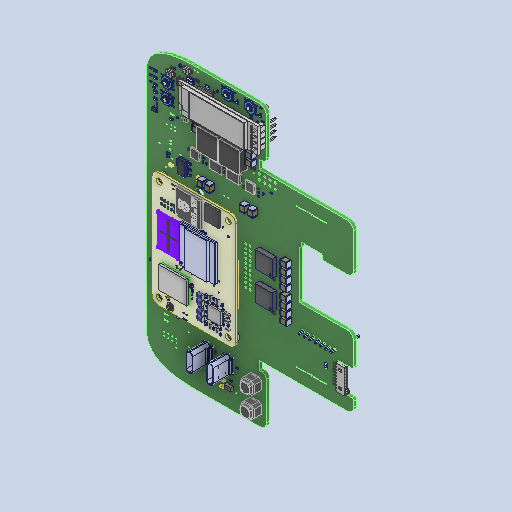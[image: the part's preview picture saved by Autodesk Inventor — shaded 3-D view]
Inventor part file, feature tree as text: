
AUTODESK INVENTOR PART (.ipt)
format: ipt  version: 2022 (Build 260153000, 153)  size: 57,349,120 bytes
history: native  units: mm
features: other x3628, sketch x2440, extrude x2
ambient origin geometry x8: Origin, YZ Plane, XZ Plane, XY Plane, X Axis, Y Axis, Z Axis, Center Point
bodies: Body1 (feature_tree), Body2 (feature_tree), Body3 (feature_tree), Body4 (feature_tree), Body5 (feature_tree), Body6 (feature_tree), Body7 (feature_tree), Body8 (feature_tree), Body9 (feature_tree), Body10 (feature_tree), Body11 (feature_tree), Body12 (feature_tree), Body13 (feature_tree), Body14 (feature_tree), Body15 (feature_tree), Body16 (feature_tree), Body17 (feature_tree), Body18 (feature_tree), Body19 (feature_tree), Body20 (feature_tree), Body21 (feature_tree), Body22 (feature_tree), Body23 (feature_tree), Body24 (feature_tree), Body25 (feature_tree), Body26 (feature_tree), Body27 (feature_tree), Body28 (feature_tree), Body29 (feature_tree), Body30 (feature_tree), Body31 (feature_tree), Body32 (feature_tree), Body33 (feature_tree), Body34 (feature_tree), Body35 (feature_tree), Body36 (feature_tree), Body37 (feature_tree), Body38 (feature_tree), Body39 (feature_tree), Body40 (feature_tree), Body41 (feature_tree), Body42 (feature_tree), Body43 (feature_tree), Body44 (feature_tree), Body45 (feature_tree), Body46 (feature_tree), Body47 (feature_tree), Body48 (feature_tree), Body49 (feature_tree), Body50 (feature_tree), Body51 (feature_tree), Body52 (feature_tree), Body53 (feature_tree), Body54 (feature_tree), Body55 (feature_tree), Body56 (feature_tree), Body57 (feature_tree), Body58 (feature_tree), Body59 (feature_tree), Body60 (feature_tree), Body61 (feature_tree), Body62 (feature_tree), Body63 (feature_tree), Body64 (feature_tree), Body65 (feature_tree), Body66 (feature_tree), Body67 (feature_tree), Body68 (feature_tree), Body69 (feature_tree), Body70 (feature_tree), Body71 (feature_tree), Body72 (feature_tree), Body73 (feature_tree), Body74 (feature_tree), Body75 (feature_tree), Body76 (feature_tree), Body77 (feature_tree), Body78 (feature_tree), Body79 (feature_tree), Body80 (feature_tree), Body81 (feature_tree), Body82 (feature_tree), Body83 (feature_tree), Body84 (feature_tree), Body85 (feature_tree), Body86 (feature_tree), Body87 (feature_tree), Body88 (feature_tree), Body89 (feature_tree), Body90 (feature_tree), Body91 (feature_tree), Body92 (feature_tree), Body93 (feature_tree), Body94 (feature_tree), Body95 (feature_tree), Body96 (feature_tree), Body97 (feature_tree), Body98 (feature_tree), Body99 (feature_tree), Body100 (feature_tree), Body101 (feature_tree), Body102 (feature_tree), Body103 (feature_tree), Body104 (feature_tree), Body105 (feature_tree), Body106 (feature_tree), Body107 (feature_tree), Body108 (feature_tree), Body109 (feature_tree), Body110 (feature_tree), Body111 (feature_tree), Body112 (feature_tree), Body113 (feature_tree), Body114 (feature_tree), Body115 (feature_tree), Body116 (feature_tree), Body117 (feature_tree), Body118 (feature_tree), Body119 (feature_tree), Body120 (feature_tree), Body121 (feature_tree), Body122 (feature_tree), Body123 (feature_tree), Body124 (feature_tree), Body125 (feature_tree), Body126 (feature_tree), Body127 (feature_tree), Body128 (feature_tree), Body129 (feature_tree), Body130 (feature_tree), Body131 (feature_tree), Body132 (feature_tree), Body133 (feature_tree), Body134 (feature_tree), Body135 (feature_tree), Body136 (feature_tree), Body137 (feature_tree), Body138 (feature_tree), Body139 (feature_tree), Body140 (feature_tree), Body141 (feature_tree), Body142 (feature_tree), Body143 (feature_tree), Body144 (feature_tree), Body145 (feature_tree), Body146 (feature_tree), Body147 (feature_tree), Body148 (feature_tree), Body149 (feature_tree), Body150 (feature_tree), Body151 (feature_tree), Body152 (feature_tree), Body153 (feature_tree), Body154 (feature_tree), Body155 (feature_tree), Body156 (feature_tree), Body157 (feature_tree), Body158 (feature_tree), Body159 (feature_tree), Body160 (feature_tree), Body161 (feature_tree), Body162 (feature_tree), Body163 (feature_tree), Body164 (feature_tree), Body165 (feature_tree), Body166 (feature_tree), Body167 (feature_tree), Body168 (feature_tree), Body169 (feature_tree), Body170 (feature_tree), Body171 (feature_tree), Body172 (feature_tree), Body173 (feature_tree), Body174 (feature_tree), Body175 (feature_tree), Body176 (feature_tree), Body177 (feature_tree), Body178 (feature_tree), Body179 (feature_tree), Body180 (feature_tree), Body181 (feature_tree), Body182 (feature_tree), Body183 (feature_tree), Body184 (feature_tree), Body185 (feature_tree), Body186 (feature_tree), Body187 (feature_tree), Body188 (feature_tree), Body189 (feature_tree), Body190 (feature_tree), Body191 (feature_tree), Body192 (feature_tree), Body193 (feature_tree), Body194 (feature_tree), Body195 (feature_tree), Body196 (feature_tree), Body197 (feature_tree), Body198 (feature_tree), Body199 (feature_tree), Body200 (feature_tree), Body201 (feature_tree), Body202 (feature_tree), Body203 (feature_tree), Body204 (feature_tree), Body205 (feature_tree), Body206 (feature_tree), Body207 (feature_tree), Body208 (feature_tree), Body209 (feature_tree), Body210 (feature_tree), Body211 (feature_tree), Body212 (feature_tree), Body213 (feature_tree), Body214 (feature_tree), Body215 (feature_tree), Body216 (feature_tree), Body217 (feature_tree), Body218 (feature_tree), Body219 (feature_tree), Body220 (feature_tree), Body221 (feature_tree), Body222 (feature_tree), Body223 (feature_tree), Body224 (feature_tree), Body225 (feature_tree), Body226 (feature_tree), Body227 (feature_tree), Body228 (feature_tree), Body229 (feature_tree), Body230 (feature_tree), Body231 (feature_tree), Body232 (feature_tree), Body233 (feature_tree), Body234 (feature_tree), Body235 (feature_tree), Body236 (feature_tree), Body237 (feature_tree), Body238 (feature_tree), Body239 (feature_tree), Body240 (feature_tree), Body241 (feature_tree), Body242 (feature_tree), Body243 (feature_tree), Body244 (feature_tree), Body245 (feature_tree), Body246 (feature_tree), Body247 (feature_tree), Body248 (feature_tree), Body249 (feature_tree), Body250 (feature_tree), Body251 (feature_tree), Body252 (feature_tree), Body253 (feature_tree), Body254 (feature_tree), Body255 (feature_tree), Body256 (feature_tree), Body257 (feature_tree), Body258 (feature_tree), Body259 (feature_tree), Body260 (feature_tree), Body261 (feature_tree), Body262 (feature_tree), Body263 (feature_tree), Body264 (feature_tree), Body265 (feature_tree), Body266 (feature_tree), Body267 (feature_tree), Body268 (feature_tree), Body269 (feature_tree), Body270 (feature_tree), Body271 (feature_tree), Body272 (feature_tree), Body273 (feature_tree), Body274 (feature_tree), Body275 (feature_tree), Body276 (feature_tree), Body277 (feature_tree), Body278 (feature_tree), Body279 (feature_tree), Body280 (feature_tree), Body281 (feature_tree), Body282 (feature_tree), Body283 (feature_tree), Body284 (feature_tree), Body285 (feature_tree), Body286 (feature_tree), Body287 (feature_tree), Body288 (feature_tree), Body289 (feature_tree), Body290 (feature_tree), Body291 (feature_tree), Body292 (feature_tree), Body293 (feature_tree), Body294 (feature_tree), Body295 (feature_tree), Body296 (feature_tree), Body297 (feature_tree), Body298 (feature_tree), Body299 (feature_tree), Body300 (feature_tree), Body301 (feature_tree), Body302 (feature_tree), Body303 (feature_tree), Body304 (feature_tree), Body305 (feature_tree), Body306 (feature_tree), Body307 (feature_tree), Body308 (feature_tree), Body309 (feature_tree), Body310 (feature_tree), Body311 (feature_tree), Body312 (feature_tree), Body313 (feature_tree), Body314 (feature_tree), Body315 (feature_tree), Body316 (feature_tree), Body317 (feature_tree), Body318 (feature_tree), Body319 (feature_tree), Body320 (feature_tree), Body321 (feature_tree), Body322 (feature_tree), Body323 (feature_tree), Body324 (feature_tree), Body325 (feature_tree), Body326 (feature_tree), Body327 (feature_tree), Body328 (feature_tree), Body329 (feature_tree), Body330 (feature_tree), Body331 (feature_tree), Body332 (feature_tree), Body333 (feature_tree), Body334 (feature_tree), Body335 (feature_tree), Body336 (feature_tree), Body337 (feature_tree), Body338 (feature_tree), Body339 (feature_tree), Body340 (feature_tree), Body341 (feature_tree), Body342 (feature_tree), Body343 (feature_tree), Body344 (feature_tree), Body345 (feature_tree), Body346 (feature_tree), Body347 (feature_tree), Body348 (feature_tree), Body349 (feature_tree), Body350 (feature_tree), Body351 (feature_tree), Body352 (feature_tree), Body353 (feature_tree), Body354 (feature_tree), Body355 (feature_tree), Body356 (feature_tree), Body357 (feature_tree), Body358 (feature_tree), Body359 (feature_tree), Body360 (feature_tree), Body361 (feature_tree), Body362 (feature_tree), Body363 (feature_tree), Body364 (feature_tree), Body365 (feature_tree), Body366 (feature_tree), Body367 (feature_tree), Body368 (feature_tree), Body369 (feature_tree), Body370 (feature_tree), Body371 (feature_tree), Body372 (feature_tree), Body373 (feature_tree), Body374 (feature_tree), Body375 (feature_tree), Body376 (feature_tree), Body377 (feature_tree), Body378 (feature_tree), Body379 (feature_tree), Body380 (feature_tree), Body381 (feature_tree), Body382 (feature_tree), Body383 (feature_tree), Body384 (feature_tree), Body385 (feature_tree), Body386 (feature_tree), Body387 (feature_tree), Body388 (feature_tree), Body389 (feature_tree), Body390 (feature_tree), Body391 (feature_tree), Body392 (feature_tree), Body393 (feature_tree), Body394 (feature_tree), Body395 (feature_tree), Body396 (feature_tree), Body397 (feature_tree), Body398 (feature_tree), Body399 (feature_tree), Body400 (feature_tree), Body401 (feature_tree), Body402 (feature_tree), Body403 (feature_tree), Body404 (feature_tree), Body405 (feature_tree), Body406 (feature_tree), Body407 (feature_tree), Body408 (feature_tree), Body409 (feature_tree), Body410 (feature_tree), Body411 (feature_tree), Body412 (feature_tree), Body413 (feature_tree), Body414 (feature_tree), Body415 (feature_tree), Body416 (feature_tree), Body417 (feature_tree), Body418 (feature_tree), Body419 (feature_tree), Body420 (feature_tree), Body421 (feature_tree), Body422 (feature_tree), Body423 (feature_tree), Body424 (feature_tree), Body425 (feature_tree), Body426 (feature_tree), Body427 (feature_tree), Body428 (feature_tree), Body429 (feature_tree), Body430 (feature_tree), Body431 (feature_tree), Body432 (feature_tree), Body433 (feature_tree), Body434 (feature_tree), Body435 (feature_tree), Body436 (feature_tree), Body437 (feature_tree), Body438 (feature_tree), Body439 (feature_tree), Body440 (feature_tree), Body441 (feature_tree), Body442 (feature_tree), Body443 (feature_tree), Body444 (feature_tree), Body445 (feature_tree), Body446 (feature_tree), Body447 (feature_tree), Body448 (feature_tree), Body449 (feature_tree), Body450 (feature_tree), Body451 (feature_tree), Body452 (feature_tree), Body453 (feature_tree), Body454 (feature_tree), Body455 (feature_tree), Body456 (feature_tree), Body457 (feature_tree), Body458 (feature_tree), Body459 (feature_tree), Body460 (feature_tree), Body461 (feature_tree), Body462 (feature_tree), Body463 (feature_tree), Body464 (feature_tree), Body465 (feature_tree), Body466 (feature_tree), Body467 (feature_tree), Body468 (feature_tree), Body469 (feature_tree), Body470 (feature_tree), Body471 (feature_tree), Body472 (feature_tree), Body473 (feature_tree), Body474 (feature_tree), Body475 (feature_tree), Body476 (feature_tree), Body477 (feature_tree), Body478 (feature_tree), Body479 (feature_tree), Body480 (feature_tree), Body481 (feature_tree), Body482 (feature_tree), Body483 (feature_tree), Body484 (feature_tree), Body485 (feature_tree), Body486 (feature_tree), Body487 (feature_tree), Body488 (feature_tree), Body489 (feature_tree), Body490 (feature_tree), Body491 (feature_tree), Body492 (feature_tree), Body493 (feature_tree), Body494 (feature_tree), Body495 (feature_tree), Body496 (feature_tree), Body497 (feature_tree), Body498 (feature_tree), Body499 (feature_tree), Body500 (feature_tree), Body501 (feature_tree), Body502 (feature_tree), Body503 (feature_tree), Body504 (feature_tree), Body505 (feature_tree), Body506 (feature_tree), Body507 (feature_tree), Body508 (feature_tree), Body509 (feature_tree), Body510 (feature_tree), Body511 (feature_tree), Body512 (feature_tree), Body513 (feature_tree), Body514 (feature_tree), Body515 (feature_tree), Body516 (feature_tree), Body517 (feature_tree), Body518 (feature_tree), Body519 (feature_tree), Body520 (feature_tree), Body521 (feature_tree), Body522 (feature_tree), Body523 (feature_tree), Body524 (feature_tree), Body525 (feature_tree), Body526 (feature_tree), Body527 (feature_tree), Body528 (feature_tree), Body529 (feature_tree), Body530 (feature_tree), Body531 (feature_tree), Body532 (feature_tree), Body533 (feature_tree), Body534 (feature_tree), Body535 (feature_tree), Body536 (feature_tree), Body537 (feature_tree), Body538 (feature_tree), Body539 (feature_tree), Body540 (feature_tree), Body541 (feature_tree), Body542 (feature_tree), Body543 (feature_tree), Body544 (feature_tree), Body545 (feature_tree), Body546 (feature_tree), Body547 (feature_tree), Body548 (feature_tree), Body549 (feature_tree), Body550 (feature_tree), Body551 (feature_tree), Body552 (feature_tree), Body553 (feature_tree), Body554 (feature_tree), Body555 (feature_tree), Body556 (feature_tree), Body557 (feature_tree), Body558 (feature_tree), Body559 (feature_tree), Body560 (feature_tree), Body561 (feature_tree), Body562 (feature_tree), Body563 (feature_tree), Body564 (feature_tree), Body565 (feature_tree), Body566 (feature_tree), Body567 (feature_tree), Body568 (feature_tree), Body569 (feature_tree), Body570 (feature_tree), Body571 (feature_tree), Body572 (feature_tree), Body573 (feature_tree), Body574 (feature_tree), Body575 (feature_tree), Body576 (feature_tree), Body577 (feature_tree), Body578 (feature_tree), Body579 (feature_tree), Body580 (feature_tree), Body581 (feature_tree), Body582 (feature_tree), Body583 (feature_tree), Body584 (feature_tree), Body585 (feature_tree), Body586 (feature_tree), Body587 (feature_tree), Body588 (feature_tree), Body589 (feature_tree), Body590 (feature_tree), Body591 (feature_tree), Body592 (feature_tree), Body593 (feature_tree), Body594 (feature_tree), Body595 (feature_tree), Body596 (feature_tree), Body597 (feature_tree), Body598 (feature_tree), Body599 (feature_tree), Body600 (feature_tree), Body601 (feature_tree), Body602 (feature_tree), Body603 (feature_tree), Body604 (feature_tree), Body605 (feature_tree), Body606 (feature_tree), Body607 (feature_tree), Body608 (feature_tree), Body609 (feature_tree), Body610 (feature_tree), Body611 (feature_tree), Body612 (feature_tree), Body613 (feature_tree), Body614 (feature_tree), Body615 (feature_tree), Body616 (feature_tree), Body617 (feature_tree), Body618 (feature_tree), Body619 (feature_tree), Body620 (feature_tree), Body621 (feature_tree), Body622 (feature_tree), Body623 (feature_tree), Body624 (feature_tree), Body625 (feature_tree), Body626 (feature_tree), Body627 (feature_tree), Body628 (feature_tree), Body629 (feature_tree), Body630 (feature_tree), Body631 (feature_tree), Body632 (feature_tree), Body633 (feature_tree), Body634 (feature_tree), Body635 (feature_tree), Body636 (feature_tree), Body637 (feature_tree), Body638 (feature_tree), Body639 (feature_tree), Body640 (feature_tree), Body641 (feature_tree), Body642 (feature_tree), Body643 (feature_tree), Body644 (feature_tree), Body645 (feature_tree), Body646 (feature_tree), Body647 (feature_tree), Body648 (feature_tree), Body649 (feature_tree), Body650 (feature_tree), Body651 (feature_tree), Body652 (feature_tree), Body653 (feature_tree), Body654 (feature_tree), Body655 (feature_tree), Body656 (feature_tree), Body657 (feature_tree), Body658 (feature_tree), Body659 (feature_tree), Body660 (feature_tree), Body661 (feature_tree), Body662 (feature_tree), Body663 (feature_tree), Body664 (feature_tree), Body665 (feature_tree), Body666 (feature_tree), Body667 (feature_tree), Body668 (feature_tree), Body669 (feature_tree), Body670 (feature_tree), Body671 (feature_tree), Body672 (feature_tree), Body673 (feature_tree), Body674 (feature_tree), Body675 (feature_tree), Body676 (feature_tree), Body677 (feature_tree), Body678 (feature_tree), Body679 (feature_tree), Body680 (feature_tree), Body681 (feature_tree), Body682 (feature_tree), Body683 (feature_tree), Body684 (feature_tree), Body685 (feature_tree), Body686 (feature_tree), Body687 (feature_tree), Body688 (feature_tree), Body689 (feature_tree), Body690 (feature_tree), Body691 (feature_tree), Body692 (feature_tree), Body693 (feature_tree), Body694 (feature_tree), Body695 (feature_tree), Body696 (feature_tree), Body697 (feature_tree), Body698 (feature_tree), Body699 (feature_tree), Body700 (feature_tree), Body701 (feature_tree), Body702 (feature_tree), Body703 (feature_tree), Body704 (feature_tree), Body705 (feature_tree), Body706 (feature_tree), Body707 (feature_tree), Body708 (feature_tree), Body709 (feature_tree), Body710 (feature_tree), Body711 (feature_tree), Body712 (feature_tree), Body713 (feature_tree), Body714 (feature_tree), Body715 (feature_tree), Body716 (feature_tree), Body717 (feature_tree), Body718 (feature_tree), Body719 (feature_tree), Body720 (feature_tree), Body721 (feature_tree), Body722 (feature_tree), Body723 (feature_tree), Body724 (feature_tree), Body725 (feature_tree), Body726 (feature_tree), Body727 (feature_tree), Body728 (feature_tree), Body729 (feature_tree), Body730 (feature_tree), Body731 (feature_tree), Body732 (feature_tree), Body733 (feature_tree), Body734 (feature_tree), Body735 (feature_tree), Body736 (feature_tree), Body737 (feature_tree), Body738 (feature_tree), Body739 (feature_tree), Body740 (feature_tree), Body741 (feature_tree), Body742 (feature_tree), Body743 (feature_tree), Body744 (feature_tree), Body745 (feature_tree), Body746 (feature_tree), Body747 (feature_tree), Body748 (feature_tree), Body749 (feature_tree), Body750 (feature_tree), Body751 (feature_tree), Body752 (feature_tree), Body753 (feature_tree), Body754 (feature_tree), Body755 (feature_tree), Body756 (feature_tree), Body757 (feature_tree), Body758 (feature_tree), Body759 (feature_tree), Body760 (feature_tree), Body761 (feature_tree), Body762 (feature_tree), Body763 (feature_tree), Body764 (feature_tree), Body765 (feature_tree), Body766 (feature_tree), Body767 (feature_tree), Body768 (feature_tree), Body769 (feature_tree), Body770 (feature_tree), Body771 (feature_tree), Body772 (feature_tree), Body773 (feature_tree), Body774 (feature_tree), Body775 (feature_tree), Body776 (feature_tree), Body777 (feature_tree), Body778 (feature_tree), Body779 (feature_tree), Body780 (feature_tree), Body781 (feature_tree), Body782 (feature_tree), Body783 (feature_tree), Body784 (feature_tree), Body785 (feature_tree), Body786 (feature_tree), Body787 (feature_tree), Body788 (feature_tree), Body789 (feature_tree), Body790 (feature_tree), Body791 (feature_tree), Body792 (feature_tree), Body793 (feature_tree), Body794 (feature_tree), Body795 (feature_tree), Body796 (feature_tree), Body797 (feature_tree), Body798 (feature_tree), Body799 (feature_tree), Body800 (feature_tree), Body801 (feature_tree), Body802 (feature_tree), Body803 (feature_tree), Body804 (feature_tree), Body805 (feature_tree), Body806 (feature_tree), Body807 (feature_tree), Body808 (feature_tree), Body809 (feature_tree), Body810 (feature_tree), Body811 (feature_tree), Body812 (feature_tree), Body813 (feature_tree), Body814 (feature_tree), Body815 (feature_tree), Body816 (feature_tree), Body817 (feature_tree), Body818 (feature_tree), Body819 (feature_tree), Body820 (feature_tree), Body821 (feature_tree), Body822 (feature_tree), Body823 (feature_tree), Body824 (feature_tree), Body825 (feature_tree), Body826 (feature_tree), Body827 (feature_tree), Body828 (feature_tree), Body829 (feature_tree), Body830 (feature_tree), Body831 (feature_tree), Body832 (feature_tree), Body833 (feature_tree), Body834 (feature_tree), Body835 (feature_tree), Body836 (feature_tree), Body837 (feature_tree), Body838 (feature_tree), Body839 (feature_tree), Body840 (feature_tree), Body841 (feature_tree), Body842 (feature_tree), Body843 (feature_tree), Body844 (feature_tree), Body845 (feature_tree), Body846 (feature_tree), Body847 (feature_tree), Body848 (feature_tree), Body849 (feature_tree), Body850 (feature_tree), Body851 (feature_tree), Body852 (feature_tree), Body853 (feature_tree), Body854 (feature_tree), Body855 (feature_tree), Body856 (feature_tree), Body857 (feature_tree), Body858 (feature_tree), Body859 (feature_tree), Body860 (feature_tree), Body861 (feature_tree), Body862 (feature_tree), Body863 (feature_tree), Body864 (feature_tree), Body865 (feature_tree), Body866 (feature_tree), Body867 (feature_tree), Body868 (feature_tree), Body869 (feature_tree), Body870 (feature_tree), Body871 (feature_tree), Body872 (feature_tree), Body873 (feature_tree), Body874 (feature_tree), Body875 (feature_tree), Body876 (feature_tree), Body877 (feature_tree), Body878 (feature_tree), Body879 (feature_tree), Body880 (feature_tree), Body881 (feature_tree), Body882 (feature_tree), Body883 (feature_tree), Body884 (feature_tree), Body885 (feature_tree), Body886 (feature_tree), Body887 (feature_tree), Body888 (feature_tree), Body889 (feature_tree), Body890 (feature_tree), Body891 (feature_tree), Body892 (feature_tree), Body893 (feature_tree), Body894 (feature_tree), Body895 (feature_tree), Body896 (feature_tree), Body897 (feature_tree), Body898 (feature_tree), Body899 (feature_tree), Body900 (feature_tree), Body901 (feature_tree), Body902 (feature_tree), Body903 (feature_tree), Body904 (feature_tree), Body905 (feature_tree), Body906 (feature_tree), Body907 (feature_tree), Body908 (feature_tree), Body909 (feature_tree), Body910 (feature_tree), Body911 (feature_tree), Body912 (feature_tree), Body913 (feature_tree), Body914 (feature_tree), Body915 (feature_tree), Body916 (feature_tree), Body917 (feature_tree), Body918 (feature_tree), Body919 (feature_tree), Body920 (feature_tree), Body921 (feature_tree), Body922 (feature_tree), Body923 (feature_tree), Body924 (feature_tree), Body925 (feature_tree), Body926 (feature_tree), Body927 (feature_tree), Body928 (feature_tree), Body929 (feature_tree), Body930 (feature_tree), Body931 (feature_tree), Body932 (feature_tree), Body933 (feature_tree), Body934 (feature_tree), Body935 (feature_tree), Body936 (feature_tree), Body937 (feature_tree), Body938 (feature_tree), Body939 (feature_tree), Body940 (feature_tree), Body941 (feature_tree), Body942 (feature_tree), Body943 (feature_tree), Body944 (feature_tree), Body945 (feature_tree), Body946 (feature_tree), Body947 (feature_tree), Body948 (feature_tree), Body949 (feature_tree), Body950 (feature_tree), Body951 (feature_tree), Body952 (feature_tree), Body953 (feature_tree), Body954 (feature_tree), Body955 (feature_tree), Body956 (feature_tree), Body957 (feature_tree), Body958 (feature_tree), Body959 (feature_tree), Body960 (feature_tree), Body961 (feature_tree), Body962 (feature_tree), Body963 (feature_tree), Body964 (feature_tree), Body965 (feature_tree), Body966 (feature_tree), Body967 (feature_tree), Body968 (feature_tree), Body969 (feature_tree), Body970 (feature_tree), Body971 (feature_tree), Body972 (feature_tree), Body973 (feature_tree), Body974 (feature_tree), Body975 (feature_tree), Body976 (feature_tree), Body977 (feature_tree), Body978 (feature_tree), Body979 (feature_tree), Body980 (feature_tree), Body981 (feature_tree), Body982 (feature_tree), Body983 (feature_tree), Body984 (feature_tree), Body985 (feature_tree), Body986 (feature_tree), Body987 (feature_tree), Body988 (feature_tree), Body989 (feature_tree), Body990 (feature_tree), Body991 (feature_tree), Body992 (feature_tree), Body993 (feature_tree), Body994 (feature_tree), Body995 (feature_tree), Body996 (feature_tree), Body997 (feature_tree), Body998 (feature_tree), Body999 (feature_tree), Body1000 (feature_tree), Body1001 (feature_tree), Body1002 (feature_tree), Body1003 (feature_tree), Body1004 (feature_tree), Body1005 (feature_tree), Body1006 (feature_tree), Body1007 (feature_tree), Body1008 (feature_tree), Body1009 (feature_tree), Body1010 (feature_tree), Body1011 (feature_tree), Body1012 (feature_tree), Body1013 (feature_tree), Body1014 (feature_tree), Body1015 (feature_tree), Body1016 (feature_tree), Body1017 (feature_tree), Body1018 (feature_tree), Body1019 (feature_tree), Body1020 (feature_tree), Body1021 (feature_tree), Body1022 (feature_tree), Body1023 (feature_tree), Body1024 (feature_tree), Body1025 (feature_tree), Body1026 (feature_tree), Body1027 (feature_tree), Body1028 (feature_tree), Body1029 (feature_tree), Body1030 (feature_tree), Body1031 (feature_tree), Body1032 (feature_tree), Body1033 (feature_tree), Body1034 (feature_tree), Body1035 (feature_tree), Body1036 (feature_tree), Body1037 (feature_tree), Body1038 (feature_tree), Body1039 (feature_tree), Body1040 (feature_tree), Body1041 (feature_tree), Body1042 (feature_tree), Body1043 (feature_tree), Body1044 (feature_tree), Body1045 (feature_tree), Body1046 (feature_tree), Body1047 (feature_tree), Body1048 (feature_tree), Body1049 (feature_tree), Body1050 (feature_tree), Body1051 (feature_tree), Body1052 (feature_tree), Body1053 (feature_tree), Body1054 (feature_tree), Body1055 (feature_tree), Body1056 (feature_tree), Body1057 (feature_tree), Body1058 (feature_tree), Body1059 (feature_tree), Body1060 (feature_tree), Body1061 (feature_tree), Body1062 (feature_tree), Body1063 (feature_tree), Body1064 (feature_tree), Body1065 (feature_tree), Body1066 (feature_tree), Body1067 (feature_tree), Body1068 (feature_tree), Body1069 (feature_tree), Body1070 (feature_tree), Body1071 (feature_tree), Body1072 (feature_tree), Body1073 (feature_tree), Body1074 (feature_tree), Body1075 (feature_tree), Body1076 (feature_tree), Body1077 (feature_tree), Body1078 (feature_tree), Body1079 (feature_tree), Body1080 (feature_tree), Body1081 (feature_tree), Body1082 (feature_tree), Body1083 (feature_tree), Body1084 (feature_tree), Body1085 (feature_tree), Body1086 (feature_tree), Body1087 (feature_tree), Body1088 (feature_tree), Body1089 (feature_tree), Body1090 (feature_tree), Body1091 (feature_tree), Body1092 (feature_tree), Body1093 (feature_tree), Body1094 (feature_tree), Body1095 (feature_tree), Body1096 (feature_tree), Body1097 (feature_tree), Body1098 (feature_tree), Body1099 (feature_tree), Body1100 (feature_tree), Body1101 (feature_tree), Body1102 (feature_tree), Body1103 (feature_tree), Body1104 (feature_tree), Body1105 (feature_tree), Body1106 (feature_tree), Body1107 (feature_tree), Body1108 (feature_tree), Body1109 (feature_tree), Body1110 (feature_tree), Body1111 (feature_tree), Body1112 (feature_tree), Body1113 (feature_tree), Body1114 (feature_tree), Body1115 (feature_tree), Body1116 (feature_tree), Body1117 (feature_tree), Body1118 (feature_tree), Body1119 (feature_tree), Body1120 (feature_tree), Body1121 (feature_tree), Body1122 (feature_tree), Body1123 (feature_tree), Body1124 (feature_tree), Body1125 (feature_tree), Body1126 (feature_tree), Body1127 (feature_tree), Body1128 (feature_tree), Body1129 (feature_tree), Body1130 (feature_tree), Body1131 (feature_tree), Body1132 (feature_tree), Body1133 (feature_tree), Body1134 (feature_tree), Body1135 (feature_tree), Body1136 (feature_tree), Body1137 (feature_tree), Body1138 (feature_tree), Body1139 (feature_tree), Body1140 (feature_tree), Body1141 (feature_tree), Body1142 (feature_tree), Body1143 (feature_tree), Body1144 (feature_tree), Body1145 (feature_tree), Body1146 (feature_tree), Body1147 (feature_tree), Body1148 (feature_tree), Body1149 (feature_tree), Body1150 (feature_tree), Body1151 (feature_tree), Body1152 (feature_tree), Body1153 (feature_tree), Body1154 (feature_tree), Body1155 (feature_tree), Body1156 (feature_tree), Body1157 (feature_tree), Body1158 (feature_tree), Body1159 (feature_tree), Body1160 (feature_tree), Body1161 (feature_tree), Body1162 (feature_tree), Body1163 (feature_tree), Body1164 (feature_tree), Body1165 (feature_tree), Body1166 (feature_tree), Body1167 (feature_tree), Body1168 (feature_tree), Body1169 (feature_tree), Body1170 (feature_tree), Body1171 (feature_tree), Body1172 (feature_tree), Body1173 (feature_tree), Body1174 (feature_tree), Body1175 (feature_tree), Body1176 (feature_tree), Body1177 (feature_tree), Body1178 (feature_tree), Body1179 (feature_tree), Body1180 (feature_tree), Body1181 (feature_tree), Body1182 (feature_tree), Body1183 (feature_tree), Body1184 (feature_tree), Body1185 (feature_tree), Body1186 (feature_tree), Body1187 (feature_tree), Body1188 (feature_tree), Body1189 (feature_tree), Body1190 (feature_tree), Body1191 (feature_tree), Body1192 (feature_tree), Body1193 (feature_tree), Body1194 (feature_tree), Body1195 (feature_tree), Body1196 (feature_tree), Body1197 (feature_tree), Body1198 (feature_tree), Body1199 (feature_tree), Body1200 (feature_tree), Body1201 (feature_tree), Body1202 (feature_tree), Body1203 (feature_tree), Body1204 (feature_tree), Body1205 (feature_tree), Body1206 (feature_tree), Body1207 (feature_tree), Body1208 (feature_tree), Body1209 (feature_tree), Body1210 (feature_tree), Body1211 (feature_tree), Body1212 (feature_tree), Body1213 (feature_tree), Body1214 (feature_tree), Body1215 (feature_tree), Body1216 (feature_tree), Body1217 (feature_tree), Body1218 (feature_tree), Body1219 (feature_tree), Body1220 (feature_tree), Body1221 (feature_tree), Body1222 (feature_tree), Body1223 (feature_tree), Body1224 (feature_tree), Body1225 (feature_tree), Body1226 (feature_tree), Body1227 (feature_tree), Body1228 (feature_tree), Body1229 (feature_tree), Body1230 (feature_tree), Body1231 (feature_tree), Body1232 (feature_tree), Body1233 (feature_tree), Body1234 (feature_tree), Body1235 (feature_tree), Body1236 (feature_tree), Body1237 (feature_tree), Body1238 (feature_tree), Body1239 (feature_tree), Body1240 (feature_tree), Body1241 (feature_tree), Body1242 (feature_tree), Body1243 (feature_tree), Body1244 (feature_tree), Body1245 (feature_tree), Body1246 (feature_tree), Body1247 (feature_tree), Body1248 (feature_tree), Body1249 (feature_tree), Body1250 (feature_tree), Body1251 (feature_tree), Body1252 (feature_tree), Body1253 (feature_tree), Body1254 (feature_tree), Body1255 (feature_tree), Body1256 (feature_tree), Body1257 (feature_tree), Body1258 (feature_tree), Body1259 (feature_tree), Body1260 (feature_tree), Body1261 (feature_tree), Body1262 (feature_tree), Body1263 (feature_tree), Body1264 (feature_tree), Body1265 (feature_tree), Body1266 (feature_tree), Body1267 (feature_tree), Body1268 (feature_tree), Body1269 (feature_tree), Body1270 (feature_tree), Body1271 (feature_tree), Body1272 (feature_tree), Body1273 (feature_tree), Body1274 (feature_tree), Body1275 (feature_tree), Body1276 (feature_tree), Body1277 (feature_tree), Body1278 (feature_tree), Body1279 (feature_tree), Body1280 (feature_tree), Body1281 (feature_tree), Body1282 (feature_tree), Body1283 (feature_tree), Body1284 (feature_tree), Body1285 (feature_tree), Body1286 (feature_tree), Body1287 (feature_tree), Body1288 (feature_tree), Body1289 (feature_tree), Body1290 (feature_tree), Body1291 (feature_tree), Body1292 (feature_tree), Body1293 (feature_tree), Body1294 (feature_tree), Body1295 (feature_tree), Body1296 (feature_tree), Body1297 (feature_tree), Body1298 (feature_tree), Body1299 (feature_tree), Body1300 (feature_tree), Body1301 (feature_tree), Body1302 (feature_tree), Body1303 (feature_tree), Body1304 (feature_tree), Body1305 (feature_tree), Body1306 (feature_tree), Body1307 (feature_tree), Body1308 (feature_tree), Body1309 (feature_tree), Body1310 (feature_tree), Body1311 (feature_tree), Body1312 (feature_tree), Body1313 (feature_tree), Body1314 (feature_tree), Body1315 (feature_tree), Body1316 (feature_tree), Body1317 (feature_tree), Body1318 (feature_tree), Body1319 (feature_tree), Body1320 (feature_tree), Body1321 (feature_tree), Body1322 (feature_tree), Body1323 (feature_tree), Body1324 (feature_tree), Body1325 (feature_tree), Body1326 (feature_tree), Body1327 (feature_tree), Body1328 (feature_tree), Body1329 (feature_tree), Body1330 (feature_tree), Body1331 (feature_tree), Body1332 (feature_tree), Body1333 (feature_tree), Body1334 (feature_tree), Body1335 (feature_tree), Body1336 (feature_tree), Body1337 (feature_tree), Body1338 (feature_tree), Body1339 (feature_tree), Body1340 (feature_tree), Body1341 (feature_tree), Body1342 (feature_tree), Body1343 (feature_tree), Body1344 (feature_tree), Body1345 (feature_tree), Body1346 (feature_tree), Body1347 (feature_tree), Body1348 (feature_tree), Body1349 (feature_tree), Body1350 (feature_tree), Body1351 (feature_tree), Body1352 (feature_tree), Body1353 (feature_tree), Body1354 (feature_tree), Body1355 (feature_tree), Body1356 (feature_tree), Body1357 (feature_tree), Body1358 (feature_tree), Body1359 (feature_tree), Body1360 (feature_tree), Body1361 (feature_tree), Body1362 (feature_tree), Body1363 (feature_tree), Body1364 (feature_tree), Body1365 (feature_tree), Body1366 (feature_tree), Body1367 (feature_tree), Body1368 (feature_tree), Body1369 (feature_tree), Body1370 (feature_tree), Body1371 (feature_tree), Body1372 (feature_tree), Body1373 (feature_tree), Body1374 (feature_tree), Body1375 (feature_tree), Body1376 (feature_tree), Body1377 (feature_tree), Body1378 (feature_tree), Body1379 (feature_tree), Body1380 (feature_tree), Body1381 (feature_tree), Body1382 (feature_tree), Body1383 (feature_tree), Body1384 (feature_tree), Body1385 (feature_tree), Body1386 (feature_tree), Body1387 (feature_tree), Body1388 (feature_tree), Body1389 (feature_tree), Body1390 (feature_tree), Body1391 (feature_tree), Body1392 (feature_tree), Body1393 (feature_tree), Body1394 (feature_tree), Body1395 (feature_tree), Body1396 (feature_tree), Body1397 (feature_tree), Body1398 (feature_tree), Body1399 (feature_tree), Body1400 (feature_tree), Body1401 (feature_tree), Body1402 (feature_tree), Body1403 (feature_tree), Body1404 (feature_tree), Body1405 (feature_tree), Body1406 (feature_tree), Body1407 (feature_tree), Body1408 (feature_tree), Body1409 (feature_tree), Body1410 (feature_tree), Body1411 (feature_tree), Body1412 (feature_tree), Body1413 (feature_tree), Body1414 (feature_tree), Body1415 (feature_tree), Body1416 (feature_tree), Body1417 (feature_tree), Body1418 (feature_tree), Body1419 (feature_tree), Body1420 (feature_tree), Body1421 (feature_tree), Body1422 (feature_tree), Body1423 (feature_tree), Body1424 (feature_tree), Body1425 (feature_tree), Body1426 (feature_tree), Body1427 (feature_tree), Body1428 (feature_tree), Body1429 (feature_tree), Body1430 (feature_tree), Body1431 (feature_tree), Body1432 (feature_tree), Body1433 (feature_tree), Body1434 (feature_tree), Body1435 (feature_tree), Body1436 (feature_tree), Body1437 (feature_tree), Body1438 (feature_tree), Body1439 (feature_tree), Body1440 (feature_tree), Body1441 (feature_tree), Body1442 (feature_tree), Body1443 (feature_tree), Body1444 (feature_tree), Body1445 (feature_tree), Body1446 (feature_tree), Body1447 (feature_tree), Body1448 (feature_tree), Body1449 (feature_tree), Body1450 (feature_tree), Body1451 (feature_tree), Body1452 (feature_tree), Body1453 (feature_tree), Body1454 (feature_tree), Body1455 (feature_tree), Body1456 (feature_tree), Body1457 (feature_tree), Body1458 (feature_tree), Body1459 (feature_tree), Body1460 (feature_tree), Body1461 (feature_tree), Body1462 (feature_tree), Body1463 (feature_tree), Body1464 (feature_tree), Body1465 (feature_tree), Body1466 (feature_tree), Body1467 (feature_tree), Body1468 (feature_tree), Body1469 (feature_tree), Body1470 (feature_tree), Body1471 (feature_tree), Body1472 (feature_tree), Body1473 (feature_tree), Body1474 (feature_tree), Body1475 (feature_tree), Body1476 (feature_tree), Body1477 (feature_tree), Body1478 (feature_tree), Body1479 (feature_tree), Body1480 (feature_tree), Body1481 (feature_tree), Body1482 (feature_tree), Body1483 (feature_tree), Body1484 (feature_tree), Body1485 (feature_tree), Body1486 (feature_tree), Body1487 (feature_tree), Body1488 (feature_tree), Body1489 (feature_tree), Body1490 (feature_tree), Body1491 (feature_tree), Body1492 (feature_tree), Body1493 (feature_tree), Body1494 (feature_tree), Body1495 (feature_tree), Body1496 (feature_tree), Body1497 (feature_tree), Body1498 (feature_tree), Body1499 (feature_tree), Body1500 (feature_tree), Body1501 (feature_tree), Body1502 (feature_tree), Body1503 (feature_tree), Body1504 (feature_tree), Body1505 (feature_tree), Body1506 (feature_tree), Body1507 (feature_tree), Body1508 (feature_tree), Body1509 (feature_tree), Body1510 (feature_tree), Body1511 (feature_tree), Body1512 (feature_tree), Body1513 (feature_tree), Body1514 (feature_tree), Body1515 (feature_tree), Body1516 (feature_tree), Body1517 (feature_tree), Body1518 (feature_tree), Body1519 (feature_tree), Body1520 (feature_tree), Body1521 (feature_tree), Body1522 (feature_tree), Body1523 (feature_tree), Body1524 (feature_tree), Body1525 (feature_tree), Body1526 (feature_tree), Body1527 (feature_tree), Body1528 (feature_tree), Body1529 (feature_tree), Body1530 (feature_tree), Body1531 (feature_tree), Body1532 (feature_tree), Body1533 (feature_tree), Body1534 (feature_tree), Body1535 (feature_tree), Body1536 (feature_tree), Body1537 (feature_tree), Body1538 (feature_tree), Body1539 (feature_tree), Body1540 (feature_tree), Body1541 (feature_tree), Body1542 (feature_tree), Body1543 (feature_tree), Body1544 (feature_tree), Body1545 (feature_tree), Body1546 (feature_tree), Body1547 (feature_tree), Body1548 (feature_tree), Body1549 (feature_tree), Body1550 (feature_tree), Body1551 (feature_tree), Body1552 (feature_tree), Body1553 (feature_tree), Body1554 (feature_tree), Body1555 (feature_tree), Body1556 (feature_tree), Body1557 (feature_tree), Body1558 (feature_tree), Body1559 (feature_tree), Body1560 (feature_tree), Body1561 (feature_tree), Body1562 (feature_tree), Body1563 (feature_tree), Body1564 (feature_tree), Body1565 (feature_tree), Body1566 (feature_tree), Body1567 (feature_tree), Body1568 (feature_tree), Body1569 (feature_tree), Body1570 (feature_tree), Body1571 (feature_tree), Body1572 (feature_tree), Body1573 (feature_tree), Body1574 (feature_tree), Body1575 (feature_tree), Body1576 (feature_tree), Body1577 (feature_tree), Body1578 (feature_tree), Body1579 (feature_tree), Body1580 (feature_tree), Body1581 (feature_tree), Body1582 (feature_tree), Body1583 (feature_tree), Body1584 (feature_tree), Body1585 (feature_tree), Body1586 (feature_tree), Body1587 (feature_tree), Body1588 (feature_tree), Body1589 (feature_tree), Body1590 (feature_tree), Body1591 (feature_tree), Body1592 (feature_tree), Body1593 (feature_tree), Body1594 (feature_tree), Body1595 (feature_tree), Body1596 (feature_tree), Body1597 (feature_tree), Body1598 (feature_tree), Body1599 (feature_tree), Body1600 (feature_tree), Body1601 (feature_tree), Body1602 (feature_tree), Body1603 (feature_tree), Body1604 (feature_tree), Body1605 (feature_tree), Body1606 (feature_tree), Body1607 (feature_tree), Body1608 (feature_tree), Body1609 (feature_tree), Body1610 (feature_tree), Body1611 (feature_tree), Body1612 (feature_tree), Body1613 (feature_tree), Body1614 (feature_tree), Body1615 (feature_tree), Body1616 (feature_tree), Body1617 (feature_tree), Body1618 (feature_tree), Body1619 (feature_tree), Body1620 (feature_tree), Body1621 (feature_tree), Body1622 (feature_tree), Body1623 (feature_tree), Body1624 (feature_tree), Body1625 (feature_tree), Body1626 (feature_tree), Body1627 (feature_tree), Body1628 (feature_tree), Body1629 (feature_tree), Body1630 (feature_tree), Body1631 (feature_tree), Body1632 (feature_tree), Body1633 (feature_tree), Body1634 (feature_tree), Body1635 (feature_tree), Body1636 (feature_tree), Body1637 (feature_tree), Body1638 (feature_tree), Body1639 (feature_tree), Body1640 (feature_tree), Body1641 (feature_tree), Body1642 (feature_tree), Body1643 (feature_tree), Body1644 (feature_tree), Body1645 (feature_tree), Body1646 (feature_tree), Body1647 (feature_tree), Body1648 (feature_tree), Body1649 (feature_tree), Body1650 (feature_tree), Body1651 (feature_tree), Body1652 (feature_tree), Body1653 (feature_tree), Body1654 (feature_tree), Body1655 (feature_tree), Body1656 (feature_tree), Body1657 (feature_tree), Body1658 (feature_tree), Body1659 (feature_tree), Body1660 (feature_tree), Body1661 (feature_tree), Body1662 (feature_tree), Body1663 (feature_tree), Body1664 (feature_tree), Body1665 (feature_tree), Body1666 (feature_tree), Body1667 (feature_tree), Body1668 (feature_tree), Body1669 (feature_tree), Body1670 (feature_tree), Body1671 (feature_tree), Body1672 (feature_tree), Body1673 (feature_tree), Body1674 (feature_tree), Body1675 (feature_tree), Body1676 (feature_tree), Body1677 (feature_tree), Body1678 (feature_tree), Body1679 (feature_tree), Body1680 (feature_tree), Body1681 (feature_tree), Body1682 (feature_tree), Body1683 (feature_tree), Body1684 (feature_tree), Body1685 (feature_tree), Body1686 (feature_tree), Body1687 (feature_tree), Body1688 (feature_tree), Body1689 (feature_tree), Body1690 (feature_tree), Body1691 (feature_tree), Body1692 (feature_tree), Body1693 (feature_tree), Body1694 (feature_tree), Body1695 (feature_tree), Body1696 (feature_tree), Body1697 (feature_tree), Body1698 (feature_tree), Body1699 (feature_tree), Body1700 (feature_tree), Body1701 (feature_tree), Body1702 (feature_tree), Body1703 (feature_tree), Body1704 (feature_tree), Body1705 (feature_tree), Body1706 (feature_tree), Body1707 (feature_tree), Body1708 (feature_tree), Body1709 (feature_tree), Body1710 (feature_tree), Body1711 (feature_tree), Body1712 (feature_tree), Body1713 (feature_tree), Body1714 (feature_tree), Body1715 (feature_tree), Body1716 (feature_tree), Body1717 (feature_tree), Body1718 (feature_tree), Body1719 (feature_tree), Body1720 (feature_tree), Body1721 (feature_tree), Body1722 (feature_tree), Body1723 (feature_tree), Body1724 (feature_tree), Body1725 (feature_tree), Body1726 (feature_tree), Body1727 (feature_tree), Body1728 (feature_tree), Body1729 (feature_tree), Body1730 (feature_tree), Body1731 (feature_tree), Body1732 (feature_tree), Body1733 (feature_tree), Body1734 (feature_tree), Body1735 (feature_tree), Body1736 (feature_tree), Body1737 (feature_tree), Body1738 (feature_tree), Body1739 (feature_tree), Body1740 (feature_tree), Body1741 (feature_tree), Body1742 (feature_tree), Body1743 (feature_tree), Body1744 (feature_tree), Body1745 (feature_tree), Body1746 (feature_tree), Body1747 (feature_tree), Body1748 (feature_tree), Body1749 (feature_tree), Body1750 (feature_tree), Body1751 (feature_tree), Body1752 (feature_tree), Body1753 (feature_tree), Body1754 (feature_tree), Body1755 (feature_tree), Body1756 (feature_tree), Body1757 (feature_tree), Body1758 (feature_tree), Body1759 (feature_tree), Body1760 (feature_tree), Body1761 (feature_tree), Body1762 (feature_tree), Body1763 (feature_tree), Body1764 (feature_tree), Body1765 (feature_tree), Body1766 (feature_tree), Body1767 (feature_tree), Body1768 (feature_tree), Body1769 (feature_tree), Body1770 (feature_tree), Body1771 (feature_tree), Body1772 (feature_tree), Body1773 (feature_tree), Body1774 (feature_tree), Body1775 (feature_tree), Body1776 (feature_tree), Body1777 (feature_tree), Body1778 (feature_tree), Body1779 (feature_tree), Body1780 (feature_tree), Body1781 (feature_tree), Body1782 (feature_tree), Body1783 (feature_tree), Body1784 (feature_tree), Body1785 (feature_tree), Body1786 (feature_tree), Body1787 (feature_tree), Body1788 (feature_tree), Body1789 (feature_tree), Body1790 (feature_tree), Body1791 (feature_tree), Body1792 (feature_tree), Body1793 (feature_tree), Body1794 (feature_tree), Body1795 (feature_tree), Body1796 (feature_tree), Body1797 (feature_tree), Body1798 (feature_tree), Body1799 (feature_tree), Body1800 (feature_tree), Body1801 (feature_tree), Body1802 (feature_tree), Body1803 (feature_tree), Body1804 (feature_tree), Body1805 (feature_tree), Body1806 (feature_tree), Body1807 (feature_tree), Body1808 (feature_tree), Body1809 (feature_tree), Body1810 (feature_tree), Body1811 (feature_tree), Body1812 (feature_tree), Body1813 (feature_tree), Body1814 (feature_tree), Body1815 (feature_tree), Body1816 (feature_tree)
feature tree (6070):
  other  "Твердое тело1"
  other  "Исправленная геометрия1"
  sketch  "3D эскиз1"
  sketch  "3D эскиз2"
  sketch  "3D эскиз3"
  sketch  "3D эскиз4"
  sketch  "3D эскиз5"
  sketch  "3D эскиз6"
  sketch  "3D эскиз7"
  sketch  "3D эскиз8"
  sketch  "3D эскиз9"
  sketch  "3D эскиз10"
  sketch  "3D эскиз11"
  sketch  "3D эскиз12"
  sketch  "3D эскиз13"
  sketch  "3D эскиз14"
  sketch  "3D эскиз15"
  sketch  "3D эскиз16"
  sketch  "3D эскиз17"
  sketch  "3D эскиз18"
  sketch  "3D эскиз19"
  sketch  "3D эскиз20"
  sketch  "3D эскиз21"
  sketch  "3D эскиз22"
  sketch  "3D эскиз23"
  sketch  "3D эскиз24"
  sketch  "3D эскиз25"
  sketch  "3D эскиз26"
  sketch  "3D эскиз27"
  sketch  "3D эскиз28"
  sketch  "3D эскиз29"
  sketch  "3D эскиз30"
  sketch  "3D эскиз31"
  sketch  "3D эскиз32"
  sketch  "3D эскиз33"
  sketch  "3D эскиз34"
  sketch  "3D эскиз35"
  sketch  "3D эскиз36"
  sketch  "3D эскиз37"
  sketch  "3D эскиз38"
  sketch  "3D эскиз39"
  sketch  "3D эскиз40"
  sketch  "3D эскиз41"
  sketch  "3D эскиз42"
  sketch  "3D эскиз43"
  sketch  "3D эскиз44"
  sketch  "3D эскиз45"
  sketch  "3D эскиз46"
  sketch  "3D эскиз47"
  sketch  "3D эскиз48"
  sketch  "3D эскиз49"
  sketch  "3D эскиз50"
  sketch  "3D эскиз51"
  sketch  "3D эскиз52"
  sketch  "3D эскиз53"
  sketch  "3D эскиз54"
  sketch  "3D эскиз55"
  sketch  "3D эскиз56"
  sketch  "3D эскиз57"
  sketch  "3D эскиз58"
  sketch  "3D эскиз59"
  sketch  "3D эскиз60"
  sketch  "3D эскиз61"
  sketch  "3D эскиз62"
  sketch  "3D эскиз63"
  sketch  "3D эскиз64"
  sketch  "3D эскиз65"
  sketch  "3D эскиз66"
  sketch  "3D эскиз67"
  sketch  "3D эскиз68"
  sketch  "3D эскиз69"
  sketch  "3D эскиз70"
  sketch  "3D эскиз71"
  sketch  "3D эскиз72"
  sketch  "3D эскиз73"
  sketch  "3D эскиз74"
  sketch  "3D эскиз75"
  sketch  "3D эскиз76"
  sketch  "3D эскиз77"
  sketch  "3D эскиз78"
  sketch  "3D эскиз79"
  sketch  "3D эскиз80"
  sketch  "3D эскиз81"
  sketch  "3D эскиз82"
  sketch  "3D эскиз83"
  sketch  "3D эскиз84"
  sketch  "3D эскиз85"
  sketch  "3D эскиз86"
  sketch  "3D эскиз87"
  sketch  "3D эскиз88"
  sketch  "3D эскиз89"
  sketch  "3D эскиз90"
  sketch  "3D эскиз91"
  sketch  "3D эскиз92"
  sketch  "3D эскиз93"
  sketch  "3D эскиз94"
  sketch  "3D эскиз95"
  sketch  "3D эскиз96"
  sketch  "3D эскиз97"
  sketch  "3D эскиз98"
  sketch  "3D эскиз99"
  sketch  "3D эскиз100"
  sketch  "3D эскиз101"
  sketch  "3D эскиз102"
  sketch  "3D эскиз103"
  sketch  "3D эскиз104"
  sketch  "3D эскиз105"
  sketch  "3D эскиз106"
  sketch  "3D эскиз107"
  sketch  "3D эскиз108"
  sketch  "3D эскиз109"
  sketch  "3D эскиз110"
  sketch  "3D эскиз111"
  sketch  "3D эскиз112"
  sketch  "3D эскиз113"
  sketch  "3D эскиз114"
  sketch  "3D эскиз115"
  sketch  "3D эскиз116"
  sketch  "3D эскиз117"
  sketch  "3D эскиз118"
  sketch  "3D эскиз119"
  sketch  "3D эскиз120"
  sketch  "3D эскиз121"
  sketch  "3D эскиз122"
  sketch  "3D эскиз123"
  sketch  "3D эскиз124"
  sketch  "3D эскиз125"
  sketch  "3D эскиз126"
  sketch  "3D эскиз127"
  sketch  "3D эскиз128"
  sketch  "3D эскиз129"
  sketch  "3D эскиз130"
  sketch  "3D эскиз131"
  sketch  "3D эскиз132"
  sketch  "3D эскиз133"
  sketch  "3D эскиз134"
  sketch  "3D эскиз135"
  sketch  "3D эскиз136"
  sketch  "3D эскиз137"
  sketch  "3D эскиз138"
  sketch  "3D эскиз139"
  sketch  "3D эскиз140"
  sketch  "3D эскиз141"
  sketch  "3D эскиз142"
  sketch  "3D эскиз143"
  sketch  "3D эскиз144"
  sketch  "3D эскиз145"
  sketch  "3D эскиз146"
  sketch  "3D эскиз147"
  sketch  "3D эскиз148"
  sketch  "3D эскиз149"
  sketch  "3D эскиз150"
  sketch  "3D эскиз151"
  sketch  "3D эскиз152"
  sketch  "3D эскиз153"
  sketch  "3D эскиз154"
  sketch  "3D эскиз155"
  sketch  "3D эскиз156"
  sketch  "3D эскиз157"
  sketch  "3D эскиз158"
  sketch  "3D эскиз159"
  sketch  "3D эскиз160"
  sketch  "3D эскиз161"
  sketch  "3D эскиз162"
  sketch  "3D эскиз163"
  sketch  "3D эскиз164"
  sketch  "3D эскиз165"
  sketch  "3D эскиз166"
  sketch  "3D эскиз167"
  sketch  "3D эскиз168"
  sketch  "3D эскиз169"
  sketch  "3D эскиз170"
  sketch  "3D эскиз171"
  sketch  "3D эскиз172"
  sketch  "3D эскиз173"
  sketch  "3D эскиз174"
  sketch  "3D эскиз175"
  sketch  "3D эскиз176"
  sketch  "3D эскиз177"
  sketch  "3D эскиз178"
  sketch  "3D эскиз179"
  sketch  "3D эскиз180"
  sketch  "3D эскиз181"
  sketch  "3D эскиз182"
  sketch  "3D эскиз183"
  sketch  "3D эскиз184"
  sketch  "3D эскиз185"
  sketch  "3D эскиз186"
  sketch  "3D эскиз187"
  sketch  "3D эскиз188"
  sketch  "3D эскиз189"
  sketch  "3D эскиз190"
  sketch  "3D эскиз191"
  sketch  "3D эскиз192"
  sketch  "3D эскиз193"
  sketch  "3D эскиз194"
  sketch  "3D эскиз195"
  sketch  "3D эскиз196"
  sketch  "3D эскиз197"
  sketch  "3D эскиз198"
  sketch  "3D эскиз199"
  sketch  "3D эскиз200"
  sketch  "3D эскиз201"
  sketch  "3D эскиз202"
  sketch  "3D эскиз203"
  sketch  "3D эскиз204"
  sketch  "3D эскиз205"
  sketch  "3D эскиз206"
  sketch  "3D эскиз207"
  sketch  "3D эскиз208"
  sketch  "3D эскиз209"
  sketch  "3D эскиз210"
  sketch  "3D эскиз211"
  sketch  "3D эскиз212"
  sketch  "3D эскиз213"
  sketch  "3D эскиз214"
  sketch  "3D эскиз215"
  sketch  "3D эскиз216"
  sketch  "3D эскиз217"
  sketch  "3D эскиз218"
  sketch  "3D эскиз219"
  sketch  "3D эскиз220"
  sketch  "3D эскиз221"
  sketch  "3D эскиз222"
  sketch  "3D эскиз223"
  sketch  "3D эскиз224"
  sketch  "3D эскиз225"
  sketch  "3D эскиз226"
  sketch  "3D эскиз227"
  sketch  "3D эскиз228"
  sketch  "3D эскиз229"
  sketch  "3D эскиз230"
  sketch  "3D эскиз231"
  sketch  "3D эскиз232"
  sketch  "3D эскиз233"
  sketch  "3D эскиз234"
  sketch  "3D эскиз235"
  sketch  "3D эскиз236"
  sketch  "3D эскиз237"
  sketch  "3D эскиз238"
  sketch  "3D эскиз239"
  sketch  "3D эскиз240"
  sketch  "3D эскиз241"
  sketch  "3D эскиз242"
  sketch  "3D эскиз243"
  sketch  "3D эскиз244"
  sketch  "3D эскиз245"
  sketch  "3D эскиз246"
  sketch  "3D эскиз247"
  sketch  "3D эскиз248"
  sketch  "3D эскиз249"
  sketch  "3D эскиз250"
  sketch  "3D эскиз251"
  sketch  "3D эскиз252"
  sketch  "3D эскиз253"
  sketch  "3D эскиз254"
  sketch  "3D эскиз255"
  sketch  "3D эскиз256"
  sketch  "3D эскиз257"
  sketch  "3D эскиз258"
  sketch  "3D эскиз259"
  sketch  "3D эскиз260"
  sketch  "3D эскиз261"
  sketch  "3D эскиз262"
  sketch  "3D эскиз263"
  sketch  "3D эскиз264"
  sketch  "3D эскиз265"
  sketch  "3D эскиз266"
  sketch  "3D эскиз267"
  sketch  "3D эскиз268"
  sketch  "3D эскиз269"
  sketch  "3D эскиз270"
  sketch  "3D эскиз271"
  sketch  "3D эскиз272"
  sketch  "3D эскиз273"
  sketch  "3D эскиз274"
  sketch  "3D эскиз275"
  sketch  "3D эскиз276"
  sketch  "3D эскиз277"
  sketch  "3D эскиз278"
  sketch  "3D эскиз279"
  sketch  "3D эскиз280"
  sketch  "3D эскиз281"
  sketch  "3D эскиз282"
  sketch  "3D эскиз283"
  sketch  "3D эскиз284"
  sketch  "3D эскиз285"
  sketch  "3D эскиз286"
  sketch  "3D эскиз287"
  sketch  "3D эскиз288"
  sketch  "3D эскиз289"
  sketch  "3D эскиз290"
  sketch  "3D эскиз291"
  sketch  "3D эскиз292"
  sketch  "3D эскиз293"
  sketch  "3D эскиз294"
  sketch  "3D эскиз295"
  sketch  "3D эскиз296"
  sketch  "3D эскиз297"
  sketch  "3D эскиз298"
  sketch  "3D эскиз299"
  sketch  "3D эскиз300"
  sketch  "3D эскиз301"
  sketch  "3D эскиз302"
  sketch  "3D эскиз303"
  sketch  "3D эскиз304"
  sketch  "3D эскиз305"
  sketch  "3D эскиз306"
  sketch  "3D эскиз307"
  sketch  "3D эскиз308"
  sketch  "3D эскиз309"
  sketch  "3D эскиз310"
  sketch  "3D эскиз311"
  sketch  "3D эскиз312"
  sketch  "3D эскиз313"
  sketch  "3D эскиз314"
  sketch  "3D эскиз315"
  sketch  "3D эскиз316"
  sketch  "3D эскиз317"
  sketch  "3D эскиз318"
  sketch  "3D эскиз319"
  sketch  "3D эскиз320"
  sketch  "3D эскиз321"
  sketch  "3D эскиз322"
  sketch  "3D эскиз323"
  sketch  "3D эскиз324"
  sketch  "3D эскиз325"
  sketch  "3D эскиз326"
  sketch  "3D эскиз327"
  sketch  "3D эскиз328"
  sketch  "3D эскиз329"
  sketch  "3D эскиз330"
  sketch  "3D эскиз331"
  sketch  "3D эскиз332"
  sketch  "3D эскиз333"
  sketch  "3D эскиз334"
  sketch  "3D эскиз335"
  sketch  "3D эскиз336"
  sketch  "3D эскиз337"
  sketch  "3D эскиз338"
  sketch  "3D эскиз339"
  sketch  "3D эскиз340"
  sketch  "3D эскиз341"
  sketch  "3D эскиз342"
  sketch  "3D эскиз343"
  sketch  "3D эскиз344"
  sketch  "3D эскиз345"
  sketch  "3D эскиз346"
  sketch  "3D эскиз347"
  sketch  "3D эскиз348"
  sketch  "3D эскиз349"
  sketch  "3D эскиз350"
  sketch  "3D эскиз351"
  sketch  "3D эскиз352"
  sketch  "3D эскиз353"
  sketch  "3D эскиз354"
  sketch  "3D эскиз355"
  sketch  "3D эскиз356"
  sketch  "3D эскиз357"
  sketch  "3D эскиз358"
  sketch  "3D эскиз359"
  sketch  "3D эскиз360"
  sketch  "3D эскиз361"
  sketch  "3D эскиз362"
  sketch  "3D эскиз363"
  sketch  "3D эскиз364"
  sketch  "3D эскиз365"
  sketch  "3D эскиз366"
  sketch  "3D эскиз367"
  sketch  "3D эскиз368"
  sketch  "3D эскиз369"
  sketch  "3D эскиз370"
  sketch  "3D эскиз371"
  sketch  "3D эскиз372"
  sketch  "3D эскиз373"
  sketch  "3D эскиз374"
  sketch  "3D эскиз375"
  sketch  "3D эскиз376"
  sketch  "3D эскиз377"
  sketch  "3D эскиз378"
  sketch  "3D эскиз379"
  sketch  "3D эскиз380"
  sketch  "3D эскиз381"
  sketch  "3D эскиз382"
  sketch  "3D эскиз383"
  sketch  "3D эскиз384"
  sketch  "3D эскиз385"
  sketch  "3D эскиз386"
  sketch  "3D эскиз387"
  sketch  "3D эскиз388"
  sketch  "3D эскиз389"
  sketch  "3D эскиз390"
  sketch  "3D эскиз391"
  sketch  "3D эскиз392"
  sketch  "3D эскиз393"
  sketch  "3D эскиз394"
  sketch  "3D эскиз395"
  sketch  "3D эскиз396"
  sketch  "3D эскиз397"
  sketch  "3D эскиз398"
  sketch  "3D эскиз399"
  sketch  "3D эскиз400"
  sketch  "3D эскиз401"
  sketch  "3D эскиз402"
  sketch  "3D эскиз403"
  sketch  "3D эскиз404"
  sketch  "3D эскиз405"
  sketch  "3D эскиз406"
  sketch  "3D эскиз407"
  sketch  "3D эскиз408"
  sketch  "3D эскиз409"
  sketch  "3D эскиз410"
  sketch  "3D эскиз411"
  sketch  "3D эскиз412"
  sketch  "3D эскиз413"
  sketch  "3D эскиз414"
  sketch  "3D эскиз415"
  sketch  "3D эскиз416"
  sketch  "3D эскиз417"
  sketch  "3D эскиз418"
  sketch  "3D эскиз419"
  sketch  "3D эскиз420"
  sketch  "3D эскиз421"
  sketch  "3D эскиз422"
  sketch  "3D эскиз423"
  sketch  "3D эскиз424"
  sketch  "3D эскиз425"
  sketch  "3D эскиз426"
  sketch  "3D эскиз427"
  sketch  "3D эскиз428"
  sketch  "3D эскиз429"
  sketch  "3D эскиз430"
  sketch  "3D эскиз431"
  sketch  "3D эскиз432"
  sketch  "3D эскиз433"
  sketch  "3D эскиз434"
  sketch  "3D эскиз435"
  sketch  "3D эскиз436"
  sketch  "3D эскиз437"
  sketch  "3D эскиз438"
  sketch  "3D эскиз439"
  sketch  "3D эскиз440"
  sketch  "3D эскиз441"
  sketch  "3D эскиз442"
  sketch  "3D эскиз443"
  sketch  "3D эскиз444"
  sketch  "3D эскиз445"
  sketch  "3D эскиз446"
  sketch  "3D эскиз447"
  sketch  "3D эскиз448"
  sketch  "3D эскиз449"
  sketch  "3D эскиз450"
  sketch  "3D эскиз451"
  sketch  "3D эскиз452"
  sketch  "3D эскиз453"
  sketch  "3D эскиз454"
  sketch  "3D эскиз455"
  sketch  "3D эскиз456"
  sketch  "3D эскиз457"
  sketch  "3D эскиз458"
  sketch  "3D эскиз459"
  sketch  "3D эскиз460"
  sketch  "3D эскиз461"
  sketch  "3D эскиз462"
  sketch  "3D эскиз463"
  sketch  "3D эскиз464"
  sketch  "3D эскиз465"
  sketch  "3D эскиз466"
  sketch  "3D эскиз467"
  sketch  "3D эскиз468"
  sketch  "3D эскиз469"
  sketch  "3D эскиз470"
  sketch  "3D эскиз471"
  sketch  "3D эскиз472"
  sketch  "3D эскиз473"
  sketch  "3D эскиз474"
  sketch  "3D эскиз475"
  sketch  "3D эскиз476"
  sketch  "3D эскиз477"
  sketch  "3D эскиз478"
  sketch  "3D эскиз479"
  sketch  "3D эскиз480"
  sketch  "3D эскиз481"
  sketch  "3D эскиз482"
  sketch  "3D эскиз483"
  sketch  "3D эскиз484"
  sketch  "3D эскиз485"
  sketch  "3D эскиз486"
  sketch  "3D эскиз487"
  sketch  "3D эскиз488"
  sketch  "3D эскиз489"
  sketch  "3D эскиз490"
  sketch  "3D эскиз491"
  sketch  "3D эскиз492"
  sketch  "3D эскиз493"
  sketch  "3D эскиз494"
  sketch  "3D эскиз495"
  sketch  "3D эскиз496"
  sketch  "3D эскиз497"
  sketch  "3D эскиз498"
  sketch  "3D эскиз499"
  sketch  "3D эскиз500"
  sketch  "3D эскиз501"
  sketch  "3D эскиз502"
  sketch  "3D эскиз503"
  sketch  "3D эскиз504"
  sketch  "3D эскиз505"
  sketch  "3D эскиз506"
  sketch  "3D эскиз507"
  sketch  "3D эскиз508"
  sketch  "3D эскиз509"
  sketch  "3D эскиз510"
  sketch  "3D эскиз511"
  sketch  "3D эскиз512"
  sketch  "3D эскиз513"
  sketch  "3D эскиз514"
  sketch  "3D эскиз515"
  sketch  "3D эскиз516"
  sketch  "3D эскиз517"
  sketch  "3D эскиз518"
  sketch  "3D эскиз519"
  sketch  "3D эскиз520"
  sketch  "3D эскиз521"
  sketch  "3D эскиз522"
  sketch  "3D эскиз523"
  sketch  "3D эскиз524"
  sketch  "3D эскиз525"
  sketch  "3D эскиз526"
  sketch  "3D эскиз527"
  sketch  "3D эскиз528"
  sketch  "3D эскиз529"
  sketch  "3D эскиз530"
  sketch  "3D эскиз531"
  sketch  "3D эскиз532"
  sketch  "3D эскиз533"
  sketch  "3D эскиз534"
  sketch  "3D эскиз535"
  sketch  "3D эскиз536"
  sketch  "3D эскиз537"
  sketch  "3D эскиз538"
  sketch  "3D эскиз539"
  sketch  "3D эскиз540"
  sketch  "3D эскиз541"
  sketch  "3D эскиз542"
  sketch  "3D эскиз543"
  sketch  "3D эскиз544"
  sketch  "3D эскиз545"
  sketch  "3D эскиз546"
  sketch  "3D эскиз547"
  sketch  "3D эскиз548"
  sketch  "3D эскиз549"
  sketch  "3D эскиз550"
  sketch  "3D эскиз551"
  sketch  "3D эскиз552"
  sketch  "3D эскиз553"
  sketch  "3D эскиз554"
  sketch  "3D эскиз555"
  sketch  "3D эскиз556"
  sketch  "3D эскиз557"
  sketch  "3D эскиз558"
  sketch  "3D эскиз559"
  sketch  "3D эскиз560"
  sketch  "3D эскиз561"
  sketch  "3D эскиз562"
  sketch  "3D эскиз563"
  sketch  "3D эскиз564"
  sketch  "3D эскиз565"
  sketch  "3D эскиз566"
  sketch  "3D эскиз567"
  sketch  "3D эскиз568"
  sketch  "3D эскиз569"
  sketch  "3D эскиз570"
  sketch  "3D эскиз571"
  sketch  "3D эскиз572"
  sketch  "3D эскиз573"
  sketch  "3D эскиз574"
  sketch  "3D эскиз575"
  sketch  "3D эскиз576"
  sketch  "3D эскиз577"
  sketch  "3D эскиз578"
  sketch  "3D эскиз579"
  sketch  "3D эскиз580"
  sketch  "3D эскиз581"
  sketch  "3D эскиз582"
  sketch  "3D эскиз583"
  sketch  "3D эскиз584"
  sketch  "3D эскиз585"
  sketch  "3D эскиз586"
  sketch  "3D эскиз587"
  sketch  "3D эскиз588"
  sketch  "3D эскиз589"
  sketch  "3D эскиз590"
  sketch  "3D эскиз591"
  sketch  "3D эскиз592"
  sketch  "3D эскиз593"
  sketch  "3D эскиз594"
  sketch  "3D эскиз595"
  sketch  "3D эскиз596"
  sketch  "3D эскиз597"
  sketch  "3D эскиз598"
  sketch  "3D эскиз599"
  sketch  "3D эскиз600"
  sketch  "3D эскиз601"
  sketch  "3D эскиз602"
  sketch  "3D эскиз603"
  sketch  "3D эскиз604"
  sketch  "3D эскиз605"
  sketch  "3D эскиз606"
  sketch  "3D эскиз607"
  sketch  "3D эскиз608"
  sketch  "3D эскиз609"
  sketch  "3D эскиз610"
  sketch  "3D эскиз611"
  sketch  "3D эскиз612"
  sketch  "3D эскиз613"
  sketch  "3D эскиз614"
  sketch  "3D эскиз615"
  sketch  "3D эскиз616"
  sketch  "3D эскиз617"
  sketch  "3D эскиз618"
  sketch  "3D эскиз619"
  sketch  "3D эскиз620"
  sketch  "3D эскиз621"
  sketch  "3D эскиз622"
  sketch  "3D эскиз623"
  sketch  "3D эскиз624"
  sketch  "3D эскиз625"
  sketch  "3D эскиз626"
  sketch  "3D эскиз627"
  sketch  "3D эскиз628"
  sketch  "3D эскиз629"
  sketch  "3D эскиз630"
  sketch  "3D эскиз631"
  sketch  "3D эскиз632"
  sketch  "3D эскиз633"
  sketch  "3D эскиз634"
  sketch  "3D эскиз635"
  sketch  "3D эскиз636"
  sketch  "3D эскиз637"
  sketch  "3D эскиз638"
  sketch  "3D эскиз639"
  sketch  "3D эскиз640"
  sketch  "3D эскиз641"
  sketch  "3D эскиз642"
  sketch  "3D эскиз643"
  sketch  "3D эскиз644"
  sketch  "3D эскиз645"
  sketch  "3D эскиз646"
  sketch  "3D эскиз647"
  sketch  "3D эскиз648"
  sketch  "3D эскиз649"
  sketch  "3D эскиз650"
  sketch  "3D эскиз651"
  sketch  "3D эскиз652"
  sketch  "3D эскиз653"
  sketch  "3D эскиз654"
  sketch  "3D эскиз655"
  sketch  "3D эскиз656"
  sketch  "3D эскиз657"
  sketch  "3D эскиз658"
  sketch  "3D эскиз659"
  sketch  "3D эскиз660"
  sketch  "3D эскиз661"
  sketch  "3D эскиз662"
  sketch  "3D эскиз663"
  sketch  "3D эскиз664"
  sketch  "3D эскиз665"
  sketch  "3D эскиз666"
  sketch  "3D эскиз667"
  sketch  "3D эскиз668"
  sketch  "3D эскиз669"
  sketch  "3D эскиз670"
  sketch  "3D эскиз671"
  sketch  "3D эскиз672"
  sketch  "3D эскиз673"
  sketch  "3D эскиз674"
  sketch  "3D эскиз675"
  sketch  "3D эскиз676"
  sketch  "3D эскиз677"
  sketch  "3D эскиз678"
  sketch  "3D эскиз679"
  sketch  "3D эскиз680"
  sketch  "3D эскиз681"
  sketch  "3D эскиз682"
  sketch  "3D эскиз683"
  sketch  "3D эскиз684"
  sketch  "3D эскиз685"
  sketch  "3D эскиз686"
  sketch  "3D эскиз687"
  sketch  "3D эскиз688"
  sketch  "3D эскиз689"
  sketch  "3D эскиз690"
  sketch  "3D эскиз691"
  sketch  "3D эскиз692"
  sketch  "3D эскиз693"
  sketch  "3D эскиз694"
  sketch  "3D эскиз695"
  sketch  "3D эскиз696"
  sketch  "3D эскиз697"
  sketch  "3D эскиз698"
  sketch  "3D эскиз699"
  sketch  "3D эскиз700"
  sketch  "3D эскиз701"
  sketch  "3D эскиз702"
  sketch  "3D эскиз703"
  sketch  "3D эскиз704"
  sketch  "3D эскиз705"
  sketch  "3D эскиз706"
  sketch  "3D эскиз707"
  sketch  "3D эскиз708"
  sketch  "3D эскиз709"
  sketch  "3D эскиз710"
  sketch  "3D эскиз711"
  sketch  "3D эскиз712"
  sketch  "3D эскиз713"
  sketch  "3D эскиз714"
  sketch  "3D эскиз715"
  sketch  "3D эскиз716"
  sketch  "3D эскиз717"
  sketch  "3D эскиз718"
  sketch  "3D эскиз719"
  sketch  "3D эскиз720"
  sketch  "3D эскиз721"
  sketch  "3D эскиз722"
  sketch  "3D эскиз723"
  sketch  "3D эскиз724"
  sketch  "3D эскиз725"
  sketch  "3D эскиз726"
  sketch  "3D эскиз727"
  sketch  "3D эскиз728"
  sketch  "3D эскиз729"
  sketch  "3D эскиз730"
  sketch  "3D эскиз731"
  sketch  "3D эскиз732"
  sketch  "3D эскиз733"
  sketch  "3D эскиз734"
  sketch  "3D эскиз735"
  sketch  "3D эскиз736"
  sketch  "3D эскиз737"
  sketch  "3D эскиз738"
  sketch  "3D эскиз739"
  sketch  "3D эскиз740"
  sketch  "3D эскиз741"
  sketch  "3D эскиз742"
  sketch  "3D эскиз743"
  sketch  "3D эскиз744"
  sketch  "3D эскиз745"
  sketch  "3D эскиз746"
  sketch  "3D эскиз747"
  sketch  "3D эскиз748"
  sketch  "3D эскиз749"
  sketch  "3D эскиз750"
  sketch  "3D эскиз751"
  sketch  "3D эскиз752"
  sketch  "3D эскиз753"
  sketch  "3D эскиз754"
  sketch  "3D эскиз755"
  sketch  "3D эскиз756"
  sketch  "3D эскиз757"
  sketch  "3D эскиз758"
  sketch  "3D эскиз759"
  sketch  "3D эскиз760"
  sketch  "3D эскиз761"
  sketch  "3D эскиз762"
  sketch  "3D эскиз763"
  sketch  "3D эскиз764"
  sketch  "3D эскиз765"
  sketch  "3D эскиз766"
  sketch  "3D эскиз767"
  sketch  "3D эскиз768"
  sketch  "3D эскиз769"
  sketch  "3D эскиз770"
  sketch  "3D эскиз771"
  sketch  "3D эскиз772"
  sketch  "3D эскиз773"
  sketch  "3D эскиз774"
  sketch  "3D эскиз775"
  sketch  "3D эскиз776"
  sketch  "3D эскиз777"
  sketch  "3D эскиз778"
  sketch  "3D эскиз779"
  sketch  "3D эскиз780"
  sketch  "3D эскиз781"
  sketch  "3D эскиз782"
  sketch  "3D эскиз783"
  sketch  "3D эскиз784"
  sketch  "3D эскиз785"
  sketch  "3D эскиз786"
  sketch  "3D эскиз787"
  sketch  "3D эскиз788"
  sketch  "3D эскиз789"
  sketch  "3D эскиз790"
  sketch  "3D эскиз791"
  sketch  "3D эскиз792"
  sketch  "3D эскиз793"
  sketch  "3D эскиз794"
  sketch  "3D эскиз795"
  sketch  "3D эскиз796"
  sketch  "3D эскиз797"
  sketch  "3D эскиз798"
  sketch  "3D эскиз799"
  sketch  "3D эскиз800"
  sketch  "3D эскиз801"
  sketch  "3D эскиз802"
  sketch  "3D эскиз803"
  sketch  "3D эскиз804"
  sketch  "3D эскиз805"
  sketch  "3D эскиз806"
  sketch  "3D эскиз807"
  sketch  "3D эскиз808"
  sketch  "3D эскиз809"
  sketch  "3D эскиз810"
  sketch  "3D эскиз811"
  sketch  "3D эскиз812"
  sketch  "3D эскиз813"
  sketch  "3D эскиз814"
  sketch  "3D эскиз815"
  sketch  "3D эскиз816"
  sketch  "3D эскиз817"
  sketch  "3D эскиз818"
  sketch  "3D эскиз819"
  sketch  "3D эскиз820"
  sketch  "3D эскиз821"
  sketch  "3D эскиз822"
  sketch  "3D эскиз823"
  sketch  "3D эскиз824"
  sketch  "3D эскиз825"
  sketch  "3D эскиз826"
  sketch  "3D эскиз827"
  sketch  "3D эскиз828"
  sketch  "3D эскиз829"
  sketch  "3D эскиз830"
  sketch  "3D эскиз831"
  sketch  "3D эскиз832"
  sketch  "3D эскиз833"
  sketch  "3D эскиз834"
  sketch  "3D эскиз835"
  sketch  "3D эскиз836"
  sketch  "3D эскиз837"
  sketch  "3D эскиз838"
  sketch  "3D эскиз839"
  sketch  "3D эскиз840"
  sketch  "3D эскиз841"
  sketch  "3D эскиз842"
  sketch  "3D эскиз843"
  sketch  "3D эскиз844"
  sketch  "3D эскиз845"
  sketch  "3D эскиз846"
  sketch  "3D эскиз847"
  sketch  "3D эскиз848"
  sketch  "3D эскиз849"
  sketch  "3D эскиз850"
  sketch  "3D эскиз851"
  sketch  "3D эскиз852"
  sketch  "3D эскиз853"
  sketch  "3D эскиз854"
  sketch  "3D эскиз855"
  sketch  "3D эскиз856"
  sketch  "3D эскиз857"
  sketch  "3D эскиз858"
  sketch  "3D эскиз859"
  sketch  "3D эскиз860"
  sketch  "3D эскиз861"
  sketch  "3D эскиз862"
  sketch  "3D эскиз863"
  sketch  "3D эскиз864"
  sketch  "3D эскиз865"
  sketch  "3D эскиз866"
  sketch  "3D эскиз867"
  sketch  "3D эскиз868"
  sketch  "3D эскиз869"
  sketch  "3D эскиз870"
  sketch  "3D эскиз871"
  sketch  "3D эскиз872"
  sketch  "3D эскиз873"
  sketch  "3D эскиз874"
  sketch  "3D эскиз875"
  sketch  "3D эскиз876"
  sketch  "3D эскиз877"
  sketch  "3D эскиз878"
  sketch  "3D эскиз879"
  sketch  "3D эскиз880"
  sketch  "3D эскиз881"
  sketch  "3D эскиз882"
  sketch  "3D эскиз883"
  sketch  "3D эскиз884"
  sketch  "3D эскиз885"
  sketch  "3D эскиз886"
  sketch  "3D эскиз887"
  sketch  "3D эскиз888"
  sketch  "3D эскиз889"
  sketch  "3D эскиз890"
  sketch  "3D эскиз891"
  sketch  "3D эскиз892"
  sketch  "3D эскиз893"
  sketch  "3D эскиз894"
  sketch  "3D эскиз895"
  sketch  "3D эскиз896"
  sketch  "3D эскиз897"
  sketch  "3D эскиз898"
  sketch  "3D эскиз899"
  sketch  "3D эскиз900"
  sketch  "3D эскиз901"
  sketch  "3D эскиз902"
  sketch  "3D эскиз903"
  sketch  "3D эскиз904"
  sketch  "3D эскиз905"
  sketch  "3D эскиз906"
  sketch  "3D эскиз907"
  sketch  "3D эскиз908"
  sketch  "3D эскиз909"
  sketch  "3D эскиз910"
  sketch  "3D эскиз911"
  sketch  "3D эскиз912"
  sketch  "3D эскиз913"
  sketch  "3D эскиз914"
  sketch  "3D эскиз915"
  sketch  "3D эскиз916"
  sketch  "3D эскиз917"
  sketch  "3D эскиз918"
  sketch  "3D эскиз919"
  sketch  "3D эскиз920"
  sketch  "3D эскиз921"
  sketch  "3D эскиз922"
  sketch  "3D эскиз923"
  sketch  "3D эскиз924"
  sketch  "3D эскиз925"
  sketch  "3D эскиз926"
  sketch  "3D эскиз927"
  sketch  "3D эскиз928"
  sketch  "3D эскиз929"
  sketch  "3D эскиз930"
  sketch  "3D эскиз931"
  sketch  "3D эскиз932"
  sketch  "3D эскиз933"
  sketch  "3D эскиз934"
  sketch  "3D эскиз935"
  sketch  "3D эскиз936"
  sketch  "3D эскиз937"
  sketch  "3D эскиз938"
  sketch  "3D эскиз939"
  sketch  "3D эскиз940"
  sketch  "3D эскиз941"
  sketch  "3D эскиз942"
  sketch  "3D эскиз943"
  sketch  "3D эскиз944"
  sketch  "3D эскиз945"
  sketch  "3D эскиз946"
  sketch  "3D эскиз947"
  sketch  "3D эскиз948"
  sketch  "3D эскиз949"
  sketch  "3D эскиз950"
  sketch  "3D эскиз951"
  sketch  "3D эскиз952"
  sketch  "3D эскиз953"
  sketch  "3D эскиз954"
  sketch  "3D эскиз955"
  sketch  "3D эскиз956"
  sketch  "3D эскиз957"
  sketch  "3D эскиз958"
  sketch  "3D эскиз959"
  sketch  "3D эскиз960"
  sketch  "3D эскиз961"
  sketch  "3D эскиз962"
  sketch  "3D эскиз963"
  sketch  "3D эскиз964"
  sketch  "3D эскиз965"
  sketch  "3D эскиз966"
  sketch  "3D эскиз967"
  sketch  "3D эскиз968"
  sketch  "3D эскиз969"
  sketch  "3D эскиз970"
  sketch  "3D эскиз971"
  sketch  "3D эскиз972"
  sketch  "3D эскиз973"
  sketch  "3D эскиз974"
  sketch  "3D эскиз975"
  sketch  "3D эскиз976"
  sketch  "3D эскиз977"
  sketch  "3D эскиз978"
  sketch  "3D эскиз979"
  sketch  "3D эскиз980"
  sketch  "3D эскиз981"
  sketch  "3D эскиз982"
  sketch  "3D эскиз983"
  sketch  "3D эскиз984"
  sketch  "3D эскиз985"
  sketch  "3D эскиз986"
  sketch  "3D эскиз987"
  sketch  "3D эскиз988"
  sketch  "3D эскиз989"
  sketch  "3D эскиз990"
  sketch  "3D эскиз991"
  sketch  "3D эскиз992"
  sketch  "3D эскиз993"
  sketch  "3D эскиз994"
  sketch  "3D эскиз995"
  sketch  "3D эскиз996"
  sketch  "3D эскиз997"
  sketch  "3D эскиз998"
  sketch  "3D эскиз999"
  sketch  "3D эскиз1000"
  sketch  "3D эскиз1001"
  sketch  "3D эскиз1002"
  sketch  "3D эскиз1003"
  sketch  "3D эскиз1004"
  sketch  "3D эскиз1005"
  sketch  "3D эскиз1006"
  sketch  "3D эскиз1007"
  sketch  "3D эскиз1008"
  sketch  "3D эскиз1009"
  sketch  "3D эскиз1010"
  sketch  "3D эскиз1011"
  sketch  "3D эскиз1012"
  sketch  "3D эскиз1013"
  sketch  "3D эскиз1014"
  sketch  "3D эскиз1015"
  sketch  "3D эскиз1016"
  sketch  "3D эскиз1017"
  sketch  "3D эскиз1018"
  sketch  "3D эскиз1019"
  sketch  "3D эскиз1020"
  sketch  "3D эскиз1021"
  sketch  "3D эскиз1022"
  sketch  "3D эскиз1023"
  sketch  "3D эскиз1024"
  sketch  "3D эскиз1025"
  sketch  "3D эскиз1026"
  sketch  "3D эскиз1027"
  sketch  "3D эскиз1028"
  sketch  "3D эскиз1029"
  sketch  "3D эскиз1030"
  sketch  "3D эскиз1031"
  sketch  "3D эскиз1032"
  sketch  "3D эскиз1033"
  sketch  "3D эскиз1034"
  sketch  "3D эскиз1035"
  sketch  "3D эскиз1036"
  sketch  "3D эскиз1037"
  sketch  "3D эскиз1038"
  sketch  "3D эскиз1039"
  sketch  "3D эскиз1040"
  sketch  "3D эскиз1041"
  sketch  "3D эскиз1042"
  sketch  "3D эскиз1043"
  sketch  "3D эскиз1044"
  sketch  "3D эскиз1045"
  sketch  "3D эскиз1046"
  sketch  "3D эскиз1047"
  sketch  "3D эскиз1048"
  sketch  "3D эскиз1049"
  sketch  "3D эскиз1050"
  sketch  "3D эскиз1051"
  sketch  "3D эскиз1052"
  sketch  "3D эскиз1053"
  sketch  "3D эскиз1054"
  sketch  "3D эскиз1055"
  sketch  "3D эскиз1056"
  sketch  "3D эскиз1057"
  sketch  "3D эскиз1058"
  sketch  "3D эскиз1059"
  sketch  "3D эскиз1060"
  sketch  "3D эскиз1061"
  sketch  "3D эскиз1062"
  sketch  "3D эскиз1063"
  sketch  "3D эскиз1064"
  sketch  "3D эскиз1065"
  sketch  "3D эскиз1066"
  sketch  "3D эскиз1067"
  sketch  "3D эскиз1068"
  sketch  "3D эскиз1069"
  sketch  "3D эскиз1070"
  sketch  "3D эскиз1071"
  sketch  "3D эскиз1072"
  sketch  "3D эскиз1073"
  sketch  "3D эскиз1074"
  sketch  "3D эскиз1075"
  sketch  "3D эскиз1076"
  sketch  "3D эскиз1077"
  sketch  "3D эскиз1078"
  sketch  "3D эскиз1079"
  sketch  "3D эскиз1080"
  sketch  "3D эскиз1081"
  sketch  "3D эскиз1082"
  sketch  "3D эскиз1083"
  sketch  "3D эскиз1084"
  sketch  "3D эскиз1085"
  sketch  "3D эскиз1086"
  sketch  "3D эскиз1087"
  sketch  "3D эскиз1088"
  sketch  "3D эскиз1089"
  sketch  "3D эскиз1090"
  sketch  "3D эскиз1091"
  sketch  "3D эскиз1092"
  sketch  "3D эскиз1093"
  sketch  "3D эскиз1094"
  sketch  "3D эскиз1095"
  sketch  "3D эскиз1096"
  sketch  "3D эскиз1097"
  sketch  "3D эскиз1098"
  sketch  "3D эскиз1099"
  sketch  "3D эскиз1100"
  sketch  "3D эскиз1101"
  sketch  "3D эскиз1102"
  sketch  "3D эскиз1103"
  sketch  "3D эскиз1104"
  sketch  "3D эскиз1105"
  sketch  "3D эскиз1106"
  sketch  "3D эскиз1107"
  sketch  "3D эскиз1108"
  sketch  "3D эскиз1109"
  sketch  "3D эскиз1110"
  sketch  "3D эскиз1111"
  sketch  "3D эскиз1112"
  sketch  "3D эскиз1113"
  sketch  "3D эскиз1114"
  sketch  "3D эскиз1115"
  sketch  "3D эскиз1116"
  sketch  "3D эскиз1117"
  sketch  "3D эскиз1118"
  sketch  "3D эскиз1119"
  sketch  "3D эскиз1120"
  sketch  "3D эскиз1121"
  sketch  "3D эскиз1122"
  sketch  "3D эскиз1123"
  sketch  "3D эскиз1124"
  sketch  "3D эскиз1125"
  sketch  "3D эскиз1126"
  sketch  "3D эскиз1127"
  sketch  "3D эскиз1128"
  sketch  "3D эскиз1129"
  sketch  "3D эскиз1130"
  sketch  "3D эскиз1131"
  sketch  "3D эскиз1132"
  sketch  "3D эскиз1133"
  sketch  "3D эскиз1134"
  sketch  "3D эскиз1135"
  sketch  "3D эскиз1136"
  sketch  "3D эскиз1137"
  sketch  "3D эскиз1138"
  sketch  "3D эскиз1139"
  sketch  "3D эскиз1140"
  sketch  "3D эскиз1141"
  sketch  "3D эскиз1142"
  sketch  "3D эскиз1143"
  sketch  "3D эскиз1144"
  sketch  "3D эскиз1145"
  sketch  "3D эскиз1146"
  sketch  "3D эскиз1147"
  sketch  "3D эскиз1148"
  sketch  "3D эскиз1149"
  sketch  "3D эскиз1150"
  sketch  "3D эскиз1151"
  sketch  "3D эскиз1152"
  sketch  "3D эскиз1153"
  sketch  "3D эскиз1154"
  sketch  "3D эскиз1155"
  sketch  "3D эскиз1156"
  sketch  "3D эскиз1157"
  sketch  "3D эскиз1158"
  sketch  "3D эскиз1159"
  sketch  "3D эскиз1160"
  sketch  "3D эскиз1161"
  sketch  "3D эскиз1162"
  sketch  "3D эскиз1163"
  sketch  "3D эскиз1164"
  sketch  "3D эскиз1165"
  sketch  "3D эскиз1166"
  sketch  "3D эскиз1167"
  sketch  "3D эскиз1168"
  sketch  "3D эскиз1169"
  sketch  "3D эскиз1170"
  sketch  "3D эскиз1171"
  sketch  "3D эскиз1172"
  sketch  "3D эскиз1173"
  sketch  "3D эскиз1174"
  sketch  "3D эскиз1175"
  sketch  "3D эскиз1176"
  sketch  "3D эскиз1177"
  sketch  "3D эскиз1178"
  sketch  "3D эскиз1179"
  sketch  "3D эскиз1180"
  sketch  "3D эскиз1181"
  sketch  "3D эскиз1182"
  sketch  "3D эскиз1183"
  sketch  "3D эскиз1184"
  sketch  "3D эскиз1185"
  sketch  "3D эскиз1186"
  sketch  "3D эскиз1187"
  sketch  "3D эскиз1188"
  sketch  "3D эскиз1189"
  sketch  "3D эскиз1190"
  sketch  "3D эскиз1191"
  sketch  "3D эскиз1192"
  sketch  "3D эскиз1193"
  sketch  "3D эскиз1194"
  sketch  "3D эскиз1195"
  sketch  "3D эскиз1196"
  sketch  "3D эскиз1197"
  sketch  "3D эскиз1198"
  sketch  "3D эскиз1199"
  sketch  "3D эскиз1200"
  sketch  "3D эскиз1201"
  sketch  "3D эскиз1202"
  sketch  "3D эскиз1203"
  sketch  "3D эскиз1204"
  sketch  "3D эскиз1205"
  sketch  "3D эскиз1206"
  sketch  "3D эскиз1207"
  sketch  "3D эскиз1208"
  sketch  "3D эскиз1209"
  sketch  "3D эскиз1210"
  sketch  "3D эскиз1211"
  sketch  "3D эскиз1212"
  sketch  "3D эскиз1213"
  sketch  "3D эскиз1214"
  sketch  "3D эскиз1215"
  sketch  "3D эскиз1216"
  sketch  "3D эскиз1217"
  sketch  "3D эскиз1218"
  sketch  "3D эскиз1219"
  sketch  "3D эскиз1220"
  sketch  "3D эскиз1221"
  sketch  "3D эскиз1222"
  sketch  "3D эскиз1223"
  sketch  "3D эскиз1224"
  sketch  "3D эскиз1225"
  sketch  "3D эскиз1226"
  sketch  "3D эскиз1227"
  sketch  "3D эскиз1228"
  sketch  "3D эскиз1229"
  sketch  "3D эскиз1230"
  sketch  "3D эскиз1231"
  sketch  "3D эскиз1232"
  sketch  "3D эскиз1233"
  sketch  "3D эскиз1234"
  sketch  "3D эскиз1235"
  sketch  "3D эскиз1236"
  sketch  "3D эскиз1237"
  sketch  "3D эскиз1238"
  sketch  "3D эскиз1239"
  sketch  "3D эскиз1240"
  sketch  "3D эскиз1241"
  sketch  "3D эскиз1242"
  sketch  "3D эскиз1243"
  sketch  "3D эскиз1244"
  sketch  "3D эскиз1245"
  sketch  "3D эскиз1246"
  sketch  "3D эскиз1247"
  sketch  "3D эскиз1248"
  sketch  "3D эскиз1249"
  sketch  "3D эскиз1250"
  sketch  "3D эскиз1251"
  sketch  "3D эскиз1252"
  sketch  "3D эскиз1253"
  sketch  "3D эскиз1254"
  sketch  "3D эскиз1255"
  sketch  "3D эскиз1256"
  sketch  "3D эскиз1257"
  sketch  "3D эскиз1258"
  sketch  "3D эскиз1259"
  sketch  "3D эскиз1260"
  sketch  "3D эскиз1261"
  sketch  "3D эскиз1262"
  sketch  "3D эскиз1263"
  sketch  "3D эскиз1264"
  sketch  "3D эскиз1265"
  sketch  "3D эскиз1266"
  sketch  "3D эскиз1267"
  sketch  "3D эскиз1268"
  sketch  "3D эскиз1269"
  sketch  "3D эскиз1270"
  sketch  "3D эскиз1271"
  sketch  "3D эскиз1272"
  sketch  "3D эскиз1273"
  sketch  "3D эскиз1274"
  sketch  "3D эскиз1275"
  sketch  "3D эскиз1276"
  sketch  "3D эскиз1277"
  sketch  "3D эскиз1278"
  sketch  "3D эскиз1279"
  sketch  "3D эскиз1280"
  sketch  "3D эскиз1281"
  sketch  "3D эскиз1282"
  sketch  "3D эскиз1283"
  sketch  "3D эскиз1284"
  sketch  "3D эскиз1285"
  sketch  "3D эскиз1286"
  sketch  "3D эскиз1287"
  sketch  "3D эскиз1288"
  sketch  "3D эскиз1289"
  sketch  "3D эскиз1290"
  sketch  "3D эскиз1291"
  sketch  "3D эскиз1292"
  sketch  "3D эскиз1293"
  sketch  "3D эскиз1294"
  sketch  "3D эскиз1295"
  sketch  "3D эскиз1296"
  sketch  "3D эскиз1297"
  sketch  "3D эскиз1298"
  sketch  "3D эскиз1299"
  sketch  "3D эскиз1300"
  sketch  "3D эскиз1301"
  sketch  "3D эскиз1302"
  sketch  "3D эскиз1303"
  sketch  "3D эскиз1304"
  sketch  "3D эскиз1305"
  sketch  "3D эскиз1306"
  sketch  "3D эскиз1307"
  sketch  "3D эскиз1308"
  sketch  "3D эскиз1309"
  sketch  "3D эскиз1310"
  sketch  "3D эскиз1311"
  sketch  "3D эскиз1312"
  sketch  "3D эскиз1313"
  sketch  "3D эскиз1314"
  sketch  "3D эскиз1315"
  sketch  "3D эскиз1316"
  sketch  "3D эскиз1317"
  sketch  "3D эскиз1318"
  sketch  "3D эскиз1319"
  sketch  "3D эскиз1320"
  sketch  "3D эскиз1321"
  sketch  "3D эскиз1322"
  sketch  "3D эскиз1323"
  sketch  "3D эскиз1324"
  sketch  "3D эскиз1325"
  sketch  "3D эскиз1326"
  sketch  "3D эскиз1327"
  sketch  "3D эскиз1328"
  sketch  "3D эскиз1329"
  sketch  "3D эскиз1330"
  sketch  "3D эскиз1331"
  sketch  "3D эскиз1332"
  sketch  "3D эскиз1333"
  sketch  "3D эскиз1334"
  sketch  "3D эскиз1335"
  sketch  "3D эскиз1336"
  sketch  "3D эскиз1337"
  sketch  "3D эскиз1338"
  sketch  "3D эскиз1339"
  sketch  "3D эскиз1340"
  sketch  "3D эскиз1341"
  sketch  "3D эскиз1342"
  sketch  "3D эскиз1343"
  sketch  "3D эскиз1344"
  sketch  "3D эскиз1345"
  sketch  "3D эскиз1346"
  sketch  "3D эскиз1347"
  sketch  "3D эскиз1348"
  sketch  "3D эскиз1349"
  sketch  "3D эскиз1350"
  sketch  "3D эскиз1351"
  sketch  "3D эскиз1352"
  sketch  "3D эскиз1353"
  sketch  "3D эскиз1354"
  sketch  "3D эскиз1355"
  sketch  "3D эскиз1356"
  sketch  "3D эскиз1357"
  sketch  "3D эскиз1358"
  sketch  "3D эскиз1359"
  sketch  "3D эскиз1360"
  sketch  "3D эскиз1361"
  sketch  "3D эскиз1362"
  sketch  "3D эскиз1363"
  sketch  "3D эскиз1364"
  sketch  "3D эскиз1365"
  sketch  "3D эскиз1366"
  sketch  "3D эскиз1367"
  sketch  "3D эскиз1368"
  sketch  "3D эскиз1369"
  sketch  "3D эскиз1370"
  sketch  "3D эскиз1371"
  sketch  "3D эскиз1372"
  sketch  "3D эскиз1373"
  sketch  "3D эскиз1374"
  sketch  "3D эскиз1375"
  sketch  "3D эскиз1376"
  sketch  "3D эскиз1377"
  sketch  "3D эскиз1378"
  sketch  "3D эскиз1379"
  sketch  "3D эскиз1380"
  sketch  "3D эскиз1381"
  sketch  "3D эскиз1382"
  sketch  "3D эскиз1383"
  sketch  "3D эскиз1384"
  sketch  "3D эскиз1385"
  sketch  "3D эскиз1386"
  sketch  "3D эскиз1387"
  sketch  "3D эскиз1388"
  sketch  "3D эскиз1389"
  sketch  "3D эскиз1390"
  sketch  "3D эскиз1391"
  sketch  "3D эскиз1392"
  sketch  "3D эскиз1393"
  sketch  "3D эскиз1394"
  sketch  "3D эскиз1395"
  sketch  "3D эскиз1396"
  sketch  "3D эскиз1397"
  sketch  "3D эскиз1398"
  sketch  "3D эскиз1399"
  sketch  "3D эскиз1400"
  sketch  "3D эскиз1401"
  sketch  "3D эскиз1402"
  sketch  "3D эскиз1403"
  sketch  "3D эскиз1404"
  sketch  "3D эскиз1405"
  sketch  "3D эскиз1406"
  sketch  "3D эскиз1407"
  sketch  "3D эскиз1408"
  sketch  "3D эскиз1409"
  sketch  "3D эскиз1410"
  sketch  "3D эскиз1411"
  sketch  "3D эскиз1412"
  sketch  "3D эскиз1413"
  sketch  "3D эскиз1414"
  sketch  "3D эскиз1415"
  sketch  "3D эскиз1416"
  sketch  "3D эскиз1417"
  sketch  "3D эскиз1418"
  sketch  "3D эскиз1419"
  sketch  "3D эскиз1420"
  sketch  "3D эскиз1421"
  sketch  "3D эскиз1422"
  sketch  "3D эскиз1423"
  sketch  "3D эскиз1424"
  sketch  "3D эскиз1425"
  sketch  "3D эскиз1426"
  sketch  "3D эскиз1427"
  sketch  "3D эскиз1428"
  sketch  "3D эскиз1429"
  sketch  "3D эскиз1430"
  sketch  "3D эскиз1431"
  sketch  "3D эскиз1432"
  sketch  "3D эскиз1433"
  sketch  "3D эскиз1434"
  sketch  "3D эскиз1435"
  sketch  "3D эскиз1436"
  sketch  "3D эскиз1437"
  sketch  "3D эскиз1438"
  sketch  "3D эскиз1439"
  sketch  "3D эскиз1440"
  sketch  "3D эскиз1441"
  sketch  "3D эскиз1442"
  sketch  "3D эскиз1443"
  sketch  "3D эскиз1444"
  sketch  "3D эскиз1445"
  sketch  "3D эскиз1446"
  sketch  "3D эскиз1447"
  sketch  "3D эскиз1448"
  sketch  "3D эскиз1449"
  sketch  "3D эскиз1450"
  sketch  "3D эскиз1451"
  sketch  "3D эскиз1452"
  sketch  "3D эскиз1453"
  sketch  "3D эскиз1454"
  sketch  "3D эскиз1455"
  sketch  "3D эскиз1456"
  sketch  "3D эскиз1457"
  sketch  "3D эскиз1458"
  sketch  "3D эскиз1459"
  sketch  "3D эскиз1460"
  sketch  "3D эскиз1461"
  sketch  "3D эскиз1462"
  sketch  "3D эскиз1463"
  sketch  "3D эскиз1464"
  sketch  "3D эскиз1465"
  sketch  "3D эскиз1466"
  sketch  "3D эскиз1467"
  sketch  "3D эскиз1468"
  sketch  "3D эскиз1469"
  sketch  "3D эскиз1470"
  sketch  "3D эскиз1471"
  sketch  "3D эскиз1472"
  sketch  "3D эскиз1473"
  sketch  "3D эскиз1474"
  sketch  "3D эскиз1475"
  sketch  "3D эскиз1476"
  sketch  "3D эскиз1477"
  sketch  "3D эскиз1478"
  sketch  "3D эскиз1479"
  sketch  "3D эскиз1480"
  sketch  "3D эскиз1481"
  sketch  "3D эскиз1482"
  sketch  "3D эскиз1483"
  sketch  "3D эскиз1484"
  sketch  "3D эскиз1485"
  sketch  "3D эскиз1486"
  sketch  "3D эскиз1487"
  sketch  "3D эскиз1488"
  sketch  "3D эскиз1489"
  sketch  "3D эскиз1490"
  sketch  "3D эскиз1491"
  sketch  "3D эскиз1492"
  sketch  "3D эскиз1493"
  sketch  "3D эскиз1494"
  sketch  "3D эскиз1495"
  sketch  "3D эскиз1496"
  sketch  "3D эскиз1497"
  sketch  "3D эскиз1498"
  sketch  "3D эскиз1499"
  sketch  "3D эскиз1500"
  sketch  "3D эскиз1501"
  sketch  "3D эскиз1502"
  sketch  "3D эскиз1503"
  sketch  "3D эскиз1504"
  sketch  "3D эскиз1505"
  sketch  "3D эскиз1506"
  sketch  "3D эскиз1507"
  sketch  "3D эскиз1508"
  sketch  "3D эскиз1509"
  sketch  "3D эскиз1510"
  sketch  "3D эскиз1511"
  sketch  "3D эскиз1512"
  sketch  "3D эскиз1513"
  sketch  "3D эскиз1514"
  sketch  "3D эскиз1515"
  sketch  "3D эскиз1516"
  sketch  "3D эскиз1517"
  sketch  "3D эскиз1518"
  sketch  "3D эскиз1519"
  sketch  "3D эскиз1520"
  sketch  "3D эскиз1521"
  sketch  "3D эскиз1522"
  sketch  "3D эскиз1523"
  sketch  "3D эскиз1524"
  sketch  "3D эскиз1525"
  sketch  "3D эскиз1526"
  sketch  "3D эскиз1527"
  sketch  "3D эскиз1528"
  sketch  "3D эскиз1529"
  sketch  "3D эскиз1530"
  sketch  "3D эскиз1531"
  sketch  "3D эскиз1532"
  sketch  "3D эскиз1533"
  sketch  "3D эскиз1534"
  sketch  "3D эскиз1535"
  sketch  "3D эскиз1536"
  sketch  "3D эскиз1537"
  sketch  "3D эскиз1538"
  sketch  "3D эскиз1539"
  sketch  "3D эскиз1540"
  sketch  "3D эскиз1541"
  sketch  "3D эскиз1542"
  sketch  "3D эскиз1543"
  sketch  "3D эскиз1544"
  sketch  "3D эскиз1545"
  sketch  "3D эскиз1546"
  sketch  "3D эскиз1547"
  sketch  "3D эскиз1548"
  sketch  "3D эскиз1549"
  sketch  "3D эскиз1550"
  sketch  "3D эскиз1551"
  sketch  "3D эскиз1552"
  sketch  "3D эскиз1553"
  sketch  "3D эскиз1554"
  sketch  "3D эскиз1555"
  sketch  "3D эскиз1556"
  sketch  "3D эскиз1557"
  sketch  "3D эскиз1558"
  sketch  "3D эскиз1559"
  sketch  "3D эскиз1560"
  sketch  "3D эскиз1561"
  sketch  "3D эскиз1562"
  sketch  "3D эскиз1563"
  sketch  "3D эскиз1564"
  sketch  "3D эскиз1565"
  sketch  "3D эскиз1566"
  sketch  "3D эскиз1567"
  sketch  "3D эскиз1568"
  sketch  "3D эскиз1569"
  sketch  "3D эскиз1570"
  sketch  "3D эскиз1571"
  sketch  "3D эскиз1572"
  sketch  "3D эскиз1573"
  sketch  "3D эскиз1574"
  sketch  "3D эскиз1575"
  sketch  "3D эскиз1576"
  sketch  "3D эскиз1577"
  sketch  "3D эскиз1578"
  sketch  "3D эскиз1579"
  sketch  "3D эскиз1580"
  sketch  "3D эскиз1581"
  sketch  "3D эскиз1582"
  sketch  "3D эскиз1583"
  sketch  "3D эскиз1584"
  sketch  "3D эскиз1585"
  sketch  "3D эскиз1586"
  sketch  "3D эскиз1587"
  sketch  "3D эскиз1588"
  sketch  "3D эскиз1589"
  sketch  "3D эскиз1590"
  sketch  "3D эскиз1591"
  sketch  "3D эскиз1592"
  sketch  "3D эскиз1593"
  sketch  "3D эскиз1594"
  sketch  "3D эскиз1595"
  sketch  "3D эскиз1596"
  sketch  "3D эскиз1597"
  sketch  "3D эскиз1598"
  sketch  "3D эскиз1599"
  sketch  "3D эскиз1600"
  sketch  "3D эскиз1601"
  sketch  "3D эскиз1602"
  sketch  "3D эскиз1603"
  sketch  "3D эскиз1604"
  sketch  "3D эскиз1605"
  sketch  "3D эскиз1606"
  sketch  "3D эскиз1607"
  sketch  "3D эскиз1608"
  sketch  "3D эскиз1609"
  sketch  "3D эскиз1610"
  sketch  "3D эскиз1611"
  sketch  "3D эскиз1612"
  sketch  "3D эскиз1613"
  sketch  "3D эскиз1614"
  sketch  "3D эскиз1615"
  sketch  "3D эскиз1616"
  sketch  "3D эскиз1617"
  sketch  "3D эскиз1618"
  sketch  "3D эскиз1619"
  sketch  "3D эскиз1620"
  sketch  "3D эскиз1621"
  sketch  "3D эскиз1622"
  sketch  "3D эскиз1623"
  sketch  "3D эскиз1624"
  sketch  "3D эскиз1625"
  sketch  "3D эскиз1626"
  sketch  "3D эскиз1627"
  sketch  "3D эскиз1628"
  sketch  "3D эскиз1629"
  sketch  "3D эскиз1630"
  sketch  "3D эскиз1631"
  sketch  "3D эскиз1632"
  sketch  "3D эскиз1633"
  sketch  "3D эскиз1634"
  sketch  "3D эскиз1635"
  sketch  "3D эскиз1636"
  sketch  "3D эскиз1637"
  sketch  "3D эскиз1638"
  sketch  "3D эскиз1639"
  sketch  "3D эскиз1640"
  sketch  "3D эскиз1641"
  sketch  "3D эскиз1642"
  sketch  "3D эскиз1643"
  sketch  "3D эскиз1644"
  sketch  "3D эскиз1645"
  sketch  "3D эскиз1646"
  sketch  "3D эскиз1647"
  sketch  "3D эскиз1648"
  sketch  "3D эскиз1649"
  sketch  "3D эскиз1650"
  sketch  "3D эскиз1651"
  sketch  "3D эскиз1652"
  sketch  "3D эскиз1653"
  sketch  "3D эскиз1654"
  sketch  "3D эскиз1655"
  sketch  "3D эскиз1656"
  sketch  "3D эскиз1657"
  sketch  "3D эскиз1658"
  sketch  "3D эскиз1659"
  sketch  "3D эскиз1660"
  sketch  "3D эскиз1661"
  sketch  "3D эскиз1662"
  sketch  "3D эскиз1663"
  sketch  "3D эскиз1664"
  sketch  "3D эскиз1665"
  sketch  "3D эскиз1666"
  sketch  "3D эскиз1667"
  sketch  "3D эскиз1668"
  sketch  "3D эскиз1669"
  sketch  "3D эскиз1670"
  sketch  "3D эскиз1671"
  sketch  "3D эскиз1672"
  sketch  "3D эскиз1673"
  sketch  "3D эскиз1674"
  sketch  "3D эскиз1675"
  sketch  "3D эскиз1676"
  sketch  "3D эскиз1677"
  sketch  "3D эскиз1678"
  sketch  "3D эскиз1679"
  sketch  "3D эскиз1680"
  sketch  "3D эскиз1681"
  sketch  "3D эскиз1682"
  sketch  "3D эскиз1683"
  sketch  "3D эскиз1684"
  sketch  "3D эскиз1685"
  sketch  "3D эскиз1686"
  sketch  "3D эскиз1687"
  sketch  "3D эскиз1688"
  sketch  "3D эскиз1689"
  sketch  "3D эскиз1690"
  sketch  "3D эскиз1691"
  sketch  "3D эскиз1692"
  sketch  "3D эскиз1693"
  sketch  "3D эскиз1694"
  sketch  "3D эскиз1695"
  sketch  "3D эскиз1696"
  sketch  "3D эскиз1697"
  sketch  "3D эскиз1698"
  sketch  "3D эскиз1699"
  sketch  "3D эскиз1700"
  sketch  "3D эскиз1701"
  sketch  "3D эскиз1702"
  sketch  "3D эскиз1703"
  sketch  "3D эскиз1704"
  sketch  "3D эскиз1705"
  sketch  "3D эскиз1706"
  sketch  "3D эскиз1707"
  sketch  "3D эскиз1708"
  sketch  "3D эскиз1709"
  sketch  "3D эскиз1710"
  sketch  "3D эскиз1711"
  sketch  "3D эскиз1712"
  sketch  "3D эскиз1713"
  sketch  "3D эскиз1714"
  sketch  "3D эскиз1715"
  sketch  "3D эскиз1716"
  sketch  "3D эскиз1717"
  sketch  "3D эскиз1718"
  sketch  "3D эскиз1719"
  sketch  "3D эскиз1720"
  sketch  "3D эскиз1721"
  sketch  "3D эскиз1722"
  sketch  "3D эскиз1723"
  sketch  "3D эскиз1724"
  sketch  "3D эскиз1725"
  sketch  "3D эскиз1726"
  sketch  "3D эскиз1727"
  sketch  "3D эскиз1728"
  sketch  "3D эскиз1729"
  sketch  "3D эскиз1730"
  sketch  "3D эскиз1731"
  sketch  "3D эскиз1732"
  sketch  "3D эскиз1733"
  sketch  "3D эскиз1734"
  sketch  "3D эскиз1735"
  sketch  "3D эскиз1736"
  sketch  "3D эскиз1737"
  sketch  "3D эскиз1738"
  sketch  "3D эскиз1739"
  sketch  "3D эскиз1740"
  sketch  "3D эскиз1741"
  sketch  "3D эскиз1742"
  sketch  "3D эскиз1743"
  sketch  "3D эскиз1744"
  sketch  "3D эскиз1745"
  sketch  "3D эскиз1746"
  sketch  "3D эскиз1747"
  sketch  "3D эскиз1748"
  sketch  "3D эскиз1749"
  sketch  "3D эскиз1750"
  sketch  "3D эскиз1751"
  sketch  "3D эскиз1752"
  sketch  "3D эскиз1753"
  sketch  "3D эскиз1754"
  sketch  "3D эскиз1755"
  sketch  "3D эскиз1756"
  sketch  "3D эскиз1757"
  sketch  "3D эскиз1758"
  sketch  "3D эскиз1759"
  sketch  "3D эскиз1760"
  sketch  "3D эскиз1761"
  sketch  "3D эскиз1762"
  sketch  "3D эскиз1763"
  sketch  "3D эскиз1764"
  sketch  "3D эскиз1765"
  sketch  "3D эскиз1766"
  sketch  "3D эскиз1767"
  sketch  "3D эскиз1768"
  sketch  "3D эскиз1769"
  sketch  "3D эскиз1770"
  sketch  "3D эскиз1771"
  sketch  "3D эскиз1772"
  sketch  "3D эскиз1773"
  sketch  "3D эскиз1774"
  sketch  "3D эскиз1775"
  sketch  "3D эскиз1776"
  sketch  "3D эскиз1777"
  sketch  "3D эскиз1778"
  sketch  "3D эскиз1779"
  sketch  "3D эскиз1780"
  sketch  "3D эскиз1781"
  sketch  "3D эскиз1782"
  sketch  "3D эскиз1783"
  sketch  "3D эскиз1784"
  sketch  "3D эскиз1785"
  sketch  "3D эскиз1786"
  sketch  "3D эскиз1787"
  sketch  "3D эскиз1788"
  sketch  "3D эскиз1789"
  sketch  "3D эскиз1790"
  sketch  "3D эскиз1791"
  sketch  "3D эскиз1792"
  sketch  "3D эскиз1793"
  sketch  "3D эскиз1794"
  sketch  "3D эскиз1795"
  sketch  "3D эскиз1796"
  sketch  "3D эскиз1797"
  sketch  "3D эскиз1798"
  sketch  "3D эскиз1799"
  sketch  "3D эскиз1800"
  sketch  "3D эскиз1801"
  sketch  "3D эскиз1802"
  sketch  "3D эскиз1803"
  sketch  "3D эскиз1804"
  sketch  "3D эскиз1805"
  sketch  "3D эскиз1806"
  sketch  "3D эскиз1807"
  sketch  "3D эскиз1808"
  sketch  "3D эскиз1809"
  sketch  "3D эскиз1810"
  sketch  "3D эскиз1811"
  sketch  "3D эскиз1812"
  sketch  "3D эскиз1813"
  sketch  "3D эскиз1814"
  sketch  "3D эскиз1815"
  sketch  "3D эскиз1816"
  sketch  "3D эскиз1817"
  sketch  "3D эскиз1818"
  sketch  "3D эскиз1819"
  sketch  "3D эскиз1820"
  sketch  "3D эскиз1821"
  sketch  "3D эскиз1822"
  sketch  "3D эскиз1823"
  sketch  "3D эскиз1824"
  sketch  "3D эскиз1825"
  sketch  "3D эскиз1826"
  sketch  "3D эскиз1827"
  sketch  "3D эскиз1828"
  sketch  "3D эскиз1829"
  sketch  "3D эскиз1830"
  sketch  "3D эскиз1831"
  sketch  "3D эскиз1832"
  sketch  "3D эскиз1833"
  sketch  "3D эскиз1834"
  sketch  "3D эскиз1835"
  sketch  "3D эскиз1836"
  sketch  "3D эскиз1837"
  sketch  "3D эскиз1838"
  sketch  "3D эскиз1839"
  sketch  "3D эскиз1840"
  sketch  "3D эскиз1841"
  sketch  "3D эскиз1842"
  sketch  "3D эскиз1843"
  sketch  "3D эскиз1844"
  sketch  "3D эскиз1845"
  sketch  "3D эскиз1846"
  sketch  "3D эскиз1847"
  sketch  "3D эскиз1848"
  sketch  "3D эскиз1849"
  sketch  "3D эскиз1850"
  sketch  "3D эскиз1851"
  sketch  "3D эскиз1852"
  sketch  "3D эскиз1853"
  sketch  "3D эскиз1854"
  sketch  "3D эскиз1855"
  sketch  "3D эскиз1856"
  sketch  "3D эскиз1857"
  sketch  "3D эскиз1858"
  sketch  "3D эскиз1859"
  sketch  "3D эскиз1860"
  sketch  "3D эскиз1861"
  sketch  "3D эскиз1862"
  sketch  "3D эскиз1863"
  sketch  "3D эскиз1864"
  sketch  "3D эскиз1865"
  sketch  "3D эскиз1866"
  sketch  "3D эскиз1867"
  sketch  "3D эскиз1868"
  sketch  "3D эскиз1869"
  sketch  "3D эскиз1870"
  sketch  "3D эскиз1871"
  sketch  "3D эскиз1872"
  sketch  "3D эскиз1873"
  sketch  "3D эскиз1874"
  sketch  "3D эскиз1875"
  sketch  "3D эскиз1876"
  sketch  "3D эскиз1877"
  sketch  "3D эскиз1878"
  sketch  "3D эскиз1879"
  sketch  "3D эскиз1880"
  sketch  "3D эскиз1881"
  sketch  "3D эскиз1882"
  sketch  "3D эскиз1883"
  sketch  "3D эскиз1884"
  sketch  "3D эскиз1885"
  sketch  "3D эскиз1886"
  sketch  "3D эскиз1887"
  sketch  "3D эскиз1888"
  sketch  "3D эскиз1889"
  sketch  "3D эскиз1890"
  sketch  "3D эскиз1891"
  sketch  "3D эскиз1892"
  sketch  "3D эскиз1893"
  sketch  "3D эскиз1894"
  sketch  "3D эскиз1895"
  sketch  "3D эскиз1896"
  sketch  "3D эскиз1897"
  sketch  "3D эскиз1898"
  sketch  "3D эскиз1899"
  sketch  "3D эскиз1900"
  sketch  "3D эскиз1901"
  sketch  "3D эскиз1902"
  sketch  "3D эскиз1903"
  sketch  "3D эскиз1904"
  sketch  "3D эскиз1905"
  sketch  "3D эскиз1906"
  sketch  "3D эскиз1907"
  sketch  "3D эскиз1908"
  sketch  "3D эскиз1909"
  sketch  "3D эскиз1910"
  sketch  "3D эскиз1911"
  sketch  "3D эскиз1912"
  sketch  "3D эскиз1913"
  sketch  "3D эскиз1914"
  sketch  "3D эскиз1915"
  sketch  "3D эскиз1916"
  sketch  "3D эскиз1917"
  sketch  "3D эскиз1918"
  sketch  "3D эскиз1919"
  sketch  "3D эскиз1920"
  sketch  "3D эскиз1921"
  sketch  "3D эскиз1922"
  sketch  "3D эскиз1923"
  sketch  "3D эскиз1924"
  sketch  "3D эскиз1925"
  sketch  "3D эскиз1926"
  sketch  "3D эскиз1927"
  sketch  "3D эскиз1928"
  sketch  "3D эскиз1929"
  sketch  "3D эскиз1930"
  sketch  "3D эскиз1931"
  sketch  "3D эскиз1932"
  sketch  "3D эскиз1933"
  sketch  "3D эскиз1934"
  sketch  "3D эскиз1935"
  sketch  "3D эскиз1936"
  sketch  "3D эскиз1937"
  sketch  "3D эскиз1938"
  sketch  "3D эскиз1939"
  sketch  "3D эскиз1940"
  sketch  "3D эскиз1941"
  sketch  "3D эскиз1942"
  sketch  "3D эскиз1943"
  sketch  "3D эскиз1944"
  sketch  "3D эскиз1945"
  sketch  "3D эскиз1946"
  sketch  "3D эскиз1947"
  sketch  "3D эскиз1948"
  sketch  "3D эскиз1949"
  sketch  "3D эскиз1950"
  sketch  "3D эскиз1951"
  sketch  "3D эскиз1952"
  sketch  "3D эскиз1953"
  sketch  "3D эскиз1954"
  sketch  "3D эскиз1955"
  sketch  "3D эскиз1956"
  sketch  "3D эскиз1957"
  sketch  "3D эскиз1958"
  sketch  "3D эскиз1959"
  sketch  "3D эскиз1960"
  sketch  "3D эскиз1961"
  sketch  "3D эскиз1962"
  sketch  "3D эскиз1963"
  sketch  "3D эскиз1964"
  sketch  "3D эскиз1965"
  sketch  "3D эскиз1966"
  sketch  "3D эскиз1967"
  sketch  "3D эскиз1968"
  sketch  "3D эскиз1969"
  sketch  "3D эскиз1970"
  sketch  "3D эскиз1971"
  sketch  "3D эскиз1972"
  sketch  "3D эскиз1973"
  sketch  "3D эскиз1974"
  sketch  "3D эскиз1975"
  sketch  "3D эскиз1976"
  sketch  "3D эскиз1977"
  sketch  "3D эскиз1978"
  sketch  "3D эскиз1979"
  sketch  "3D эскиз1980"
  sketch  "3D эскиз1981"
  sketch  "3D эскиз1982"
  sketch  "3D эскиз1983"
  sketch  "3D эскиз1984"
  sketch  "3D эскиз1985"
  sketch  "3D эскиз1986"
  sketch  "3D эскиз1987"
  sketch  "3D эскиз1988"
  sketch  "3D эскиз1989"
  sketch  "3D эскиз1990"
  sketch  "3D эскиз1991"
  sketch  "3D эскиз1992"
  sketch  "3D эскиз1993"
  sketch  "3D эскиз1994"
  sketch  "3D эскиз1995"
  sketch  "3D эскиз1996"
  sketch  "3D эскиз1997"
  sketch  "3D эскиз1998"
  sketch  "3D эскиз1999"
  sketch  "3D эскиз2000"
  sketch  "3D эскиз2001"
  sketch  "3D эскиз2002"
  sketch  "3D эскиз2003"
  sketch  "3D эскиз2004"
  sketch  "3D эскиз2005"
  sketch  "3D эскиз2006"
  sketch  "3D эскиз2007"
  sketch  "3D эскиз2008"
  sketch  "3D эскиз2009"
  sketch  "3D эскиз2010"
  sketch  "3D эскиз2011"
  sketch  "3D эскиз2012"
  sketch  "3D эскиз2013"
  sketch  "3D эскиз2014"
  sketch  "3D эскиз2015"
  sketch  "3D эскиз2016"
  sketch  "3D эскиз2017"
  sketch  "3D эскиз2018"
  sketch  "3D эскиз2019"
  sketch  "3D эскиз2020"
  sketch  "3D эскиз2021"
  sketch  "3D эскиз2022"
  sketch  "3D эскиз2023"
  sketch  "3D эскиз2024"
  sketch  "3D эскиз2025"
  sketch  "3D эскиз2026"
  sketch  "3D эскиз2027"
  sketch  "3D эскиз2028"
  sketch  "3D эскиз2029"
  sketch  "3D эскиз2030"
  sketch  "3D эскиз2031"
  sketch  "3D эскиз2032"
  sketch  "3D эскиз2033"
  sketch  "3D эскиз2034"
  sketch  "3D эскиз2035"
  sketch  "3D эскиз2036"
  sketch  "3D эскиз2037"
  sketch  "3D эскиз2038"
  sketch  "3D эскиз2039"
  sketch  "3D эскиз2040"
  sketch  "3D эскиз2041"
  sketch  "3D эскиз2042"
  sketch  "3D эскиз2043"
  sketch  "3D эскиз2044"
  sketch  "3D эскиз2045"
  sketch  "3D эскиз2046"
  sketch  "3D эскиз2047"
  sketch  "3D эскиз2048"
  sketch  "3D эскиз2049"
  sketch  "3D эскиз2050"
  sketch  "3D эскиз2051"
  sketch  "3D эскиз2052"
  sketch  "3D эскиз2053"
  sketch  "3D эскиз2054"
  sketch  "3D эскиз2055"
  sketch  "3D эскиз2056"
  sketch  "3D эскиз2057"
  sketch  "3D эскиз2058"
  sketch  "3D эскиз2059"
  sketch  "3D эскиз2060"
  sketch  "3D эскиз2061"
  sketch  "3D эскиз2062"
  sketch  "3D эскиз2063"
  sketch  "3D эскиз2064"
  sketch  "3D эскиз2065"
  sketch  "3D эскиз2066"
  sketch  "3D эскиз2067"
  sketch  "3D эскиз2068"
  sketch  "3D эскиз2069"
  sketch  "3D эскиз2070"
  sketch  "3D эскиз2071"
  sketch  "3D эскиз2072"
  sketch  "3D эскиз2073"
  sketch  "3D эскиз2074"
  sketch  "3D эскиз2075"
  sketch  "3D эскиз2076"
  sketch  "3D эскиз2077"
  sketch  "3D эскиз2078"
  sketch  "3D эскиз2079"
  sketch  "3D эскиз2080"
  sketch  "3D эскиз2081"
  sketch  "3D эскиз2082"
  sketch  "3D эскиз2083"
  sketch  "3D эскиз2084"
  sketch  "3D эскиз2085"
  sketch  "3D эскиз2086"
  sketch  "3D эскиз2087"
  sketch  "3D эскиз2088"
  sketch  "3D эскиз2089"
  sketch  "3D эскиз2090"
  sketch  "3D эскиз2091"
  sketch  "3D эскиз2092"
  sketch  "3D эскиз2093"
  sketch  "3D эскиз2094"
  sketch  "3D эскиз2095"
  sketch  "3D эскиз2096"
  sketch  "3D эскиз2097"
  sketch  "3D эскиз2098"
  sketch  "3D эскиз2099"
  sketch  "3D эскиз2100"
  sketch  "3D эскиз2101"
  sketch  "3D эскиз2102"
  sketch  "3D эскиз2103"
  sketch  "3D эскиз2104"
  sketch  "3D эскиз2105"
  sketch  "3D эскиз2106"
  sketch  "3D эскиз2107"
  sketch  "3D эскиз2108"
  sketch  "3D эскиз2109"
  sketch  "3D эскиз2110"
  sketch  "3D эскиз2111"
  sketch  "3D эскиз2112"
  sketch  "3D эскиз2113"
  sketch  "3D эскиз2114"
  sketch  "3D эскиз2115"
  sketch  "3D эскиз2116"
  sketch  "3D эскиз2117"
  sketch  "3D эскиз2118"
  sketch  "3D эскиз2119"
  sketch  "3D эскиз2120"
  sketch  "3D эскиз2121"
  sketch  "3D эскиз2122"
  sketch  "3D эскиз2123"
  sketch  "3D эскиз2124"
  sketch  "3D эскиз2125"
  sketch  "3D эскиз2126"
  sketch  "3D эскиз2127"
  sketch  "3D эскиз2128"
  sketch  "3D эскиз2129"
  sketch  "3D эскиз2130"
  sketch  "3D эскиз2131"
  sketch  "3D эскиз2132"
  sketch  "3D эскиз2133"
  sketch  "3D эскиз2134"
  sketch  "3D эскиз2135"
  sketch  "3D эскиз2136"
  sketch  "3D эскиз2137"
  sketch  "3D эскиз2138"
  sketch  "3D эскиз2139"
  sketch  "3D эскиз2140"
  sketch  "3D эскиз2141"
  sketch  "3D эскиз2142"
  sketch  "3D эскиз2143"
  sketch  "3D эскиз2144"
  sketch  "3D эскиз2145"
  sketch  "3D эскиз2146"
  sketch  "3D эскиз2147"
  sketch  "3D эскиз2148"
  sketch  "3D эскиз2149"
  sketch  "3D эскиз2150"
  sketch  "3D эскиз2151"
  sketch  "3D эскиз2152"
  sketch  "3D эскиз2153"
  sketch  "3D эскиз2154"
  sketch  "3D эскиз2155"
  sketch  "3D эскиз2156"
  sketch  "3D эскиз2157"
  sketch  "3D эскиз2158"
  sketch  "3D эскиз2159"
  sketch  "3D эскиз2160"
  sketch  "3D эскиз2161"
  sketch  "3D эскиз2162"
  sketch  "3D эскиз2163"
  sketch  "3D эскиз2164"
  sketch  "3D эскиз2165"
  sketch  "3D эскиз2166"
  sketch  "3D эскиз2167"
  sketch  "3D эскиз2168"
  sketch  "3D эскиз2169"
  sketch  "3D эскиз2170"
  sketch  "3D эскиз2171"
  sketch  "3D эскиз2172"
  sketch  "3D эскиз2173"
  sketch  "3D эскиз2174"
  sketch  "3D эскиз2175"
  sketch  "3D эскиз2176"
  sketch  "3D эскиз2177"
  sketch  "3D эскиз2178"
  sketch  "3D эскиз2179"
  sketch  "3D эскиз2180"
  sketch  "3D эскиз2181"
  sketch  "3D эскиз2182"
  sketch  "3D эскиз2183"
  sketch  "3D эскиз2184"
  sketch  "3D эскиз2185"
  sketch  "3D эскиз2186"
  sketch  "3D эскиз2187"
  sketch  "3D эскиз2188"
  sketch  "3D эскиз2189"
  sketch  "3D эскиз2190"
  sketch  "3D эскиз2191"
  sketch  "3D эскиз2192"
  sketch  "3D эскиз2193"
  sketch  "3D эскиз2194"
  sketch  "3D эскиз2195"
  sketch  "3D эскиз2196"
  sketch  "3D эскиз2197"
  sketch  "3D эскиз2198"
  sketch  "3D эскиз2199"
  sketch  "3D эскиз2200"
  sketch  "3D эскиз2201"
  sketch  "3D эскиз2202"
  sketch  "3D эскиз2203"
  sketch  "3D эскиз2204"
  sketch  "3D эскиз2205"
  sketch  "3D эскиз2206"
  sketch  "3D эскиз2207"
  sketch  "3D эскиз2208"
  sketch  "3D эскиз2209"
  sketch  "3D эскиз2210"
  sketch  "3D эскиз2211"
  sketch  "3D эскиз2212"
  sketch  "3D эскиз2213"
  sketch  "3D эскиз2214"
  sketch  "3D эскиз2215"
  sketch  "3D эскиз2216"
  sketch  "3D эскиз2217"
  sketch  "3D эскиз2218"
  sketch  "3D эскиз2219"
  sketch  "3D эскиз2220"
  sketch  "3D эскиз2221"
  sketch  "3D эскиз2222"
  sketch  "3D эскиз2223"
  sketch  "3D эскиз2224"
  sketch  "3D эскиз2225"
  sketch  "3D эскиз2226"
  sketch  "3D эскиз2227"
  sketch  "3D эскиз2228"
  sketch  "3D эскиз2229"
  sketch  "3D эскиз2230"
  sketch  "3D эскиз2231"
  sketch  "3D эскиз2232"
  sketch  "3D эскиз2233"
  sketch  "3D эскиз2234"
  sketch  "3D эскиз2235"
  sketch  "3D эскиз2236"
  sketch  "3D эскиз2237"
  sketch  "3D эскиз2238"
  sketch  "3D эскиз2239"
  sketch  "3D эскиз2240"
  sketch  "3D эскиз2241"
  sketch  "3D эскиз2242"
  sketch  "3D эскиз2243"
  sketch  "3D эскиз2244"
  sketch  "3D эскиз2245"
  sketch  "3D эскиз2246"
  sketch  "3D эскиз2247"
  sketch  "3D эскиз2248"
  sketch  "3D эскиз2249"
  sketch  "3D эскиз2250"
  sketch  "3D эскиз2251"
  sketch  "3D эскиз2252"
  sketch  "3D эскиз2253"
  sketch  "3D эскиз2254"
  sketch  "3D эскиз2255"
  sketch  "3D эскиз2256"
  sketch  "3D эскиз2257"
  sketch  "3D эскиз2258"
  sketch  "3D эскиз2259"
  sketch  "3D эскиз2260"
  sketch  "3D эскиз2261"
  sketch  "3D эскиз2262"
  sketch  "3D эскиз2263"
  sketch  "3D эскиз2264"
  sketch  "3D эскиз2265"
  sketch  "3D эскиз2266"
  sketch  "3D эскиз2267"
  sketch  "3D эскиз2268"
  sketch  "3D эскиз2269"
  sketch  "3D эскиз2270"
  sketch  "3D эскиз2271"
  sketch  "3D эскиз2272"
  sketch  "3D эскиз2273"
  sketch  "3D эскиз2274"
  sketch  "3D эскиз2275"
  sketch  "3D эскиз2276"
  sketch  "3D эскиз2277"
  sketch  "3D эскиз2278"
  sketch  "3D эскиз2279"
  sketch  "3D эскиз2280"
  sketch  "3D эскиз2281"
  sketch  "3D эскиз2282"
  sketch  "3D эскиз2283"
  sketch  "3D эскиз2284"
  sketch  "3D эскиз2285"
  sketch  "3D эскиз2286"
  sketch  "3D эскиз2287"
  sketch  "3D эскиз2288"
  sketch  "3D эскиз2289"
  sketch  "3D эскиз2290"
  sketch  "3D эскиз2291"
  sketch  "3D эскиз2292"
  sketch  "3D эскиз2293"
  sketch  "3D эскиз2294"
  sketch  "3D эскиз2295"
  sketch  "3D эскиз2296"
  sketch  "3D эскиз2297"
  sketch  "3D эскиз2298"
  sketch  "3D эскиз2299"
  sketch  "3D эскиз2300"
  sketch  "3D эскиз2301"
  sketch  "3D эскиз2302"
  sketch  "3D эскиз2303"
  sketch  "3D эскиз2304"
  sketch  "3D эскиз2305"
  sketch  "3D эскиз2306"
  sketch  "3D эскиз2307"
  sketch  "3D эскиз2308"
  sketch  "3D эскиз2309"
  sketch  "3D эскиз2310"
  sketch  "3D эскиз2311"
  sketch  "3D эскиз2312"
  sketch  "3D эскиз2313"
  sketch  "3D эскиз2314"
  sketch  "3D эскиз2315"
  sketch  "3D эскиз2316"
  sketch  "3D эскиз2317"
  sketch  "3D эскиз2318"
  sketch  "3D эскиз2319"
  sketch  "3D эскиз2320"
  sketch  "3D эскиз2321"
  sketch  "3D эскиз2322"
  sketch  "3D эскиз2323"
  sketch  "3D эскиз2324"
  sketch  "3D эскиз2325"
  sketch  "3D эскиз2326"
  sketch  "3D эскиз2327"
  sketch  "3D эскиз2328"
  sketch  "3D эскиз2329"
  sketch  "3D эскиз2330"
  sketch  "3D эскиз2331"
  sketch  "3D эскиз2332"
  sketch  "3D эскиз2333"
  sketch  "3D эскиз2334"
  sketch  "3D эскиз2335"
  sketch  "3D эскиз2336"
  sketch  "3D эскиз2337"
  sketch  "3D эскиз2338"
  sketch  "3D эскиз2339"
  sketch  "3D эскиз2340"
  sketch  "3D эскиз2341"
  sketch  "3D эскиз2342"
  sketch  "3D эскиз2343"
  sketch  "3D эскиз2344"
  sketch  "3D эскиз2345"
  sketch  "3D эскиз2346"
  sketch  "3D эскиз2347"
  sketch  "3D эскиз2348"
  sketch  "3D эскиз2349"
  sketch  "3D эскиз2350"
  sketch  "3D эскиз2351"
  sketch  "3D эскиз2352"
  sketch  "3D эскиз2353"
  sketch  "3D эскиз2354"
  sketch  "3D эскиз2355"
  sketch  "3D эскиз2356"
  sketch  "3D эскиз2357"
  sketch  "3D эскиз2358"
  sketch  "3D эскиз2359"
  sketch  "3D эскиз2360"
  sketch  "3D эскиз2361"
  sketch  "3D эскиз2362"
  sketch  "3D эскиз2363"
  sketch  "3D эскиз2364"
  sketch  "3D эскиз2365"
  sketch  "3D эскиз2366"
  sketch  "3D эскиз2367"
  sketch  "3D эскиз2368"
  sketch  "3D эскиз2369"
  sketch  "3D эскиз2370"
  sketch  "3D эскиз2371"
  sketch  "3D эскиз2372"
  sketch  "3D эскиз2373"
  sketch  "3D эскиз2374"
  sketch  "3D эскиз2375"
  sketch  "3D эскиз2376"
  sketch  "3D эскиз2377"
  sketch  "3D эскиз2378"
  sketch  "3D эскиз2379"
  sketch  "3D эскиз2380"
  sketch  "3D эскиз2381"
  sketch  "3D эскиз2382"
  sketch  "3D эскиз2383"
  sketch  "3D эскиз2384"
  sketch  "3D эскиз2385"
  sketch  "3D эскиз2386"
  sketch  "3D эскиз2387"
  sketch  "3D эскиз2388"
  sketch  "3D эскиз2389"
  sketch  "3D эскиз2390"
  sketch  "3D эскиз2391"
  sketch  "3D эскиз2392"
  sketch  "3D эскиз2393"
  sketch  "3D эскиз2394"
  sketch  "3D эскиз2395"
  sketch  "3D эскиз2396"
  sketch  "3D эскиз2397"
  sketch  "3D эскиз2398"
  sketch  "3D эскиз2399"
  sketch  "3D эскиз2400"
  sketch  "3D эскиз2401"
  sketch  "3D эскиз2402"
  sketch  "3D эскиз2403"
  sketch  "3D эскиз2404"
  sketch  "3D эскиз2405"
  sketch  "3D эскиз2406"
  sketch  "3D эскиз2407"
  sketch  "3D эскиз2408"
  sketch  "3D эскиз2409"
  sketch  "3D эскиз2410"
  sketch  "3D эскиз2411"
  sketch  "3D эскиз2412"
  sketch  "3D эскиз2413"
  sketch  "3D эскиз2414"
  sketch  "3D эскиз2415"
  sketch  "3D эскиз2416"
  sketch  "3D эскиз2417"
  sketch  "3D эскиз2418"
  sketch  "3D эскиз2419"
  sketch  "3D эскиз2420"
  sketch  "3D эскиз2421"
  sketch  "3D эскиз2422"
  sketch  "3D эскиз2423"
  sketch  "3D эскиз2424"
  sketch  "3D эскиз2425"
  sketch  "3D эскиз2426"
  sketch  "3D эскиз2427"
  sketch  "3D эскиз2428"
  sketch  "3D эскиз2429"
  sketch  "3D эскиз2430"
  sketch  "3D эскиз2431"
  sketch  "3D эскиз2432"
  sketch  "3D эскиз2433"
  sketch  "3D эскиз2434"
  sketch  "3D эскиз2435"
  sketch  "3D эскиз2436"
  sketch  "3D эскиз2437"
  sketch  "3D эскиз2438"
  sketch  "3D эскиз2439"
  other  "Твердое тело2"
  other  "Твердое тело3"
  other  "Твердое тело4"
  other  "Твердое тело5"
  other  "Твердое тело6"
  other  "Твердое тело7"
  other  "Твердое тело8"
  other  "Твердое тело9"
  other  "Твердое тело10"
  other  "Твердое тело11"
  other  "Твердое тело12"
  other  "Твердое тело13"
  other  "Твердое тело14"
  other  "Твердое тело15"
  other  "Твердое тело16"
  other  "Твердое тело17"
  other  "Твердое тело18"
  other  "Твердое тело19"
  other  "Твердое тело20"
  other  "Твердое тело21"
  other  "Твердое тело22"
  other  "Твердое тело23"
  other  "Твердое тело24"
  other  "Твердое тело25"
  other  "Твердое тело26"
  other  "Твердое тело27"
  other  "Твердое тело28"
  other  "Твердое тело29"
  other  "Твердое тело30"
  other  "Твердое тело31"
  other  "Твердое тело32"
  other  "Твердое тело33"
  other  "Твердое тело34"
  other  "Твердое тело35"
  other  "Твердое тело36"
  other  "Твердое тело37"
  other  "Твердое тело38"
  other  "Твердое тело39"
  other  "Твердое тело40"
  other  "Твердое тело41"
  other  "Твердое тело42"
  other  "Твердое тело43"
  other  "Твердое тело44"
  other  "Твердое тело45"
  other  "Твердое тело46"
  other  "Твердое тело47"
  other  "Твердое тело48"
  other  "Твердое тело49"
  other  "Твердое тело50"
  other  "Твердое тело51"
  other  "Твердое тело52"
  other  "Твердое тело53"
  other  "Твердое тело54"
  other  "Твердое тело55"
  other  "Твердое тело56"
  other  "Твердое тело57"
  other  "Твердое тело58"
  other  "Твердое тело59"
  other  "Твердое тело60"
  other  "Твердое тело61"
  other  "Твердое тело62"
  other  "Твердое тело63"
  other  "Твердое тело64"
  other  "Твердое тело65"
  other  "Твердое тело66"
  other  "Твердое тело67"
  other  "Твердое тело68"
  other  "Твердое тело69"
  other  "Твердое тело70"
  other  "Твердое тело71"
  other  "Твердое тело72"
  other  "Твердое тело73"
  other  "Твердое тело74"
  other  "Твердое тело75"
  other  "Твердое тело76"
  other  "Твердое тело77"
  other  "Твердое тело78"
  other  "Твердое тело79"
  other  "Твердое тело80"
  other  "Твердое тело81"
  other  "Твердое тело82"
  other  "Твердое тело83"
  other  "Твердое тело84"
  other  "Твердое тело85"
  other  "Твердое тело86"
  other  "Твердое тело87"
  other  "Твердое тело88"
  other  "Твердое тело89"
  other  "Твердое тело90"
  other  "Твердое тело91"
  other  "Твердое тело92"
  other  "Твердое тело93"
  other  "Твердое тело94"
  other  "Твердое тело95"
  other  "Твердое тело96"
  other  "Твердое тело97"
  other  "Твердое тело98"
  other  "Твердое тело99"
  other  "Твердое тело100"
  other  "Твердое тело101"
  other  "Твердое тело102"
  other  "Твердое тело103"
  other  "Твердое тело104"
  other  "Твердое тело105"
  other  "Твердое тело106"
  other  "Твердое тело107"
  other  "Твердое тело108"
  other  "Твердое тело109"
  other  "Твердое тело110"
  other  "Твердое тело111"
  other  "Твердое тело112"
  other  "Твердое тело113"
  other  "Твердое тело114"
  other  "Твердое тело115"
  other  "Твердое тело116"
  other  "Твердое тело117"
  other  "Твердое тело118"
  other  "Твердое тело119"
  other  "Твердое тело120"
  other  "Твердое тело121"
  other  "Твердое тело122"
  other  "Твердое тело123"
  other  "Твердое тело124"
  other  "Твердое тело125"
  other  "Твердое тело126"
  other  "Твердое тело127"
  other  "Твердое тело128"
  other  "Твердое тело129"
  other  "Твердое тело130"
  other  "Твердое тело131"
  other  "Твердое тело132"
  other  "Твердое тело133"
  other  "Твердое тело134"
  other  "Твердое тело135"
  other  "Твердое тело136"
  other  "Твердое тело137"
  other  "Твердое тело138"
  other  "Твердое тело139"
  other  "Твердое тело140"
  other  "Твердое тело141"
  other  "Твердое тело142"
  other  "Твердое тело143"
  other  "Твердое тело144"
  other  "Твердое тело145"
  other  "Твердое тело146"
  other  "Твердое тело147"
  other  "Твердое тело148"
  other  "Твердое тело149"
  other  "Твердое тело150"
  other  "Твердое тело151"
  other  "Твердое тело152"
  other  "Твердое тело153"
  other  "Твердое тело154"
  other  "Твердое тело155"
  other  "Твердое тело156"
  other  "Твердое тело157"
  other  "Твердое тело158"
  other  "Твердое тело159"
  other  "Твердое тело160"
  other  "Твердое тело161"
  other  "Твердое тело162"
  other  "Твердое тело163"
  other  "Твердое тело164"
  other  "Твердое тело165"
  other  "Твердое тело166"
  other  "Твердое тело167"
  other  "Твердое тело168"
  other  "Твердое тело169"
  other  "Твердое тело170"
  other  "Твердое тело171"
  other  "Твердое тело172"
  other  "Твердое тело173"
  other  "Твердое тело174"
  other  "Твердое тело175"
  other  "Твердое тело176"
  other  "Твердое тело177"
  other  "Твердое тело178"
  other  "Твердое тело179"
  other  "Твердое тело180"
  other  "Твердое тело181"
  other  "Твердое тело182"
  other  "Твердое тело183"
  other  "Твердое тело184"
  other  "Твердое тело185"
  other  "Твердое тело186"
  other  "Твердое тело187"
  other  "Твердое тело188"
  other  "Твердое тело189"
  other  "Твердое тело190"
  other  "Твердое тело191"
  other  "Твердое тело192"
  other  "Твердое тело193"
  other  "Твердое тело194"
  other  "Твердое тело195"
  other  "Твердое тело196"
  other  "Твердое тело197"
  other  "Твердое тело198"
  other  "Твердое тело199"
  other  "Твердое тело200"
  other  "Твердое тело201"
  other  "Твердое тело202"
  other  "Твердое тело203"
  other  "Твердое тело204"
  other  "Твердое тело205"
  other  "Твердое тело206"
  other  "Твердое тело207"
  other  "Твердое тело208"
  other  "Твердое тело209"
  other  "Твердое тело210"
  other  "Твердое тело211"
  other  "Твердое тело212"
  other  "Твердое тело213"
  other  "Твердое тело214"
  other  "Твердое тело215"
  other  "Твердое тело216"
  other  "Твердое тело217"
  other  "Твердое тело218"
  other  "Твердое тело219"
  other  "Твердое тело220"
  other  "Твердое тело221"
  other  "Твердое тело222"
  other  "Твердое тело223"
  other  "Твердое тело224"
  other  "Твердое тело225"
  other  "Твердое тело226"
  other  "Твердое тело227"
  other  "Твердое тело228"
  other  "Твердое тело229"
  other  "Твердое тело230"
  other  "Твердое тело231"
  other  "Твердое тело232"
  other  "Твердое тело233"
  other  "Твердое тело234"
  other  "Твердое тело235"
  other  "Твердое тело236"
  other  "Твердое тело237"
  other  "Твердое тело238"
  other  "Твердое тело239"
  other  "Твердое тело240"
  other  "Твердое тело241"
  other  "Твердое тело242"
  other  "Твердое тело243"
  other  "Твердое тело244"
  other  "Твердое тело245"
  other  "Твердое тело246"
  other  "Твердое тело247"
  other  "Твердое тело248"
  other  "Твердое тело249"
  other  "Твердое тело250"
  other  "Твердое тело251"
  other  "Твердое тело252"
  other  "Твердое тело253"
  other  "Твердое тело254"
  other  "Твердое тело255"
  other  "Твердое тело256"
  other  "Твердое тело257"
  other  "Твердое тело258"
  other  "Твердое тело259"
  other  "Твердое тело260"
  other  "Твердое тело261"
  other  "Твердое тело262"
  other  "Твердое тело263"
  other  "Твердое тело264"
  other  "Твердое тело265"
  other  "Твердое тело266"
  other  "Твердое тело267"
  other  "Твердое тело268"
  other  "Твердое тело269"
  other  "Твердое тело270"
  other  "Твердое тело271"
  other  "Твердое тело272"
  other  "Твердое тело273"
  other  "Твердое тело274"
  other  "Твердое тело275"
  other  "Твердое тело276"
  other  "Твердое тело277"
  other  "Твердое тело278"
  other  "Твердое тело279"
  other  "Твердое тело280"
  other  "Твердое тело281"
  other  "Твердое тело282"
  other  "Твердое тело283"
  other  "Твердое тело284"
  other  "Твердое тело285"
  other  "Твердое тело286"
  other  "Твердое тело287"
  other  "Твердое тело288"
  other  "Твердое тело289"
  other  "Твердое тело290"
  other  "Твердое тело291"
  other  "Твердое тело292"
  other  "Твердое тело293"
  other  "Твердое тело294"
  other  "Твердое тело295"
  other  "Твердое тело296"
  other  "Твердое тело297"
  other  "Твердое тело298"
  other  "Твердое тело299"
  other  "Твердое тело300"
  other  "Твердое тело301"
  other  "Твердое тело302"
  other  "Твердое тело303"
  other  "Твердое тело304"
  other  "Твердое тело305"
  other  "Твердое тело306"
  other  "Твердое тело307"
  other  "Твердое тело308"
  other  "Твердое тело309"
  other  "Твердое тело310"
  other  "Твердое тело311"
  other  "Твердое тело312"
  other  "Твердое тело313"
  other  "Твердое тело314"
  other  "Твердое тело315"
  other  "Твердое тело316"
  other  "Твердое тело317"
  other  "Твердое тело318"
  other  "Твердое тело319"
  other  "Твердое тело320"
  other  "Твердое тело321"
  other  "Твердое тело322"
  other  "Твердое тело323"
  other  "Твердое тело324"
  other  "Твердое тело325"
  other  "Твердое тело326"
  other  "Твердое тело327"
  other  "Твердое тело328"
  other  "Твердое тело329"
  other  "Твердое тело330"
  other  "Твердое тело331"
  other  "Твердое тело332"
  other  "Твердое тело333"
  other  "Твердое тело334"
  other  "Твердое тело335"
  other  "Твердое тело336"
  other  "Твердое тело337"
  other  "Твердое тело338"
  other  "Твердое тело339"
  other  "Твердое тело340"
  other  "Твердое тело341"
  other  "Твердое тело342"
  other  "Твердое тело343"
  other  "Твердое тело344"
  other  "Твердое тело345"
  other  "Твердое тело346"
  other  "Твердое тело347"
  other  "Твердое тело348"
  other  "Твердое тело349"
  other  "Твердое тело350"
  other  "Твердое тело351"
  other  "Твердое тело352"
  other  "Твердое тело353"
  other  "Твердое тело354"
  other  "Твердое тело355"
  other  "Твердое тело356"
  other  "Твердое тело357"
  other  "Твердое тело358"
  other  "Твердое тело359"
  other  "Твердое тело360"
  other  "Твердое тело361"
  other  "Твердое тело362"
  other  "Твердое тело363"
  other  "Твердое тело364"
  other  "Твердое тело365"
  other  "Твердое тело366"
  other  "Твердое тело367"
  other  "Твердое тело368"
  other  "Твердое тело369"
  other  "Твердое тело370"
  other  "Твердое тело371"
  other  "Твердое тело372"
  other  "Твердое тело373"
  other  "Твердое тело374"
  other  "Твердое тело375"
  other  "Твердое тело376"
  other  "Твердое тело377"
  other  "Твердое тело378"
  other  "Твердое тело379"
  other  "Твердое тело380"
  other  "Твердое тело381"
  other  "Твердое тело382"
  other  "Твердое тело383"
  other  "Твердое тело384"
  other  "Твердое тело385"
  other  "Твердое тело386"
  other  "Твердое тело387"
  other  "Твердое тело388"
  other  "Твердое тело389"
  other  "Твердое тело390"
  other  "Твердое тело391"
  other  "Твердое тело392"
  other  "Твердое тело393"
  other  "Твердое тело394"
  other  "Твердое тело395"
  other  "Твердое тело396"
  other  "Твердое тело397"
  other  "Твердое тело398"
  other  "Твердое тело399"
  other  "Твердое тело400"
  other  "Твердое тело401"
  other  "Твердое тело402"
  other  "Твердое тело403"
  other  "Твердое тело404"
  other  "Твердое тело405"
  other  "Твердое тело406"
  other  "Твердое тело407"
  other  "Твердое тело408"
  other  "Твердое тело409"
  other  "Твердое тело410"
  other  "Твердое тело411"
  other  "Твердое тело412"
  other  "Твердое тело413"
  other  "Твердое тело414"
  other  "Твердое тело415"
  other  "Твердое тело416"
  other  "Твердое тело417"
  other  "Твердое тело418"
  other  "Твердое тело419"
  other  "Твердое тело420"
  other  "Твердое тело421"
  other  "Твердое тело422"
  other  "Твердое тело423"
  other  "Твердое тело424"
  other  "Твердое тело425"
  other  "Твердое тело426"
  other  "Твердое тело427"
  other  "Твердое тело428"
  other  "Твердое тело429"
  other  "Твердое тело430"
  other  "Твердое тело431"
  other  "Твердое тело432"
  other  "Твердое тело433"
  other  "Твердое тело434"
  other  "Твердое тело435"
  other  "Твердое тело436"
  other  "Твердое тело437"
  other  "Твердое тело438"
  other  "Твердое тело439"
  other  "Твердое тело440"
  other  "Твердое тело441"
  other  "Твердое тело442"
  other  "Твердое тело443"
  other  "Твердое тело444"
  other  "Твердое тело445"
  other  "Твердое тело446"
  other  "Твердое тело447"
  other  "Твердое тело448"
  other  "Твердое тело449"
  other  "Твердое тело450"
  other  "Твердое тело451"
  other  "Твердое тело452"
  other  "Твердое тело453"
  other  "Твердое тело454"
  other  "Твердое тело455"
  other  "Твердое тело456"
  other  "Твердое тело457"
  other  "Твердое тело458"
  other  "Твердое тело459"
  other  "Твердое тело460"
  other  "Твердое тело461"
  other  "Твердое тело462"
  other  "Твердое тело463"
  other  "Твердое тело464"
  other  "Твердое тело465"
  other  "Твердое тело466"
  other  "Твердое тело467"
  other  "Твердое тело468"
  other  "Твердое тело469"
  other  "Твердое тело470"
  other  "Твердое тело471"
  other  "Твердое тело472"
  other  "Твердое тело473"
  other  "Твердое тело474"
  other  "Твердое тело475"
  other  "Твердое тело476"
  other  "Твердое тело477"
  other  "Твердое тело478"
  other  "Твердое тело479"
  other  "Твердое тело480"
  other  "Твердое тело481"
  other  "Твердое тело482"
  other  "Твердое тело483"
  other  "Твердое тело484"
  other  "Твердое тело485"
  other  "Твердое тело486"
  other  "Твердое тело487"
  other  "Твердое тело488"
  other  "Твердое тело489"
  other  "Твердое тело490"
  other  "Твердое тело491"
  other  "Твердое тело492"
  other  "Твердое тело493"
  other  "Твердое тело494"
  other  "Твердое тело495"
  other  "Твердое тело496"
  other  "Твердое тело497"
  other  "Твердое тело498"
  other  "Твердое тело499"
  other  "Твердое тело500"
  other  "Твердое тело501"
  other  "Твердое тело502"
  other  "Твердое тело503"
  other  "Твердое тело504"
  other  "Твердое тело505"
  other  "Твердое тело506"
  other  "Твердое тело507"
  other  "Твердое тело508"
  other  "Твердое тело509"
  other  "Твердое тело510"
  other  "Твердое тело511"
  other  "Твердое тело512"
  other  "Твердое тело513"
  other  "Твердое тело514"
  other  "Твердое тело515"
  other  "Твердое тело516"
  other  "Твердое тело517"
  other  "Твердое тело518"
  other  "Твердое тело519"
  other  "Твердое тело520"
  other  "Твердое тело521"
  other  "Твердое тело522"
  other  "Твердое тело523"
  other  "Твердое тело524"
  other  "Твердое тело525"
  other  "Твердое тело526"
  other  "Твердое тело527"
  other  "Твердое тело528"
  other  "Твердое тело529"
  other  "Твердое тело530"
  other  "Твердое тело531"
  other  "Твердое тело532"
  other  "Твердое тело533"
  other  "Твердое тело534"
  other  "Твердое тело535"
  other  "Твердое тело536"
  other  "Твердое тело537"
  other  "Твердое тело538"
  other  "Твердое тело539"
  other  "Твердое тело540"
  other  "Твердое тело541"
  other  "Твердое тело542"
  other  "Твердое тело543"
  other  "Твердое тело544"
  other  "Твердое тело545"
  other  "Твердое тело546"
  other  "Твердое тело547"
  other  "Твердое тело548"
  other  "Твердое тело549"
  other  "Твердое тело550"
  other  "Твердое тело551"
  other  "Твердое тело552"
  other  "Твердое тело553"
  other  "Твердое тело554"
  other  "Твердое тело555"
  other  "Твердое тело556"
  other  "Твердое тело557"
  other  "Твердое тело558"
  other  "Твердое тело559"
  other  "Твердое тело560"
  other  "Твердое тело561"
  other  "Твердое тело562"
  other  "Твердое тело563"
  other  "Твердое тело564"
  other  "Твердое тело565"
  other  "Твердое тело566"
  other  "Твердое тело567"
  other  "Твердое тело568"
  other  "Твердое тело569"
  other  "Твердое тело570"
  other  "Твердое тело571"
  other  "Твердое тело572"
  other  "Твердое тело573"
  other  "Твердое тело574"
  other  "Твердое тело575"
  other  "Твердое тело576"
  other  "Твердое тело577"
  other  "Твердое тело578"
  other  "Твердое тело579"
  other  "Твердое тело580"
  other  "Твердое тело581"
  other  "Твердое тело582"
  other  "Твердое тело583"
  other  "Твердое тело584"
  other  "Твердое тело585"
  other  "Твердое тело586"
  other  "Твердое тело587"
  other  "Твердое тело588"
  other  "Твердое тело589"
  other  "Твердое тело590"
  other  "Твердое тело591"
  other  "Твердое тело592"
  other  "Твердое тело593"
  other  "Твердое тело594"
  other  "Твердое тело595"
  other  "Твердое тело596"
  other  "Твердое тело597"
  other  "Твердое тело598"
  other  "Твердое тело599"
  other  "Твердое тело600"
  other  "Твердое тело601"
  other  "Твердое тело602"
  other  "Твердое тело603"
  other  "Твердое тело604"
  other  "Твердое тело605"
  other  "Твердое тело606"
  other  "Твердое тело607"
  other  "Твердое тело608"
  other  "Твердое тело609"
  other  "Твердое тело610"
  other  "Твердое тело611"
  other  "Твердое тело612"
  other  "Твердое тело613"
  other  "Твердое тело614"
  other  "Твердое тело615"
  other  "Твердое тело616"
  other  "Твердое тело617"
  other  "Твердое тело618"
  other  "Твердое тело619"
  other  "Твердое тело620"
  other  "Твердое тело621"
  other  "Твердое тело622"
  other  "Твердое тело623"
  other  "Твердое тело624"
  other  "Твердое тело625"
  other  "Твердое тело626"
  other  "Твердое тело627"
  other  "Твердое тело628"
  other  "Твердое тело629"
  other  "Твердое тело630"
  other  "Твердое тело631"
  other  "Твердое тело632"
  other  "Твердое тело633"
  other  "Твердое тело634"
  other  "Твердое тело635"
  other  "Твердое тело636"
  other  "Твердое тело637"
  other  "Твердое тело638"
  other  "Твердое тело639"
  other  "Твердое тело640"
  other  "Твердое тело641"
  other  "Твердое тело642"
  other  "Твердое тело643"
  other  "Твердое тело644"
  other  "Твердое тело645"
  other  "Твердое тело646"
  other  "Твердое тело647"
  other  "Твердое тело648"
  other  "Твердое тело649"
  other  "Твердое тело650"
  other  "Твердое тело651"
  other  "Твердое тело652"
  other  "Твердое тело653"
  other  "Твердое тело654"
  other  "Твердое тело655"
  other  "Твердое тело656"
  other  "Твердое тело657"
  other  "Твердое тело658"
  other  "Твердое тело659"
  other  "Твердое тело660"
  other  "Твердое тело661"
  other  "Твердое тело662"
  other  "Твердое тело663"
  other  "Твердое тело664"
  other  "Твердое тело665"
  other  "Твердое тело666"
  other  "Твердое тело667"
  other  "Твердое тело668"
  other  "Твердое тело669"
  other  "Твердое тело670"
  other  "Твердое тело671"
  other  "Твердое тело672"
  other  "Твердое тело673"
  other  "Твердое тело674"
  other  "Твердое тело675"
  other  "Твердое тело676"
  other  "Твердое тело677"
  other  "Твердое тело678"
  other  "Твердое тело679"
  other  "Твердое тело680"
  other  "Твердое тело681"
  other  "Твердое тело682"
  other  "Твердое тело683"
  other  "Твердое тело684"
  other  "Твердое тело685"
  other  "Твердое тело686"
  other  "Твердое тело687"
  other  "Твердое тело688"
  other  "Твердое тело689"
  other  "Твердое тело690"
  other  "Твердое тело691"
  other  "Твердое тело692"
  other  "Твердое тело693"
  other  "Твердое тело694"
  other  "Твердое тело695"
  other  "Твердое тело696"
  other  "Твердое тело697"
  other  "Твердое тело698"
  other  "Твердое тело699"
  other  "Твердое тело700"
  other  "Твердое тело701"
  other  "Твердое тело702"
  other  "Твердое тело703"
  other  "Твердое тело704"
  other  "Твердое тело705"
  other  "Твердое тело706"
  other  "Твердое тело707"
  other  "Твердое тело708"
  other  "Твердое тело709"
  other  "Твердое тело710"
  other  "Твердое тело711"
  other  "Твердое тело712"
  other  "Твердое тело713"
  other  "Твердое тело714"
  other  "Твердое тело715"
  other  "Твердое тело716"
  other  "Твердое тело717"
  other  "Твердое тело718"
  other  "Твердое тело719"
  other  "Твердое тело720"
  other  "Твердое тело721"
  other  "Твердое тело722"
  other  "Твердое тело723"
  other  "Твердое тело724"
  other  "Твердое тело725"
  other  "Твердое тело726"
  other  "Твердое тело727"
  other  "Твердое тело728"
  other  "Твердое тело729"
  other  "Твердое тело730"
  other  "Твердое тело731"
  other  "Твердое тело732"
  other  "Твердое тело733"
  other  "Твердое тело734"
  other  "Твердое тело735"
  other  "Твердое тело736"
  other  "Твердое тело737"
  other  "Твердое тело738"
  other  "Твердое тело739"
  other  "Твердое тело740"
  other  "Твердое тело741"
  other  "Твердое тело742"
  other  "Твердое тело743"
  other  "Твердое тело744"
  other  "Твердое тело745"
  other  "Твердое тело746"
  other  "Твердое тело747"
  other  "Твердое тело748"
  other  "Твердое тело749"
  other  "Твердое тело750"
  other  "Твердое тело751"
  other  "Твердое тело752"
  other  "Твердое тело753"
  other  "Твердое тело754"
  other  "Твердое тело755"
  other  "Твердое тело756"
  other  "Твердое тело757"
  other  "Твердое тело758"
  other  "Твердое тело759"
  other  "Твердое тело760"
  other  "Твердое тело761"
  other  "Твердое тело762"
  other  "Твердое тело763"
  other  "Твердое тело764"
  other  "Твердое тело765"
  other  "Твердое тело766"
  other  "Твердое тело767"
  other  "Твердое тело768"
  other  "Твердое тело769"
  other  "Твердое тело770"
  other  "Твердое тело771"
  other  "Твердое тело772"
  other  "Твердое тело773"
  other  "Твердое тело774"
  other  "Твердое тело775"
  other  "Твердое тело776"
  other  "Твердое тело777"
  other  "Твердое тело778"
  other  "Твердое тело779"
  other  "Твердое тело780"
  other  "Твердое тело781"
  other  "Твердое тело782"
  other  "Твердое тело783"
  other  "Твердое тело784"
  other  "Твердое тело785"
  other  "Твердое тело786"
  other  "Твердое тело787"
  other  "Твердое тело788"
  other  "Твердое тело789"
  other  "Твердое тело790"
  other  "Твердое тело791"
  other  "Твердое тело792"
  other  "Твердое тело793"
  other  "Твердое тело794"
  other  "Твердое тело795"
  other  "Твердое тело796"
  other  "Твердое тело797"
  other  "Твердое тело798"
  other  "Твердое тело799"
  other  "Твердое тело800"
  other  "Твердое тело801"
  other  "Твердое тело802"
  other  "Твердое тело803"
  other  "Твердое тело804"
  other  "Твердое тело805"
  other  "Твердое тело806"
  other  "Твердое тело807"
  other  "Твердое тело808"
  other  "Твердое тело809"
  other  "Твердое тело810"
  other  "Твердое тело811"
  other  "Твердое тело812"
  other  "Твердое тело813"
  other  "Твердое тело814"
  other  "Твердое тело815"
  other  "Твердое тело816"
  other  "Твердое тело817"
  other  "Твердое тело818"
  other  "Твердое тело819"
  other  "Твердое тело820"
  other  "Твердое тело821"
  other  "Твердое тело822"
  other  "Твердое тело823"
  other  "Твердое тело824"
  other  "Твердое тело825"
  other  "Твердое тело826"
  other  "Твердое тело827"
  other  "Твердое тело828"
  other  "Твердое тело829"
  other  "Твердое тело830"
  other  "Твердое тело831"
  other  "Твердое тело832"
  other  "Твердое тело833"
  other  "Твердое тело834"
  other  "Твердое тело835"
  other  "Твердое тело836"
  other  "Твердое тело837"
  other  "Твердое тело838"
  other  "Твердое тело839"
  other  "Твердое тело840"
  other  "Твердое тело841"
  other  "Твердое тело842"
  other  "Твердое тело843"
  other  "Твердое тело844"
  other  "Твердое тело845"
  other  "Твердое тело846"
  other  "Твердое тело847"
  other  "Твердое тело848"
  other  "Твердое тело849"
  other  "Твердое тело850"
  other  "Твердое тело851"
  other  "Твердое тело852"
  other  "Твердое тело853"
  other  "Твердое тело854"
  other  "Твердое тело855"
  other  "Твердое тело856"
  other  "Твердое тело857"
  other  "Твердое тело858"
  other  "Твердое тело859"
  other  "Твердое тело860"
  other  "Твердое тело861"
  other  "Твердое тело862"
  other  "Твердое тело863"
  other  "Твердое тело864"
  other  "Твердое тело865"
  other  "Твердое тело866"
  other  "Твердое тело867"
  other  "Твердое тело868"
  other  "Твердое тело869"
  other  "Твердое тело870"
  other  "Твердое тело871"
  other  "Твердое тело872"
  other  "Твердое тело873"
  other  "Твердое тело874"
  other  "Твердое тело875"
  other  "Твердое тело876"
  other  "Твердое тело877"
  other  "Твердое тело878"
  other  "Твердое тело879"
  other  "Твердое тело880"
  other  "Твердое тело881"
  other  "Твердое тело882"
  other  "Твердое тело883"
  other  "Твердое тело884"
  other  "Твердое тело885"
  other  "Твердое тело886"
  other  "Твердое тело887"
  other  "Твердое тело888"
  other  "Твердое тело889"
  other  "Твердое тело890"
  other  "Твердое тело891"
  other  "Твердое тело892"
  other  "Твердое тело893"
  other  "Твердое тело894"
  other  "Твердое тело895"
  other  "Твердое тело896"
  other  "Твердое тело897"
  other  "Твердое тело898"
  other  "Твердое тело899"
  other  "Твердое тело900"
  other  "Твердое тело901"
  other  "Твердое тело902"
  other  "Твердое тело903"
  other  "Твердое тело904"
  other  "Твердое тело905"
  other  "Твердое тело906"
  other  "Твердое тело907"
  other  "Твердое тело908"
  other  "Твердое тело909"
  other  "Твердое тело910"
  other  "Твердое тело911"
  other  "Твердое тело912"
  other  "Твердое тело913"
  other  "Твердое тело914"
  other  "Твердое тело915"
  other  "Твердое тело916"
  other  "Твердое тело917"
  other  "Твердое тело918"
  other  "Твердое тело919"
  other  "Твердое тело920"
  other  "Твердое тело921"
  other  "Твердое тело922"
  other  "Твердое тело923"
  other  "Твердое тело924"
  other  "Твердое тело925"
  other  "Твердое тело926"
  other  "Твердое тело927"
  other  "Твердое тело928"
  other  "Твердое тело929"
  other  "Твердое тело930"
  other  "Твердое тело931"
  other  "Твердое тело932"
  other  "Твердое тело933"
  other  "Твердое тело934"
  other  "Твердое тело935"
  other  "Твердое тело936"
  other  "Твердое тело937"
  other  "Твердое тело938"
  other  "Твердое тело939"
  other  "Твердое тело940"
  other  "Твердое тело941"
  other  "Твердое тело942"
  other  "Твердое тело943"
  other  "Твердое тело944"
  other  "Твердое тело945"
  other  "Твердое тело946"
  other  "Твердое тело947"
  other  "Твердое тело948"
  other  "Твердое тело949"
  other  "Твердое тело950"
  other  "Твердое тело951"
  other  "Твердое тело952"
  other  "Твердое тело953"
  other  "Твердое тело954"
  other  "Твердое тело955"
  other  "Твердое тело956"
  other  "Твердое тело957"
  other  "Твердое тело958"
  other  "Твердое тело959"
  other  "Твердое тело960"
  other  "Твердое тело961"
  other  "Твердое тело962"
  other  "Твердое тело963"
  other  "Твердое тело964"
  other  "Твердое тело965"
  other  "Твердое тело966"
  other  "Твердое тело967"
  other  "Твердое тело968"
  other  "Твердое тело969"
  other  "Твердое тело970"
  other  "Твердое тело971"
  other  "Твердое тело972"
  other  "Твердое тело973"
  other  "Твердое тело974"
  other  "Твердое тело975"
  other  "Твердое тело976"
  other  "Твердое тело977"
  other  "Твердое тело978"
  other  "Твердое тело979"
  other  "Твердое тело980"
  other  "Твердое тело981"
  other  "Твердое тело982"
  other  "Твердое тело983"
  other  "Твердое тело984"
  other  "Твердое тело985"
  other  "Твердое тело986"
  other  "Твердое тело987"
  other  "Твердое тело988"
  other  "Твердое тело989"
  other  "Твердое тело990"
  other  "Твердое тело991"
  other  "Твердое тело992"
  other  "Твердое тело993"
  other  "Твердое тело994"
  other  "Твердое тело995"
  other  "Твердое тело996"
  other  "Твердое тело997"
  other  "Твердое тело998"
  other  "Твердое тело999"
  other  "Твердое тело1000"
  other  "Твердое тело1001"
  other  "Твердое тело1002"
  other  "Твердое тело1003"
  other  "Твердое тело1004"
  other  "Твердое тело1005"
  other  "Твердое тело1006"
  other  "Твердое тело1007"
  other  "Твердое тело1008"
  other  "Твердое тело1009"
  other  "Твердое тело1010"
  other  "Твердое тело1011"
  other  "Твердое тело1012"
  other  "Твердое тело1013"
  other  "Твердое тело1014"
  other  "Твердое тело1015"
  other  "Твердое тело1016"
  other  "Твердое тело1017"
  other  "Твердое тело1018"
  other  "Твердое тело1019"
  other  "Твердое тело1020"
  other  "Твердое тело1021"
  other  "Твердое тело1022"
  other  "Твердое тело1023"
  other  "Твердое тело1024"
  other  "Твердое тело1025"
  other  "Твердое тело1026"
  other  "Твердое тело1027"
  other  "Твердое тело1028"
  other  "Твердое тело1029"
  other  "Твердое тело1030"
  other  "Твердое тело1031"
  other  "Твердое тело1032"
  other  "Твердое тело1033"
  other  "Твердое тело1034"
  other  "Твердое тело1035"
  other  "Твердое тело1036"
  other  "Твердое тело1037"
  other  "Твердое тело1038"
  other  "Твердое тело1039"
  other  "Твердое тело1040"
  other  "Твердое тело1041"
  other  "Твердое тело1042"
  other  "Твердое тело1043"
  other  "Твердое тело1044"
  other  "Твердое тело1045"
  other  "Твердое тело1046"
  other  "Твердое тело1047"
  other  "Твердое тело1048"
  other  "Твердое тело1049"
  other  "Твердое тело1050"
  other  "Твердое тело1051"
  other  "Твердое тело1052"
  other  "Твердое тело1053"
  other  "Твердое тело1054"
  other  "Твердое тело1055"
  other  "Твердое тело1056"
  other  "Твердое тело1057"
  other  "Твердое тело1058"
  other  "Твердое тело1059"
  other  "Твердое тело1060"
  other  "Твердое тело1061"
  other  "Твердое тело1062"
  other  "Твердое тело1063"
  other  "Твердое тело1064"
  other  "Твердое тело1065"
  other  "Твердое тело1066"
  other  "Твердое тело1067"
  other  "Твердое тело1068"
  other  "Твердое тело1069"
  other  "Твердое тело1070"
  other  "Твердое тело1071"
  other  "Твердое тело1072"
  other  "Твердое тело1073"
  other  "Твердое тело1074"
  other  "Твердое тело1075"
  other  "Твердое тело1076"
  other  "Твердое тело1077"
  other  "Твердое тело1078"
  other  "Твердое тело1079"
  other  "Твердое тело1080"
  other  "Твердое тело1081"
  other  "Твердое тело1082"
  other  "Твердое тело1083"
  other  "Твердое тело1084"
  other  "Твердое тело1085"
  other  "Твердое тело1086"
  other  "Твердое тело1087"
  other  "Твердое тело1088"
  other  "Твердое тело1089"
  other  "Твердое тело1090"
  other  "Твердое тело1091"
  other  "Твердое тело1092"
  other  "Твердое тело1093"
  other  "Твердое тело1094"
  other  "Твердое тело1095"
  other  "Твердое тело1096"
  other  "Твердое тело1097"
  other  "Твердое тело1098"
  other  "Твердое тело1099"
  other  "Твердое тело1100"
  other  "Твердое тело1101"
  other  "Твердое тело1102"
  other  "Твердое тело1103"
  other  "Твердое тело1104"
  other  "Твердое тело1105"
  other  "Твердое тело1106"
  other  "Твердое тело1107"
  other  "Твердое тело1108"
  other  "Твердое тело1109"
  other  "Твердое тело1110"
  other  "Твердое тело1111"
  other  "Твердое тело1112"
  other  "Твердое тело1113"
  other  "Твердое тело1114"
  other  "Твердое тело1115"
  other  "Твердое тело1116"
  other  "Твердое тело1117"
  other  "Твердое тело1118"
  other  "Твердое тело1119"
  other  "Твердое тело1120"
  other  "Твердое тело1121"
  other  "Твердое тело1122"
  other  "Твердое тело1123"
  other  "Твердое тело1124"
  other  "Твердое тело1125"
  other  "Твердое тело1126"
  other  "Твердое тело1127"
  other  "Твердое тело1128"
  other  "Твердое тело1129"
  other  "Твердое тело1130"
  other  "Твердое тело1131"
  other  "Твердое тело1132"
  other  "Твердое тело1133"
  other  "Твердое тело1134"
  other  "Твердое тело1135"
  other  "Твердое тело1136"
  other  "Твердое тело1137"
  other  "Твердое тело1138"
  other  "Твердое тело1139"
  other  "Твердое тело1140"
  other  "Твердое тело1141"
  other  "Твердое тело1142"
  other  "Твердое тело1143"
  other  "Твердое тело1144"
  other  "Твердое тело1145"
  other  "Твердое тело1146"
  other  "Твердое тело1147"
  other  "Твердое тело1148"
  other  "Твердое тело1149"
  other  "Твердое тело1150"
  other  "Твердое тело1151"
  other  "Твердое тело1152"
  other  "Твердое тело1153"
  other  "Твердое тело1154"
  other  "Твердое тело1155"
  other  "Твердое тело1156"
  other  "Твердое тело1157"
  other  "Твердое тело1158"
  other  "Твердое тело1159"
  other  "Твердое тело1160"
  other  "Твердое тело1161"
  other  "Твердое тело1162"
  other  "Твердое тело1163"
  other  "Твердое тело1164"
  other  "Твердое тело1165"
  other  "Твердое тело1166"
  other  "Твердое тело1167"
  other  "Твердое тело1168"
  other  "Твердое тело1169"
  other  "Твердое тело1170"
  other  "Твердое тело1171"
  other  "Твердое тело1172"
  other  "Твердое тело1173"
  other  "Твердое тело1174"
  other  "Твердое тело1175"
  other  "Твердое тело1176"
  other  "Твердое тело1177"
  other  "Твердое тело1178"
  other  "Твердое тело1179"
  other  "Твердое тело1180"
  other  "Твердое тело1181"
  other  "Твердое тело1182"
  other  "Твердое тело1183"
  other  "Твердое тело1184"
  other  "Твердое тело1185"
  other  "Твердое тело1186"
  other  "Твердое тело1187"
  other  "Твердое тело1188"
  other  "Твердое тело1189"
  other  "Твердое тело1190"
  other  "Твердое тело1191"
  other  "Твердое тело1192"
  other  "Твердое тело1193"
  other  "Твердое тело1194"
  other  "Твердое тело1195"
  other  "Твердое тело1196"
  other  "Твердое тело1197"
  other  "Твердое тело1198"
  other  "Твердое тело1199"
  other  "Твердое тело1200"
  other  "Твердое тело1201"
  other  "Твердое тело1202"
  other  "Твердое тело1203"
  other  "Твердое тело1204"
  other  "Твердое тело1205"
  other  "Твердое тело1206"
  other  "Твердое тело1207"
  other  "Твердое тело1208"
  other  "Твердое тело1209"
  other  "Твердое тело1210"
  other  "Твердое тело1211"
  other  "Твердое тело1212"
  other  "Твердое тело1213"
  other  "Твердое тело1214"
  other  "Твердое тело1215"
  other  "Твердое тело1216"
  other  "Твердое тело1217"
  other  "Твердое тело1218"
  other  "Твердое тело1219"
  other  "Твердое тело1220"
  other  "Твердое тело1221"
  other  "Твердое тело1222"
  other  "Твердое тело1223"
  other  "Твердое тело1224"
  other  "Твердое тело1225"
  other  "Твердое тело1226"
  other  "Твердое тело1227"
  other  "Твердое тело1228"
  other  "Твердое тело1229"
  other  "Твердое тело1230"
  other  "Твердое тело1231"
  other  "Твердое тело1232"
  other  "Твердое тело1233"
  other  "Твердое тело1234"
  other  "Твердое тело1235"
  other  "Твердое тело1236"
  other  "Твердое тело1237"
  other  "Твердое тело1238"
  other  "Твердое тело1239"
  other  "Твердое тело1240"
  other  "Твердое тело1241"
  other  "Твердое тело1242"
  other  "Твердое тело1243"
  other  "Твердое тело1244"
  other  "Твердое тело1245"
  other  "Твердое тело1246"
  other  "Твердое тело1247"
  other  "Твердое тело1248"
  other  "Твердое тело1249"
  other  "Твердое тело1250"
  other  "Твердое тело1251"
  other  "Твердое тело1252"
  other  "Твердое тело1253"
  other  "Твердое тело1254"
  other  "Твердое тело1255"
  other  "Твердое тело1256"
  other  "Твердое тело1257"
  other  "Твердое тело1258"
  other  "Твердое тело1259"
  other  "Твердое тело1260"
  other  "Твердое тело1261"
  other  "Твердое тело1262"
  other  "Твердое тело1263"
  other  "Твердое тело1264"
  other  "Твердое тело1265"
  other  "Твердое тело1266"
  other  "Твердое тело1267"
  other  "Твердое тело1268"
  other  "Твердое тело1269"
  other  "Твердое тело1270"
  other  "Твердое тело1271"
  other  "Твердое тело1272"
  other  "Твердое тело1273"
  other  "Твердое тело1274"
  other  "Твердое тело1275"
  other  "Твердое тело1276"
  other  "Твердое тело1277"
  other  "Твердое тело1278"
  other  "Твердое тело1279"
  other  "Твердое тело1280"
  other  "Твердое тело1281"
  other  "Твердое тело1282"
  other  "Твердое тело1283"
  other  "Твердое тело1284"
  other  "Твердое тело1285"
  other  "Твердое тело1286"
  other  "Твердое тело1287"
  other  "Твердое тело1288"
  other  "Твердое тело1289"
  other  "Твердое тело1290"
  other  "Твердое тело1291"
  other  "Твердое тело1292"
  other  "Твердое тело1293"
  other  "Твердое тело1294"
  other  "Твердое тело1295"
  other  "Твердое тело1296"
  other  "Твердое тело1297"
  other  "Твердое тело1298"
  other  "Твердое тело1299"
  other  "Твердое тело1300"
  other  "Твердое тело1301"
  other  "Твердое тело1302"
  other  "Твердое тело1303"
  other  "Твердое тело1304"
  other  "Твердое тело1305"
  other  "Твердое тело1306"
  other  "Твердое тело1307"
  other  "Твердое тело1308"
  other  "Твердое тело1309"
  other  "Твердое тело1310"
  other  "Твердое тело1311"
  other  "Твердое тело1312"
  other  "Твердое тело1313"
  other  "Твердое тело1314"
  other  "Твердое тело1315"
  other  "Твердое тело1316"
  other  "Твердое тело1317"
  other  "Твердое тело1318"
  other  "Твердое тело1319"
  other  "Твердое тело1320"
  other  "Твердое тело1321"
  other  "Твердое тело1322"
  other  "Твердое тело1323"
  other  "Твердое тело1324"
  other  "Твердое тело1325"
  other  "Твердое тело1326"
  other  "Твердое тело1327"
  other  "Твердое тело1328"
  other  "Твердое тело1329"
  other  "Твердое тело1330"
  other  "Твердое тело1331"
  other  "Твердое тело1332"
  other  "Твердое тело1333"
  other  "Твердое тело1334"
  other  "Твердое тело1335"
  other  "Твердое тело1336"
  other  "Твердое тело1337"
  other  "Твердое тело1338"
  other  "Твердое тело1339"
  other  "Твердое тело1340"
  other  "Твердое тело1341"
  other  "Твердое тело1342"
  other  "Твердое тело1343"
  other  "Твердое тело1344"
  other  "Твердое тело1345"
  other  "Твердое тело1346"
  other  "Твердое тело1347"
  other  "Твердое тело1348"
  other  "Твердое тело1349"
  other  "Твердое тело1350"
  other  "Твердое тело1351"
  other  "Твердое тело1352"
  other  "Твердое тело1353"
  other  "Твердое тело1354"
  other  "Твердое тело1355"
  other  "Твердое тело1356"
  other  "Твердое тело1357"
  other  "Твердое тело1358"
  other  "Твердое тело1359"
  other  "Твердое тело1360"
  other  "Твердое тело1361"
  other  "Твердое тело1362"
  other  "Твердое тело1363"
  other  "Твердое тело1364"
  other  "Твердое тело1365"
  other  "Твердое тело1366"
  other  "Твердое тело1367"
  other  "Твердое тело1368"
  other  "Твердое тело1369"
  other  "Твердое тело1370"
  other  "Твердое тело1371"
  other  "Твердое тело1372"
  other  "Твердое тело1373"
  other  "Твердое тело1374"
  other  "Твердое тело1375"
  other  "Твердое тело1376"
  other  "Твердое тело1377"
  other  "Твердое тело1378"
  other  "Твердое тело1379"
  other  "Твердое тело1380"
  other  "Твердое тело1381"
  other  "Твердое тело1382"
  other  "Твердое тело1383"
  other  "Твердое тело1384"
  other  "Твердое тело1385"
  other  "Твердое тело1386"
  other  "Твердое тело1387"
  other  "Твердое тело1388"
  other  "Твердое тело1389"
  other  "Твердое тело1390"
  other  "Твердое тело1391"
  other  "Твердое тело1392"
  other  "Твердое тело1393"
  other  "Твердое тело1394"
  other  "Твердое тело1395"
  other  "Твердое тело1396"
  other  "Твердое тело1397"
  other  "Твердое тело1398"
  other  "Твердое тело1399"
  other  "Твердое тело1400"
  other  "Твердое тело1401"
  other  "Твердое тело1402"
  other  "Твердое тело1403"
  other  "Твердое тело1404"
  other  "Твердое тело1405"
  other  "Твердое тело1406"
  other  "Твердое тело1407"
  other  "Твердое тело1408"
  other  "Твердое тело1409"
  other  "Твердое тело1410"
  other  "Твердое тело1411"
  other  "Твердое тело1412"
  other  "Твердое тело1413"
  other  "Твердое тело1414"
  other  "Твердое тело1415"
  other  "Твердое тело1416"
  other  "Твердое тело1417"
  other  "Твердое тело1418"
  other  "Твердое тело1419"
  other  "Твердое тело1420"
  other  "Твердое тело1421"
  other  "Твердое тело1422"
  other  "Твердое тело1423"
  other  "Твердое тело1424"
  other  "Твердое тело1425"
  other  "Твердое тело1426"
  other  "Твердое тело1427"
  other  "Твердое тело1428"
  other  "Твердое тело1429"
  other  "Твердое тело1430"
  other  "Твердое тело1431"
  other  "Твердое тело1432"
  other  "Твердое тело1433"
  other  "Твердое тело1434"
  other  "Твердое тело1435"
  other  "Твердое тело1436"
  other  "Твердое тело1437"
  other  "Твердое тело1438"
  other  "Твердое тело1439"
  other  "Твердое тело1440"
  other  "Твердое тело1441"
  other  "Твердое тело1442"
  other  "Твердое тело1443"
  other  "Твердое тело1444"
  other  "Твердое тело1445"
  other  "Твердое тело1446"
  other  "Твердое тело1447"
  other  "Твердое тело1448"
  other  "Твердое тело1449"
  other  "Твердое тело1450"
  other  "Твердое тело1451"
  other  "Твердое тело1452"
  other  "Твердое тело1453"
  other  "Твердое тело1454"
  other  "Твердое тело1455"
  other  "Твердое тело1456"
  other  "Твердое тело1457"
  other  "Твердое тело1458"
  other  "Твердое тело1459"
  other  "Твердое тело1460"
  other  "Твердое тело1461"
  other  "Твердое тело1462"
  other  "Твердое тело1463"
  other  "Твердое тело1464"
  other  "Твердое тело1465"
  other  "Твердое тело1466"
  other  "Твердое тело1467"
  other  "Твердое тело1468"
  other  "Твердое тело1469"
  other  "Твердое тело1470"
  other  "Твердое тело1471"
  other  "Твердое тело1472"
  other  "Твердое тело1473"
  other  "Твердое тело1474"
  other  "Твердое тело1475"
  other  "Твердое тело1476"
  other  "Твердое тело1477"
  other  "Твердое тело1478"
  other  "Твердое тело1479"
  other  "Твердое тело1480"
  other  "Твердое тело1481"
  other  "Твердое тело1482"
  other  "Твердое тело1483"
  other  "Твердое тело1484"
  other  "Твердое тело1485"
  other  "Твердое тело1486"
  other  "Твердое тело1487"
  other  "Твердое тело1488"
  other  "Твердое тело1489"
  other  "Твердое тело1490"
  other  "Твердое тело1491"
  other  "Твердое тело1492"
  other  "Твердое тело1493"
  other  "Твердое тело1494"
  other  "Твердое тело1495"
  other  "Твердое тело1496"
  other  "Твердое тело1497"
  other  "Твердое тело1498"
  other  "Твердое тело1499"
  other  "Твердое тело1500"
  other  "Твердое тело1501"
  other  "Твердое тело1502"
  other  "Твердое тело1503"
  other  "Твердое тело1504"
  other  "Твердое тело1505"
  other  "Твердое тело1506"
  other  "Твердое тело1507"
  other  "Твердое тело1508"
  other  "Твердое тело1509"
  other  "Твердое тело1510"
  other  "Твердое тело1511"
  other  "Твердое тело1512"
  other  "Твердое тело1513"
  other  "Твердое тело1514"
  other  "Твердое тело1515"
  other  "Твердое тело1516"
  other  "Твердое тело1517"
  other  "Твердое тело1518"
  other  "Твердое тело1519"
  other  "Твердое тело1520"
  other  "Твердое тело1521"
  other  "Твердое тело1522"
  other  "Твердое тело1523"
  other  "Твердое тело1524"
  other  "Твердое тело1525"
  other  "Твердое тело1526"
  other  "Твердое тело1527"
  other  "Твердое тело1528"
  other  "Твердое тело1529"
  other  "Твердое тело1530"
  other  "Твердое тело1531"
  other  "Твердое тело1532"
  other  "Твердое тело1533"
  other  "Твердое тело1534"
  other  "Твердое тело1535"
  other  "Твердое тело1536"
  other  "Твердое тело1537"
  other  "Твердое тело1538"
  other  "Твердое тело1539"
  other  "Твердое тело1540"
  other  "Твердое тело1541"
  other  "Твердое тело1542"
  other  "Твердое тело1543"
  other  "Твердое тело1544"
  other  "Твердое тело1545"
  other  "Твердое тело1546"
  other  "Твердое тело1547"
  other  "Твердое тело1548"
  other  "Твердое тело1549"
  other  "Твердое тело1550"
  other  "Твердое тело1551"
  other  "Твердое тело1552"
  other  "Твердое тело1553"
  other  "Твердое тело1554"
  other  "Твердое тело1555"
  other  "Твердое тело1556"
  other  "Твердое тело1557"
  other  "Твердое тело1558"
  other  "Твердое тело1559"
  other  "Твердое тело1560"
  other  "Твердое тело1561"
  other  "Твердое тело1562"
  other  "Твердое тело1563"
  other  "Твердое тело1564"
  other  "Твердое тело1565"
  other  "Твердое тело1566"
  other  "Твердое тело1567"
  other  "Твердое тело1568"
  other  "Твердое тело1569"
  other  "Твердое тело1570"
  other  "Твердое тело1571"
  other  "Твердое тело1572"
  other  "Твердое тело1573"
  other  "Твердое тело1574"
  other  "Твердое тело1575"
  other  "Твердое тело1576"
  other  "Твердое тело1577"
  other  "Твердое тело1578"
  other  "Твердое тело1579"
  other  "Твердое тело1580"
  other  "Твердое тело1581"
  other  "Твердое тело1582"
  other  "Твердое тело1583"
  other  "Твердое тело1584"
  other  "Твердое тело1585"
  other  "Твердое тело1586"
  other  "Твердое тело1587"
  other  "Твердое тело1588"
  other  "Твердое тело1589"
  other  "Твердое тело1590"
  other  "Твердое тело1591"
  other  "Твердое тело1592"
  other  "Твердое тело1593"
  other  "Твердое тело1594"
  other  "Твердое тело1595"
  other  "Твердое тело1596"
  other  "Твердое тело1597"
  other  "Твердое тело1598"
  other  "Твердое тело1599"
  other  "Твердое тело1600"
  other  "Твердое тело1601"
  other  "Твердое тело1602"
  other  "Твердое тело1603"
  other  "Твердое тело1604"
  other  "Твердое тело1605"
  other  "Твердое тело1606"
  other  "Твердое тело1607"
  other  "Твердое тело1608"
  other  "Твердое тело1609"
  other  "Твердое тело1610"
  other  "Твердое тело1611"
  other  "Твердое тело1612"
  other  "Твердое тело1613"
  other  "Твердое тело1614"
  other  "Твердое тело1615"
  other  "Твердое тело1616"
  other  "Твердое тело1617"
  other  "Твердое тело1618"
  other  "Твердое тело1619"
  other  "Твердое тело1620"
  other  "Твердое тело1621"
  other  "Твердое тело1622"
  other  "Твердое тело1623"
  other  "Твердое тело1624"
  other  "Твердое тело1625"
  other  "Твердое тело1626"
  other  "Твердое тело1627"
  other  "Твердое тело1628"
  other  "Твердое тело1629"
  other  "Твердое тело1630"
  other  "Твердое тело1631"
  other  "Твердое тело1632"
  other  "Твердое тело1633"
  other  "Твердое тело1634"
  other  "Твердое тело1635"
  other  "Твердое тело1636"
  other  "Твердое тело1637"
  other  "Твердое тело1638"
  other  "Твердое тело1639"
  other  "Твердое тело1640"
  other  "Твердое тело1641"
  other  "Твердое тело1642"
  other  "Твердое тело1643"
  other  "Твердое тело1644"
  other  "Твердое тело1645"
  other  "Твердое тело1646"
  other  "Твердое тело1647"
  other  "Твердое тело1648"
  other  "Твердое тело1649"
  other  "Твердое тело1650"
  other  "Твердое тело1651"
  other  "Твердое тело1652"
  other  "Твердое тело1653"
  other  "Твердое тело1654"
  other  "Твердое тело1655"
  other  "Твердое тело1656"
  other  "Твердое тело1657"
  other  "Твердое тело1658"
  other  "Твердое тело1659"
  other  "Твердое тело1660"
  other  "Твердое тело1661"
  other  "Твердое тело1662"
  other  "Твердое тело1663"
  other  "Твердое тело1664"
  other  "Твердое тело1665"
  other  "Твердое тело1666"
  other  "Твердое тело1667"
  other  "Твердое тело1668"
  other  "Твердое тело1669"
  other  "Твердое тело1670"
  other  "Твердое тело1671"
  other  "Твердое тело1672"
  other  "Твердое тело1673"
  other  "Твердое тело1674"
  other  "Твердое тело1675"
  other  "Твердое тело1676"
  other  "Твердое тело1677"
  other  "Твердое тело1678"
  other  "Твердое тело1679"
  other  "Твердое тело1680"
  other  "Твердое тело1681"
  other  "Твердое тело1682"
  other  "Твердое тело1683"
  other  "Твердое тело1684"
  other  "Твердое тело1685"
  other  "Твердое тело1686"
  other  "Твердое тело1687"
  other  "Твердое тело1688"
  other  "Твердое тело1689"
  other  "Твердое тело1690"
  other  "Твердое тело1691"
  other  "Твердое тело1692"
  other  "Твердое тело1693"
  other  "Твердое тело1694"
  other  "Твердое тело1695"
  other  "Твердое тело1696"
  other  "Твердое тело1697"
  other  "Твердое тело1698"
  other  "Твердое тело1699"
  other  "Твердое тело1700"
  other  "Твердое тело1701"
  other  "Твердое тело1702"
  other  "Твердое тело1703"
  other  "Твердое тело1704"
  other  "Твердое тело1705"
  other  "Твердое тело1706"
  other  "Твердое тело1707"
  other  "Твердое тело1708"
  other  "Твердое тело1709"
  other  "Твердое тело1710"
  other  "Твердое тело1711"
  other  "Твердое тело1712"
  other  "Твердое тело1713"
  other  "Твердое тело1714"
  other  "Твердое тело1715"
  other  "Твердое тело1716"
  other  "Твердое тело1717"
  other  "Твердое тело1718"
  other  "Твердое тело1719"
  other  "Твердое тело1720"
  other  "Твердое тело1721"
  other  "Твердое тело1722"
  other  "Твердое тело1723"
  other  "Твердое тело1724"
  other  "Твердое тело1725"
  other  "Твердое тело1726"
  other  "Твердое тело1727"
  other  "Твердое тело1728"
  other  "Твердое тело1729"
  other  "Твердое тело1730"
  other  "Твердое тело1731"
  other  "Твердое тело1732"
  other  "Твердое тело1733"
  other  "Твердое тело1734"
  other  "Твердое тело1735"
  other  "Твердое тело1736"
  other  "Твердое тело1737"
  other  "Твердое тело1738"
  other  "Твердое тело1739"
  other  "Твердое тело1740"
  other  "Твердое тело1741"
  other  "Твердое тело1742"
  other  "Твердое тело1743"
  other  "Твердое тело1744"
  other  "Твердое тело1745"
  other  "Твердое тело1746"
  other  "Твердое тело1747"
  other  "Твердое тело1748"
  other  "Твердое тело1749"
  other  "Твердое тело1750"
  other  "Твердое тело1751"
  other  "Твердое тело1752"
  other  "Твердое тело1753"
  other  "Твердое тело1754"
  other  "Твердое тело1755"
  other  "Твердое тело1756"
  other  "Твердое тело1757"
  other  "Твердое тело1758"
  other  "Твердое тело1759"
  other  "Твердое тело1760"
  other  "Твердое тело1761"
  other  "Твердое тело1762"
  other  "Твердое тело1763"
  other  "Твердое тело1764"
  other  "Твердое тело1765"
  other  "Твердое тело1766"
  other  "Твердое тело1767"
  other  "Твердое тело1768"
  other  "Твердое тело1769"
  other  "Твердое тело1770"
  other  "Твердое тело1771"
  other  "Твердое тело1772"
  other  "Твердое тело1773"
  other  "Твердое тело1774"
  other  "Твердое тело1775"
  other  "Твердое тело1776"
  other  "Твердое тело1777"
  other  "Твердое тело1778"
  other  "Твердое тело1779"
  other  "Твердое тело1780"
  other  "Твердое тело1781"
  other  "Твердое тело1782"
  other  "Твердое тело1783"
  other  "Твердое тело1784"
  other  "Твердое тело1785"
  other  "Твердое тело1786"
  other  "Твердое тело1787"
  other  "Твердое тело1788"
  other  "Твердое тело1789"
  other  "Твердое тело1790"
  other  "Твердое тело1791"
  other  "Твердое тело1792"
  other  "Твердое тело1793"
  other  "Твердое тело1794"
  other  "Твердое тело1795"
  other  "Твердое тело1796"
  other  "Твердое тело1797"
  other  "Твердое тело1798"
  other  "Твердое тело1799"
  other  "Твердое тело1800"
  other  "Твердое тело1801"
  other  "Твердое тело1802"
  other  "Твердое тело1803"
  other  "Твердое тело1804"
  other  "Твердое тело1805"
  other  "Твердое тело1806"
  other  "Твердое тело1807"
  other  "Твердое тело1808"
  other  "Твердое тело1809"
  other  "Твердое тело1810"
  other  "Твердое тело1811"
  other  "Твердое тело1812"
  other  "Твердое тело1813"
  other  "Твердое тело1814"
  other  "Твердое тело1815"
  sketch  "3D эскиз2440"
  other  "Open CASCADE STEP translator 7.5 2.1.1_65:1"
  extrude  "Extruded_67:1"  [1 undecoded]
  other  "KTD0621_70:1"
  other  "KTD0621_72:1"
  other  "User Library-User Library-res0402_res0402_body_74:1"
  other  "User Library-User Library-res0402_res0402_body_76:1"
  other  "User Library-User Library-res0402_res0402_body_78:1"
  other  "User Library-DF40C-100DP-0_4V(51)_83:1"
  other  "User Library-DF40C-100DP-0_4V(51)_84:1"
  other  "200-ball_VFBGAold.step_85:1"
  other  "200-ball_VFBGAold.step_85:2"
  other  "200-ball_VFBGAold.step_85:3"
  other  "200-ball_VFBGAold.step_85:4"
  other  "200-ball_VFBGAold.step_85:5"
  other  "200-ball_VFBGAold.step_85:6"
  other  "200-ball_VFBGAold.step_85:7"
  other  "200-ball_VFBGAold.step_85:8"
  other  "200-ball_VFBGAold.step_85:9"
  other  "200-ball_VFBGAold.step_85:10"
  other  "200-ball_VFBGAold.step_85:11"
  other  "200-ball_VFBGAold.step_85:12"
  other  "200-ball_VFBGAold.step_85:13"
  other  "200-ball_VFBGAold.step_85:14"
  other  "200-ball_VFBGAold.step_85:15"
  other  "200-ball_VFBGAold.step_85:16"
  other  "200-ball_VFBGAold.step_85:17"
  other  "200-ball_VFBGAold.step_85:18"
  other  "200-ball_VFBGAold.step_85:19"
  other  "200-ball_VFBGAold.step_85:20"
  other  "200-ball_VFBGAold.step_85:21"
  other  "200-ball_VFBGAold.step_85:22"
  other  "200-ball_VFBGAold.step_85:23"
  other  "200-ball_VFBGAold.step_85:24"
  other  "200-ball_VFBGAold.step_85:25"
  other  "200-ball_VFBGAold.step_85:26"
  other  "200-ball_VFBGAold.step_85:27"
  other  "200-ball_VFBGAold.step_85:28"
  other  "200-ball_VFBGAold.step_85:29"
  other  "200-ball_VFBGAold.step_85:30"
  other  "200-ball_VFBGAold.step_85:31"
  other  "200-ball_VFBGAold.step_85:32"
  other  "200-ball_VFBGAold.step_85:33"
  other  "200-ball_VFBGAold.step_85:34"
  other  "200-ball_VFBGAold.step_85:35"
  other  "200-ball_VFBGAold.step_85:36"
  other  "200-ball_VFBGAold.step_85:37"
  other  "200-ball_VFBGAold.step_85:38"
  other  "200-ball_VFBGAold.step_85:39"
  other  "200-ball_VFBGAold.step_85:40"
  other  "200-ball_VFBGAold.step_85:41"
  other  "200-ball_VFBGAold.step_85:42"
  other  "200-ball_VFBGAold.step_85:43"
  other  "200-ball_VFBGAold.step_85:44"
  other  "200-ball_VFBGAold.step_85:45"
  other  "200-ball_VFBGAold.step_85:46"
  other  "200-ball_VFBGAold.step_85:47"
  other  "200-ball_VFBGAold.step_85:48"
  other  "200-ball_VFBGAold.step_85:49"
  other  "200-ball_VFBGAold.step_85:50"
  other  "200-ball_VFBGAold.step_85:51"
  other  "200-ball_VFBGAold.step_85:52"
  other  "200-ball_VFBGAold.step_85:53"
  other  "200-ball_VFBGAold.step_85:54"
  other  "200-ball_VFBGAold.step_85:55"
  other  "200-ball_VFBGAold.step_85:56"
  other  "200-ball_VFBGAold.step_85:57"
  other  "200-ball_VFBGAold.step_85:58"
  other  "200-ball_VFBGAold.step_85:59"
  other  "200-ball_VFBGAold.step_85:60"
  other  "200-ball_VFBGAold.step_85:61"
  other  "200-ball_VFBGAold.step_85:62"
  other  "200-ball_VFBGAold.step_85:63"
  other  "200-ball_VFBGAold.step_85:64"
  other  "200-ball_VFBGAold.step_85:65"
  other  "200-ball_VFBGAold.step_85:66"
  other  "200-ball_VFBGAold.step_85:67"
  other  "200-ball_VFBGAold.step_85:68"
  other  "200-ball_VFBGAold.step_85:69"
  other  "200-ball_VFBGAold.step_85:70"
  other  "200-ball_VFBGAold.step_85:71"
  other  "200-ball_VFBGAold.step_85:72"
  other  "200-ball_VFBGAold.step_85:73"
  other  "200-ball_VFBGAold.step_85:74"
  other  "200-ball_VFBGAold.step_85:75"
  other  "200-ball_VFBGAold.step_85:76"
  other  "200-ball_VFBGAold.step_85:77"
  other  "200-ball_VFBGAold.step_85:78"
  other  "200-ball_VFBGAold.step_85:79"
  other  "200-ball_VFBGAold.step_85:80"
  other  "200-ball_VFBGAold.step_85:81"
  other  "200-ball_VFBGAold.step_85:82"
  other  "200-ball_VFBGAold.step_85:83"
  other  "200-ball_VFBGAold.step_85:84"
  other  "200-ball_VFBGAold.step_85:85"
  other  "200-ball_VFBGAold.step_85:86"
  other  "200-ball_VFBGAold.step_85:87"
  other  "200-ball_VFBGAold.step_85:88"
  other  "200-ball_VFBGAold.step_85:89"
  other  "200-ball_VFBGAold.step_85:90"
  other  "200-ball_VFBGAold.step_85:91"
  other  "200-ball_VFBGAold.step_85:92"
  other  "200-ball_VFBGAold.step_85:93"
  other  "200-ball_VFBGAold.step_85:94"
  other  "200-ball_VFBGAold.step_85:95"
  other  "200-ball_VFBGAold.step_85:96"
  other  "200-ball_VFBGAold.step_85:97"
  other  "200-ball_VFBGAold.step_85:98"
  other  "200-ball_VFBGAold.step_85:99"
  other  "200-ball_VFBGAold.step_85:100"
  other  "200-ball_VFBGAold.step_85:101"
  other  "200-ball_VFBGAold.step_85:102"
  other  "200-ball_VFBGAold.step_85:103"
  other  "200-ball_VFBGAold.step_85:104"
  other  "200-ball_VFBGAold.step_85:105"
  other  "200-ball_VFBGAold.step_85:106"
  other  "200-ball_VFBGAold.step_85:107"
  other  "200-ball_VFBGAold.step_85:108"
  other  "200-ball_VFBGAold.step_85:109"
  other  "200-ball_VFBGAold.step_85:110"
  other  "200-ball_VFBGAold.step_85:111"
  other  "200-ball_VFBGAold.step_85:112"
  other  "200-ball_VFBGAold.step_85:113"
  other  "200-ball_VFBGAold.step_85:114"
  other  "200-ball_VFBGAold.step_85:115"
  other  "200-ball_VFBGAold.step_85:116"
  other  "200-ball_VFBGAold.step_85:117"
  other  "200-ball_VFBGAold.step_85:118"
  other  "200-ball_VFBGAold.step_85:119"
  other  "200-ball_VFBGAold.step_85:120"
  other  "200-ball_VFBGAold.step_85:121"
  other  "200-ball_VFBGAold.step_85:122"
  other  "200-ball_VFBGAold.step_85:123"
  other  "200-ball_VFBGAold.step_85:124"
  other  "200-ball_VFBGAold.step_85:125"
  other  "200-ball_VFBGAold.step_85:126"
  other  "200-ball_VFBGAold.step_85:127"
  other  "200-ball_VFBGAold.step_85:128"
  other  "200-ball_VFBGAold.step_85:129"
  other  "200-ball_VFBGAold.step_85:130"
  other  "200-ball_VFBGAold.step_85:131"
  other  "200-ball_VFBGAold.step_85:132"
  other  "200-ball_VFBGAold.step_85:133"
  other  "200-ball_VFBGAold.step_85:134"
  other  "200-ball_VFBGAold.step_85:135"
  other  "200-ball_VFBGAold.step_85:136"
  other  "200-ball_VFBGAold.step_85:137"
  other  "200-ball_VFBGAold.step_85:138"
  other  "200-ball_VFBGAold.step_85:139"
  other  "200-ball_VFBGAold.step_85:140"
  other  "200-ball_VFBGAold.step_85:141"
  other  "200-ball_VFBGAold.step_85:142"
  other  "200-ball_VFBGAold.step_85:143"
  other  "200-ball_VFBGAold.step_85:144"
  other  "200-ball_VFBGAold.step_85:145"
  other  "200-ball_VFBGAold.step_85:146"
  other  "200-ball_VFBGAold.step_85:147"
  other  "200-ball_VFBGAold.step_85:148"
  other  "200-ball_VFBGAold.step_85:149"
  other  "200-ball_VFBGAold.step_85:150"
  other  "200-ball_VFBGAold.step_85:151"
  other  "200-ball_VFBGAold.step_85:152"
  other  "200-ball_VFBGAold.step_85:153"
  other  "200-ball_VFBGAold.step_85:154"
  other  "200-ball_VFBGAold.step_85:155"
  other  "200-ball_VFBGAold.step_85:156"
  other  "200-ball_VFBGAold.step_85:157"
  other  "200-ball_VFBGAold.step_85:158"
  other  "200-ball_VFBGAold.step_85:159"
  other  "200-ball_VFBGAold.step_85:160"
  other  "200-ball_VFBGAold.step_85:161"
  other  "200-ball_VFBGAold.step_85:162"
  other  "200-ball_VFBGAold.step_85:163"
  other  "200-ball_VFBGAold.step_85:164"
  other  "200-ball_VFBGAold.step_85:165"
  other  "200-ball_VFBGAold.step_85:166"
  other  "200-ball_VFBGAold.step_85:167"
  other  "200-ball_VFBGAold.step_85:168"
  other  "200-ball_VFBGAold.step_85:169"
  other  "200-ball_VFBGAold.step_85:170"
  other  "200-ball_VFBGAold.step_85:171"
  other  "200-ball_VFBGAold.step_85:172"
  other  "200-ball_VFBGAold.step_85:173"
  other  "200-ball_VFBGAold.step_85:174"
  other  "200-ball_VFBGAold.step_85:175"
  other  "200-ball_VFBGAold.step_85:176"
  other  "200-ball_VFBGAold.step_85:177"
  other  "200-ball_VFBGAold.step_85:178"
  other  "200-ball_VFBGAold.step_85:179"
  other  "200-ball_VFBGAold.step_85:180"
  other  "200-ball_VFBGAold.step_85:181"
  other  "200-ball_VFBGAold.step_85:182"
  other  "200-ball_VFBGAold.step_85:183"
  other  "200-ball_VFBGAold.step_85:184"
  other  "200-ball_VFBGAold.step_85:185"
  other  "200-ball_VFBGAold.step_85:186"
  other  "200-ball_VFBGAold.step_85:187"
  other  "200-ball_VFBGAold.step_85:188"
  other  "200-ball_VFBGAold.step_85:189"
  other  "200-ball_VFBGAold.step_85:190"
  other  "200-ball_VFBGAold.step_85:191"
  other  "200-ball_VFBGAold.step_85:192"
  other  "200-ball_VFBGAold.step_85:193"
  other  "200-ball_VFBGAold.step_85:194"
  other  "200-ball_VFBGAold.step_85:195"
  other  "200-ball_VFBGAold.step_85:196"
  other  "200-ball_VFBGAold.step_85:197"
  other  "200-ball_VFBGAold.step_85:198"
  other  "200-ball_VFBGAold.step_85:199"
  other  "200-ball_VFBGAold.step_85:200"
  other  "200-ball_VFBGAold.step_85:201"
  other  "CAP0201.step_87:1"
  other  "CAP0201.step_89:1"
  other  "CAP0201.step_91:1"
  other  "CAP0201.step_93:1"
  other  "CAP0201.step_95:1"
  other  "CAP0201.step_97:1"
  other  "CAP0201.step_99:1"
  other  "CAP0201.step_101:1"
  other  "CAP0201.step_103:1"
  other  "CAP0201.step_105:1"
  other  "CAP0201.step_107:1"
  other  "CAP0201.step_109:1"
  other  "CAP0201.step_111:1"
  other  "CAP0201.step_113:1"
  other  "CAP0201.step_115:1"
  other  "CAP0201.step_117:1"
  other  "CAP0201.step_119:1"
  other  "CAP0201.step_121:1"
  other  "CAP0201.step_123:1"
  other  "CAP0201.step_125:1"
  other  "CAP0201.step_127:1"
  other  "CAP0201.step_129:1"
  other  "CAP0201.step_131:1"
  other  "CAP0201.step_133:1"
  other  "CAP0201.step_135:1"
  other  "CAP0201.step_137:1"
  other  "CAP0201.step_139:1"
  other  "CAP0201.step_141:1"
  other  "CAP0201.step_143:1"
  other  "CAP0201.step_145:1"
  other  "CAP0201.step_147:1"
  other  "CAP0201.step_149:1"
  other  "CAP0201.step_151:1"
  other  "RES0201old.step_153:1"
  other  "RES0201old.step_153:2"
  other  "RES0201old.step_155:1"
  other  "RES0201old.step_155:2"
  other  "RES0201old.step_157:1"
  other  "RES0201old.step_157:2"
  other  "RES0201old.step_159:1"
  other  "RES0201old.step_159:2"
  other  "RES0201old.step_161:1"
  other  "RES0201old.step_161:2"
  other  "RES0201old.step_163:1"
  other  "RES0201old.step_163:2"
  other  "RES0201old.step_165:1"
  other  "RES0201old.step_165:2"
  other  "RES0201old.step_167:1"
  other  "RES0201old.step_167:2"
  other  "RES0201old.step_169:1"
  other  "RES0201old.step_169:2"
  other  "RES0201old.step_171:1"
  other  "RES0201old.step_171:2"
  other  "RES0201old.step_173:1"
  other  "RES0201old.step_173:2"
  other  "RES0201old.step_175:1"
  other  "RES0201old.step_175:2"
  other  "RES0201old.step_177:1"
  other  "RES0201old.step_177:2"
  other  "RES0201old.step_179:1"
  other  "RES0201old.step_179:2"
  other  "CAP0402.step_181:1"
  other  "CAP0402.step_183:1"
  other  "CAP0402.step_185:1"
  other  "CAP0402.step_187:1"
  other  "CAP0402.step_189:1"
  other  "CAP0402.step_191:1"
  other  "CAP0402.step_193:1"
  other  "CAP0402.step_195:1"
  other  "CAP0402.step_197:1"
  other  "CAP0402.step_199:1"
  other  "CAP0402.step_201:1"
  other  "CAP0402.step_203:1"
  other  "CAP0402.step_205:1"
  other  "CAP0402.step_207:1"
  other  "CAP0402.step_209:1"
  other  "CAP0402.step_211:1"
  other  "CAP0402.step_213:1"
  other  "CAP0402.step_215:1"
  other  "CAP0402.step_217:1"
  other  "CAP0402.step_219:1"
  other  "CAP0402.step_221:1"
  other  "CAP0402.step_223:1"
  other  "PMIC STEP.STEP_225:1"
  other  "3D-SRP201208-R47MH-20230512 .step_227:1"
  other  "3D-SRP201208-R47MH-20230512 .step_227:2"
  other  "3D-SRP201208-R47MH-20230512 .step_227:3"
  other  "3D-SRP201208-R47MH-20230512 .step_229:1"
  other  "3D-SRP201208-R47MH-20230512 .step_229:2"
  other  "3D-SRP201208-R47MH-20230512 .step_229:3"
  other  "3D-SRP201208-R47MH-20230512 .step_231:1"
  other  "3D-SRP201208-R47MH-20230512 .step_231:2"
  other  "3D-SRP201208-R47MH-20230512 .step_231:3"
  other  "3D-SRP201208-R47MH-20230512 .step_233:1"
  other  "3D-SRP201208-R47MH-20230512 .step_233:2"
  other  "3D-SRP201208-R47MH-20230512 .step_233:3"
  other  "3D-SRP201208-R47MH-20230512 .step_235:1"
  other  "3D-SRP201208-R47MH-20230512 .step_235:2"
  other  "3D-SRP201208-R47MH-20230512 .step_235:3"
  other  "3D-SRP201208-R47MH-20230512 .step_237:1"
  other  "3D-SRP201208-R47MH-20230512 .step_237:2"
  other  "3D-SRP201208-R47MH-20230512 .step_237:3"
  other  "3D-SRP201208-R47MH-20230512 .step_239:1"
  other  "3D-SRP201208-R47MH-20230512 .step_239:2"
  other  "3D-SRP201208-R47MH-20230512 .step_239:3"
  other  "body_241:1"
  other  "term2_242:1"
  other  "term1_243:1"
  other  "body_241:2"
  other  "term2_242:2"
  other  "term1_243:2"
  other  "body_241:3"
  other  "term2_242:3"
  other  "term1_243:3"
  other  "body_241:4"
  other  "term2_242:4"
  other  "term1_243:4"
  other  "2712 v2 STEP.STEP_253:1"
  other  "2712 v2 STEP.STEP_253:2"
  other  "2712 v2 STEP.STEP_253:3"
  other  "CAP0603.step_255:1"
  other  "CAP0603.step_257:1"
  other  "CAP0603.step_259:1"
  other  "CAP0603.step_261:1"
  other  "RES0402.step_263:1"
  other  "RES0402.step_263:2"
  other  "RES0402.step_263:3"
  other  "RES0402.step_263:4"
  other  "RES0402.step_265:1"
  other  "RES0402.step_265:2"
  other  "RES0402.step_265:3"
  other  "RES0402.step_265:4"
  other  "RES0402.step_267:1"
  other  "RES0402.step_267:2"
  other  "RES0402.step_267:3"
  other  "RES0402.step_267:4"
  other  "RES0402.step_269:1"
  other  "RES0402.step_269:2"
  other  "RES0402.step_269:3"
  other  "RES0402.step_269:4"
  other  "RES0402.step_271:1"
  other  "RES0402.step_271:2"
  other  "RES0402.step_271:3"
  other  "RES0402.step_271:4"
  other  "RES0402.step_273:1"
  other  "RES0402.step_273:2"
  other  "RES0402.step_273:3"
  other  "RES0402.step_273:4"
  other  "RES0402.step_275:1"
  other  "RES0402.step_275:2"
  other  "RES0402.step_275:3"
  other  "RES0402.step_275:4"
  other  "RES0402.step_277:1"
  other  "RES0402.step_277:2"
  other  "RES0402.step_277:3"
  other  "RES0402.step_277:4"
  other  "RES0402.step_279:1"
  other  "RES0402.step_279:2"
  other  "RES0402.step_279:3"
  other  "RES0402.step_279:4"
  other  "RES0402.step_281:1"
  other  "RES0402.step_281:2"
  other  "RES0402.step_281:3"
  other  "RES0402.step_281:4"
  other  "CAP0201.step_283:1"
  other  "CAP0201.step_285:1"
  other  "CAP0201.step_287:1"
  other  "CAP0201.step_289:1"
  other  "CAP0201.step_291:1"
  other  "CAP0201.step_293:1"
  other  "SOT883B Mold body_295:1"
  other  "SOT883B4 LF_296:1"
  other  "SOT883B4 LF_296:2"
  other  "SOT883B4 LF_296:3"
  other  "SOT883B4 LF_296:4"
  other  "SOT883B4 LF_296:5"
  other  "SOT883B4 LF_296:6"
  other  "SOT883B4 LF_296:7"
  other  "SOT883B4 LF_296:8"
  other  "SOT883B4 LF_296:9"
  other  "SOT883B4 LF_296:10"
  other  "SOT883B4 LF_296:11"
  other  "SOT883B4 LF_296:12"
  other  "SOT883B4 LF_296:13"
  other  "SOT883B Mold body_295:2"
  other  "SOT883B4 LF_296:14"
  other  "SOT883B4 LF_296:15"
  other  "SOT883B4 LF_296:16"
  other  "SOT883B4 LF_296:17"
  other  "SOT883B4 LF_296:18"
  other  "SOT883B4 LF_296:19"
  other  "SOT883B4 LF_296:20"
  other  "SOT883B4 LF_296:21"
  other  "SOT883B4 LF_296:22"
  other  "SOT883B4 LF_296:23"
  other  "SOT883B4 LF_296:24"
  other  "SOT883B4 LF_296:25"
  other  "SOT883B4 LF_296:26"
  other  "ProjectY v3 STEP.STEP_304:1"
  other  "(Unsaved)_306:1"
  other  "(Unsaved)_306:2"
  other  "(Unsaved)_306:3"
  other  "(Unsaved)_306:4"
  other  "(Unsaved)_306:5"
  other  "(Unsaved)_306:6"
  other  "(Unsaved)_306:7"
  other  "(Unsaved)_306:8"
  other  "(Unsaved)_306:9"
  other  "(Unsaved)_306:10"
  other  "(Unsaved)_306:11"
  other  "(Unsaved)_306:12"
  other  "(Unsaved)_306:13"
  other  "(Unsaved)_306:14"
  other  "(Unsaved)_306:15"
  other  "(Unsaved)_306:16"
  other  "(Unsaved)_306:17"
  other  "(Unsaved)_306:18"
  other  "(Unsaved)_306:19"
  other  "(Unsaved)_306:20"
  other  "(Unsaved)_306:21"
  other  "(Unsaved)_306:22"
  other  "(Unsaved)_306:23"
  other  "(Unsaved)_306:24"
  other  "(Unsaved)_306:25"
  other  "(Unsaved)_306:26"
  other  "(Unsaved)_306:27"
  other  "(Unsaved)_306:28"
  other  "(Unsaved)_306:29"
  other  "(Unsaved)_306:30"
  other  "(Unsaved)_306:31"
  other  "(Unsaved)_306:32"
  other  "(Unsaved)_306:33"
  other  "(Unsaved)_306:34"
  other  "(Unsaved)_306:35"
  other  "(Unsaved)_306:36"
  other  "(Unsaved)_306:37"
  other  "(Unsaved)_306:38"
  other  "(Unsaved)_306:39"
  other  "(Unsaved)_306:40"
  other  "(Unsaved)_306:41"
  other  "(Unsaved)_306:42"
  other  "(Unsaved)_306:43"
  other  "(Unsaved)_306:44"
  other  "(Unsaved)_306:45"
  other  "(Unsaved)_306:46"
  other  "(Unsaved)_306:47"
  other  "(Unsaved)_306:48"
  other  "(Unsaved)_306:49"
  other  "(Unsaved)_306:50"
  other  "(Unsaved)_306:51"
  other  "Box_308:1"
  other  "Box_308:2"
  other  "Fusion_310:1"
  other  "CAP0201.step_315:1"
  other  "CAP0201.step_317:1"
  other  "CAP0201.step_319:1"
  other  "CAP0201.step_321:1"
  other  "CAP0201.step_323:1"
  other  "CAP0201.step_325:1"
  other  "CAP0201.step_327:1"
  other  "CAP0201.step_329:1"
  other  "CAP0201.step_331:1"
  other  "CAP0201.step_333:1"
  other  "CAP0201.step_335:1"
  other  "CAP0201.step_337:1"
  other  "CAP0201.step_339:1"
  other  "CAP0201.step_341:1"
  other  "CAP0201.step_343:1"
  other  "CAP0201.step_345:1"
  other  "CAP0201.step_347:1"
  other  "CAP0201.step_349:1"
  other  "CAP0201.step_351:1"
  other  "CAP0201.step_353:1"
  other  "CAP0201.step_355:1"
  other  "CAP0201.step_357:1"
  other  "CAP0201.step_359:1"
  other  "CAP0201.step_361:1"
  other  "CAP0201.step_363:1"
  other  "CAP0201.step_365:1"
  other  "CAP0201.step_367:1"
  other  "CAP0201.step_369:1"
  other  "CAP0201.step_371:1"
  other  "CAP0201.step_373:1"
  other  "CAP0201.step_375:1"
  other  "CAP0201.step_377:1"
  other  "CAP0201.step_379:1"
  other  "CAP0201.step_381:1"
  other  "CAP0201.step_383:1"
  other  "CAP0201.step_385:1"
  other  "CAP0201.step_387:1"
  other  "CAP0201.step_389:1"
  other  "CAP0201.step_391:1"
  other  "CAP0201.step_393:1"
  other  "CAP0201.step_395:1"
  other  "CAP0201.step_397:1"
  other  "CAP0201.step_399:1"
  other  "CAP0201.step_401:1"
  other  "CAP0201.step_403:1"
  other  "CAP0201.step_405:1"
  other  "CAP0201.step_407:1"
  other  "CAP0201.step_409:1"
  other  "CAP0201.step_411:1"
  other  "CAP0201.step_413:1"
  other  "CAP0201.step_415:1"
  other  "CAP0201.step_417:1"
  other  "CAP0201.step_419:1"
  other  "CAP0201.step_421:1"
  other  "CAP0201.step_423:1"
  other  "CAP0201.step_425:1"
  other  "CAP0201.step_427:1"
  other  "CAP0201.step_429:1"
  other  "CAP0201.step_431:1"
  other  "CAP0201.step_433:1"
  other  "CAP0201.step_435:1"
  other  "CAP0201.step_437:1"
  other  "CAP0201.step_439:1"
  other  "CAP0201.step_441:1"
  other  "CAP0201.step_443:1"
  other  "CAP0201.step_445:1"
  other  "CAP0201.step_447:1"
  other  "CAP0201.step_449:1"
  other  "CAP0201.step_451:1"
  other  "CAP0201.step_453:1"
  other  "CAP0201.step_455:1"
  other  "CAP0201.step_457:1"
  other  "CAP0201.step_459:1"
  other  "CAP0201.step_461:1"
  other  "CAP0201.step_463:1"
  other  "CAP0201.step_465:1"
  other  "CAP0201.step_467:1"
  other  "CAP0201.step_469:1"
  other  "CAP0201.step_471:1"
  other  "CAP0201.step_473:1"
  other  "CAP0201.step_475:1"
  other  "CAP0201.step_477:1"
  other  "CAP0201.step_479:1"
  other  "CAP0201.step_481:1"
  other  "CAP0201.step_483:1"
  other  "CAP0201.step_485:1"
  other  "CAP0201.step_487:1"
  other  "CAP0201.step_489:1"
  other  "CAP0201.step_491:1"
  other  "CAP0201.step_493:1"
  other  "CAP0201.step_495:1"
  other  "CAP0201.step_497:1"
  other  "CAP0201.step_499:1"
  other  "CAP0201.step_501:1"
  other  "CAP0201.step_503:1"
  other  "CAP0201.step_505:1"
  other  "CAP0201.step_507:1"
  other  "CAP0201.step_509:1"
  other  "CAP0201.step_511:1"
  other  "CAP0201.step_513:1"
  other  "CAP0201.step_515:1"
  other  "CAP0201.step_517:1"
  other  "CAP0201.step_519:1"
  other  "CAP0201.step_521:1"
  other  "CAP0201.step_523:1"
  other  "CAP0201.step_525:1"
  other  "CAP0201.step_527:1"
  other  "CAP0201.step_529:1"
  other  "CAP0201.step_531:1"
  other  "CAP0201.step_533:1"
  other  "CAP0201.step_535:1"
  other  "CAP0201.step_537:1"
  other  "CAP0201.step_539:1"
  other  "CAP0201.step_541:1"
  other  "CAP0201.step_543:1"
  other  "CAP0201.step_545:1"
  other  "CAP0201.step_547:1"
  other  "CAP0201.step_549:1"
  other  "CAP0201.step_551:1"
  other  "CAP0201.step_553:1"
  other  "CAP0201.step_555:1"
  other  "CAP0201.step_557:1"
  other  "CAP0201.step_559:1"
  other  "CAP0201.step_561:1"
  other  "CAP0201.step_563:1"
  other  "CAP0201.step_565:1"
  other  "CAP0201.step_567:1"
  other  "CAP0201.step_569:1"
  other  "CAP0201.step_571:1"
  other  "CAP0201.step_573:1"
  other  "CAP0201.step_575:1"
  other  "CAP0201.step_577:1"
  other  "CAP0201.step_579:1"
  other  "CAP0201.step_581:1"
  other  "CAP0201.step_583:1"
  other  "CAP0201.step_585:1"
  other  "CAP0201.step_587:1"
  other  "CAP0201.step_589:1"
  other  "CAP0201.step_591:1"
  other  "CAP0201.step_593:1"
  other  "CAP0201.step_595:1"
  other  "CAP0201.step_597:1"
  other  "CAP0201.step_599:1"
  other  "CAP0201.step_601:1"
  other  "CAP0201.step_603:1"
  other  "CAP0201.step_605:1"
  other  "CAP0201.step_607:1"
  other  "CAP0201.step_609:1"
  other  "CAP0201.step_611:1"
  other  "CAP0201.step_613:1"
  other  "CAP0201.step_615:1"
  other  "RES0201old.step_617:1"
  other  "RES0201old.step_617:2"
  other  "RES0201old.step_619:1"
  other  "RES0201old.step_619:2"
  other  "RES0201old.step_621:1"
  other  "RES0201old.step_621:2"
  other  "RES0201old.step_623:1"
  other  "RES0201old.step_623:2"
  other  "RES0201old.step_625:1"
  other  "RES0201old.step_625:2"
  other  "RES0201old.step_627:1"
  other  "RES0201old.step_627:2"
  other  "RES0201old.step_629:1"
  other  "RES0201old.step_629:2"
  other  "RES0201old.step_631:1"
  other  "RES0201old.step_631:2"
  other  "RES0201old.step_633:1"
  other  "RES0201old.step_633:2"
  other  "RES0201old.step_635:1"
  other  "RES0201old.step_635:2"
  other  "RES0201old.step_637:1"
  other  "RES0201old.step_637:2"
  other  "RES0201old.step_639:1"
  other  "RES0201old.step_639:2"
  other  "RES0201old.step_641:1"
  other  "RES0201old.step_641:2"
  other  "RES0201old.step_643:1"
  other  "RES0201old.step_643:2"
  other  "RES0201old.step_645:1"
  other  "RES0201old.step_645:2"
  other  "RES0201old.step_647:1"
  other  "RES0201old.step_647:2"
  other  "RES0201old.step_649:1"
  other  "RES0201old.step_649:2"
  other  "RES0201old.step_651:1"
  other  "RES0201old.step_651:2"
  other  "RES0201old.step_653:1"
  other  "RES0201old.step_653:2"
  other  "RES0201old.step_655:1"
  other  "RES0201old.step_655:2"
  other  "RES0201old.step_657:1"
  other  "RES0201old.step_657:2"
  other  "RES0201old.step_659:1"
  other  "RES0201old.step_659:2"
  other  "RES0201old.step_661:1"
  other  "RES0201old.step_661:2"
  other  "RES0201old.step_663:1"
  other  "RES0201old.step_663:2"
  other  "RES0201old.step_665:1"
  other  "RES0201old.step_665:2"
  other  "RES0201old.step_667:1"
  other  "RES0201old.step_667:2"
  other  "RES0201old.step_669:1"
  other  "RES0201old.step_669:2"
  other  "RES0201old.step_671:1"
  other  "RES0201old.step_671:2"
  other  "RES0201old.step_673:1"
  other  "RES0201old.step_673:2"
  other  "RES0201old.step_675:1"
  other  "RES0201old.step_675:2"
  other  "RES0201old.step_677:1"
  other  "RES0201old.step_677:2"
  other  "RES0201old.step_679:1"
  other  "RES0201old.step_679:2"
  other  "RES0201old.step_681:1"
  other  "RES0201old.step_681:2"
  other  "RES0201old.step_683:1"
  other  "RES0201old.step_683:2"
  other  "RES0201old.step_685:1"
  other  "RES0201old.step_685:2"
  other  "RES0201old.step_687:1"
  other  "RES0201old.step_687:2"
  other  "RES0201old.step_689:1"
  other  "RES0201old.step_689:2"
  other  "RES0201old.step_691:1"
  other  "RES0201old.step_691:2"
  other  "RES0201old.step_693:1"
  other  "RES0201old.step_693:2"
  other  "RES0201old.step_695:1"
  other  "RES0201old.step_695:2"
  other  "RES0201old.step_697:1"
  other  "RES0201old.step_697:2"
  other  "RES0201old.step_699:1"
  other  "RES0201old.step_699:2"
  other  "RES0201old.step_701:1"
  other  "RES0201old.step_701:2"
  other  "RES0201old.step_703:1"
  other  "RES0201old.step_703:2"
  other  "RES0201old.step_705:1"
  other  "RES0201old.step_705:2"
  other  "RES0201old.step_707:1"
  other  "RES0201old.step_707:2"
  other  "RES0201old.step_709:1"
  other  "RES0201old.step_709:2"
  other  "RES0201old.step_711:1"
  other  "RES0201old.step_711:2"
  other  "RES0201old.step_713:1"
  other  "RES0201old.step_713:2"
  other  "RES0201old.step_715:1"
  other  "RES0201old.step_715:2"
  other  "RES0201old.step_717:1"
  other  "RES0201old.step_717:2"
  other  "RES0201old.step_719:1"
  other  "RES0201old.step_719:2"
  other  "RES0201old.step_721:1"
  other  "RES0201old.step_721:2"
  other  "RES0201old.step_723:1"
  other  "RES0201old.step_723:2"
  other  "RES0201old.step_725:1"
  other  "RES0201old.step_725:2"
  other  "RES0201old.step_727:1"
  other  "RES0201old.step_727:2"
  other  "RES0201old.step_729:1"
  other  "RES0201old.step_729:2"
  other  "PinIndicator_731:1"
  other  "Pads_732:1"
  other  "Lid_733:1"
  other  "Body_734:1"
  other  "Pad001_738:1"
  other  "Cut_739:1"
  other  "Cut_739:2"
  other  "Pad001_738:2"
  other  "Cut_739:3"
  other  "Cut_739:4"
  other  "Pad001_738:3"
  other  "Cut_739:5"
  other  "Cut_739:6"
  other  "Pad001_738:4"
  other  "Cut_739:7"
  other  "Cut_739:8"
  other  "Pad001_738:5"
  other  "Cut_739:9"
  other  "Cut_739:10"
  other  "Pad001_738:6"
  other  "Cut_739:11"
  other  "Cut_739:12"
  other  "Pad001_738:7"
  other  "Cut_739:13"
  other  "Cut_739:14"
  other  "Pad001_738:8"
  other  "Cut_739:15"
  other  "Cut_739:16"
  other  "Pad001_738:9"
  other  "Cut_739:17"
  other  "Cut_739:18"
  other  "Pad001_738:10"
  other  "Cut_739:19"
  other  "Cut_739:20"
  other  "Pad001_738:11"
  other  "Cut_739:21"
  other  "Cut_739:22"
  other  "Pad001_738:12"
  other  "Cut_739:23"
  other  "Cut_739:24"
  other  "Pad001_738:13"
  other  "Cut_739:25"
  other  "Cut_739:26"
  other  "Pad001_738:14"
  other  "Cut_739:27"
  other  "Cut_739:28"
  other  "Pad001_738:15"
  other  "Cut_739:29"
  other  "Cut_739:30"
  other  "Pad001_738:16"
  other  "Cut_739:31"
  other  "Cut_739:32"
  other  "Pad001_738:17"
  other  "Cut_739:33"
  other  "Cut_739:34"
  other  "Pad001_738:18"
  other  "Cut_739:35"
  other  "Cut_739:36"
  other  "Pad001_738:19"
  other  "Cut_739:37"
  other  "Cut_739:38"
  other  "Pad001_738:20"
  other  "Cut_739:39"
  other  "Cut_739:40"
  other  "Pad001_738:21"
  other  "Cut_739:41"
  other  "Cut_739:42"
  other  "Pad001_738:22"
  other  "Cut_739:43"
  other  "Cut_739:44"
  other  "CAP0402.step_785:1"
  other  "CAP0402.step_787:1"
  other  "CAP0402.step_789:1"
  other  "CAP0402.step_791:1"
  other  "CAP0402.step_793:1"
  other  "CAP0402.step_795:1"
  other  "CAP0402.step_797:1"
  other  "CAP0402.step_799:1"
  other  "CAP0402.step_801:1"
  other  "CAP0402.step_803:1"
  other  "CAP0402.step_805:1"
  other  "CAP0402.step_807:1"
  other  "CAP0402.step_809:1"
  other  "CAP0402.step_811:1"
  other  "CAP0402.step_813:1"
  other  "CAP0402.step_815:1"
  other  "CAP0402.step_817:1"
  other  "CAP0402.step_819:1"
  other  "CAP0402.step_821:1"
  other  "CAP0402.step_823:1"
  other  "CAP0402.step_825:1"
  other  "CAP0402.step_827:1"
  other  "CAP0402.step_829:1"
  other  "CAP0402.step_831:1"
  other  "CAP0402.step_833:1"
  other  "CAP0402.step_835:1"
  other  "CAP0402.step_837:1"
  other  "CAP0402.step_839:1"
  other  "CAP0402.step_841:1"
  other  "CAP0402.step_843:1"
  other  "CAP0402.step_845:1"
  other  "CAP0402.step_847:1"
  other  "CAP0402.step_849:1"
  other  "CAP0402.step_851:1"
  other  "CAP0402.step_853:1"
  other  "CAP0402.step_855:1"
  other  "CAP0402.step_857:1"
  other  "CAP0402.step_859:1"
  other  "CAP0402.step_861:1"
  other  "CAP0402.step_863:1"
  other  "CAP0402.step_865:1"
  other  "CAP0402.step_867:1"
  other  "CAP0402.step_869:1"
  other  "CAP0402.step_871:1"
  other  "CAP0402.step_873:1"
  other  "CAP0402.step_875:1"
  other  "CAP0402.step_877:1"
  other  "CAP0402.step_879:1"
  other  "CAP0402.step_881:1"
  other  "CAP0402.step_883:1"
  other  "CAP0402.step_885:1"
  other  "CAP0402.step_887:1"
  other  "CAP0402.step_889:1"
  other  "CAP0402.step_891:1"
  other  "CAP0402.step_893:1"
  other  "CAP0402.step_895:1"
  other  "CAP0402.step_897:1"
  other  "CAP0402.step_899:1"
  other  "CAP0402.step_901:1"
  other  "Plating_903:1"
  other  "Plating_903:2"
  other  "Plating_903:3"
  other  "Plating_903:4"
  other  "Plating_903:5"
  other  "LDF_904:1"
  other  "LDF_904:2"
  other  "LDF_904:3"
  other  "LDF_904:4"
  other  "LDF_904:5"
  other  "CPD_905:1"
  other  "Pads_909:1"
  other  "Lid_910:1"
  other  "Body_911:1"
  other  "Pins_915:1"
  other  "Pins_915:2"
  other  "Pins_915:3"
  other  "Pins_915:4"
  other  "Pins_915:5"
  other  "Pins_915:6"
  other  "Pins_915:7"
  other  "Pins_915:8"
  other  "Body_916:1"
  other  "CAP0603.step_920:1"
  other  "CAP0603.step_922:1"
  other  "CAP0603.step_924:1"
  other  "CAP0603.step_926:1"
  other  "CAP0603.step_928:1"
  other  "CAP0603.step_930:1"
  other  "Part_18370_932:1"
  other  "Part_739_933:1"
  other  "Part_740_934:1"
  other  "Part_665_935:1"
  other  "Part_637_936:1"
  other  "Part_609_937:1"
  other  "Part_581_938:1"
  other  "Part_553_939:1"
  other  "Part_525_940:1"
  other  "Part_496_941:1"
  other  "SOT883B Mold body_295:3"
  other  "SOT883B4 LF_296:27"
  other  "SOT883B4 LF_296:28"
  other  "SOT883B4 LF_296:29"
  other  "SOT883B4 LF_296:30"
  other  "SOT883B4 LF_296:31"
  other  "SOT883B4 LF_296:32"
  other  "SOT883B4 LF_296:33"
  other  "SOT883B4 LF_296:34"
  other  "SOT883B4 LF_296:35"
  other  "SOT883B4 LF_296:36"
  other  "SOT883B4 LF_296:37"
  other  "SOT883B4 LF_296:38"
  other  "SOT883B4 LF_296:39"
  other  "SOT883B Mold body_295:4"
  other  "SOT883B4 LF_296:40"
  other  "SOT883B4 LF_296:41"
  other  "SOT883B4 LF_296:42"
  other  "SOT883B4 LF_296:43"
  other  "SOT883B4 LF_296:44"
  other  "SOT883B4 LF_296:45"
  other  "SOT883B4 LF_296:46"
  other  "SOT883B4 LF_296:47"
  other  "SOT883B4 LF_296:48"
  other  "SOT883B4 LF_296:49"
  other  "SOT883B4 LF_296:50"
  other  "SOT883B4 LF_296:51"
  other  "SOT883B4 LF_296:52"
  other  "User Library-153BallWFBGA_949:1"
  other  "User Library-153BallWFBGA_949:2"
  other  "User Library-153BallWFBGA_949:3"
  other  "User Library-153BallWFBGA_949:4"
  other  "User Library-153BallWFBGA_949:5"
  other  "User Library-153BallWFBGA_949:6"
  other  "User Library-153BallWFBGA_949:7"
  other  "User Library-153BallWFBGA_949:8"
  other  "User Library-153BallWFBGA_949:9"
  other  "User Library-153BallWFBGA_949:10"
  other  "User Library-153BallWFBGA_949:11"
  other  "User Library-153BallWFBGA_949:12"
  other  "User Library-153BallWFBGA_949:13"
  other  "User Library-153BallWFBGA_949:14"
  other  "User Library-153BallWFBGA_949:15"
  other  "User Library-153BallWFBGA_949:16"
  other  "User Library-153BallWFBGA_949:17"
  other  "User Library-153BallWFBGA_949:18"
  other  "User Library-153BallWFBGA_949:19"
  other  "User Library-153BallWFBGA_949:20"
  other  "User Library-153BallWFBGA_949:21"
  other  "User Library-153BallWFBGA_949:22"
  other  "User Library-153BallWFBGA_949:23"
  other  "User Library-153BallWFBGA_949:24"
  other  "User Library-153BallWFBGA_949:25"
  other  "User Library-153BallWFBGA_949:26"
  other  "User Library-153BallWFBGA_949:27"
  other  "User Library-153BallWFBGA_949:28"
  other  "User Library-153BallWFBGA_949:29"
  other  "User Library-153BallWFBGA_949:30"
  other  "User Library-153BallWFBGA_949:31"
  other  "User Library-153BallWFBGA_949:32"
  other  "User Library-153BallWFBGA_949:33"
  other  "User Library-153BallWFBGA_949:34"
  other  "User Library-153BallWFBGA_949:35"
  other  "User Library-153BallWFBGA_949:36"
  other  "User Library-153BallWFBGA_949:37"
  other  "User Library-153BallWFBGA_949:38"
  other  "User Library-153BallWFBGA_949:39"
  other  "User Library-153BallWFBGA_949:40"
  other  "User Library-153BallWFBGA_949:41"
  other  "User Library-153BallWFBGA_949:42"
  other  "User Library-153BallWFBGA_949:43"
  other  "User Library-153BallWFBGA_949:44"
  other  "User Library-153BallWFBGA_949:45"
  other  "User Library-153BallWFBGA_949:46"
  other  "User Library-153BallWFBGA_949:47"
  other  "User Library-153BallWFBGA_949:48"
  other  "User Library-153BallWFBGA_949:49"
  other  "User Library-153BallWFBGA_949:50"
  other  "User Library-153BallWFBGA_949:51"
  other  "User Library-153BallWFBGA_949:52"
  other  "User Library-153BallWFBGA_949:53"
  other  "User Library-153BallWFBGA_949:54"
  other  "User Library-153BallWFBGA_949:55"
  other  "User Library-153BallWFBGA_949:56"
  other  "User Library-153BallWFBGA_949:57"
  other  "User Library-153BallWFBGA_949:58"
  other  "User Library-153BallWFBGA_949:59"
  other  "User Library-153BallWFBGA_949:60"
  other  "User Library-153BallWFBGA_949:61"
  other  "User Library-153BallWFBGA_949:62"
  other  "User Library-153BallWFBGA_949:63"
  other  "User Library-153BallWFBGA_949:64"
  other  "User Library-153BallWFBGA_949:65"
  other  "User Library-153BallWFBGA_949:66"
  other  "User Library-153BallWFBGA_949:67"
  other  "User Library-153BallWFBGA_949:68"
  other  "User Library-153BallWFBGA_949:69"
  other  "User Library-153BallWFBGA_949:70"
  other  "User Library-153BallWFBGA_949:71"
  other  "User Library-153BallWFBGA_949:72"
  other  "User Library-153BallWFBGA_949:73"
  other  "User Library-153BallWFBGA_949:74"
  other  "User Library-153BallWFBGA_949:75"
  other  "User Library-153BallWFBGA_949:76"
  other  "User Library-153BallWFBGA_949:77"
  other  "User Library-153BallWFBGA_949:78"
  other  "User Library-153BallWFBGA_949:79"
  other  "User Library-153BallWFBGA_949:80"
  other  "User Library-153BallWFBGA_949:81"
  other  "User Library-153BallWFBGA_949:82"
  other  "User Library-153BallWFBGA_949:83"
  other  "User Library-153BallWFBGA_949:84"
  other  "User Library-153BallWFBGA_949:85"
  other  "User Library-153BallWFBGA_949:86"
  other  "User Library-153BallWFBGA_949:87"
  other  "User Library-153BallWFBGA_949:88"
  other  "User Library-153BallWFBGA_949:89"
  other  "User Library-153BallWFBGA_949:90"
  other  "User Library-153BallWFBGA_949:91"
  other  "User Library-153BallWFBGA_949:92"
  other  "User Library-153BallWFBGA_949:93"
  other  "User Library-153BallWFBGA_949:94"
  other  "User Library-153BallWFBGA_949:95"
  other  "User Library-153BallWFBGA_949:96"
  other  "User Library-153BallWFBGA_949:97"
  other  "User Library-153BallWFBGA_949:98"
  other  "User Library-153BallWFBGA_949:99"
  other  "User Library-153BallWFBGA_949:100"
  other  "User Library-153BallWFBGA_949:101"
  other  "User Library-153BallWFBGA_949:102"
  other  "User Library-153BallWFBGA_949:103"
  other  "User Library-153BallWFBGA_949:104"
  other  "User Library-153BallWFBGA_949:105"
  other  "User Library-153BallWFBGA_949:106"
  other  "User Library-153BallWFBGA_949:107"
  other  "User Library-153BallWFBGA_949:108"
  other  "User Library-153BallWFBGA_949:109"
  other  "User Library-153BallWFBGA_949:110"
  other  "User Library-153BallWFBGA_949:111"
  other  "User Library-153BallWFBGA_949:112"
  other  "User Library-153BallWFBGA_949:113"
  other  "User Library-153BallWFBGA_949:114"
  other  "User Library-153BallWFBGA_949:115"
  other  "User Library-153BallWFBGA_949:116"
  other  "User Library-153BallWFBGA_949:117"
  other  "User Library-153BallWFBGA_949:118"
  other  "User Library-153BallWFBGA_949:119"
  other  "User Library-153BallWFBGA_949:120"
  other  "User Library-153BallWFBGA_949:121"
  other  "User Library-153BallWFBGA_949:122"
  other  "User Library-153BallWFBGA_949:123"
  other  "User Library-153BallWFBGA_949:124"
  other  "User Library-153BallWFBGA_949:125"
  other  "User Library-153BallWFBGA_949:126"
  other  "User Library-153BallWFBGA_949:127"
  other  "User Library-153BallWFBGA_949:128"
  other  "User Library-153BallWFBGA_949:129"
  other  "User Library-153BallWFBGA_949:130"
  other  "User Library-153BallWFBGA_949:131"
  other  "User Library-153BallWFBGA_949:132"
  other  "User Library-153BallWFBGA_949:133"
  other  "User Library-153BallWFBGA_949:134"
  other  "User Library-153BallWFBGA_949:135"
  other  "User Library-153BallWFBGA_949:136"
  other  "User Library-153BallWFBGA_949:137"
  other  "User Library-153BallWFBGA_949:138"
  other  "User Library-153BallWFBGA_949:139"
  other  "User Library-153BallWFBGA_949:140"
  other  "User Library-153BallWFBGA_949:141"
  other  "User Library-153BallWFBGA_949:142"
  other  "User Library-153BallWFBGA_949:143"
  other  "User Library-153BallWFBGA_949:144"
  other  "User Library-153BallWFBGA_949:145"
  other  "User Library-153BallWFBGA_949:146"
  other  "User Library-153BallWFBGA_949:147"
  other  "User Library-153BallWFBGA_949:148"
  other  "User Library-153BallWFBGA_949:149"
  other  "User Library-153BallWFBGA_949:150"
  other  "User Library-153BallWFBGA_949:151"
  other  "User Library-153BallWFBGA_949:152"
  other  "User Library-153BallWFBGA_949:153"
  other  "User Library-153BallWFBGA_949:154"
  other  "User Library-153BallWFBGA_949:155"
  other  "User Library-153BallWFBGA_949:156"
  other  "10164228-1001A1RLF.stp_951:1"
  other  "10164228-1001A1RLF.stp_953:1"
  other  "ABM11-0022-T3.step_955:1"
  other  "ABM11-0022-T3.step_957:1"
  other  "DIELECTRIC_Model_1_Inst_961:1"
  other  "User Library-User Library-res0402_res0402_body_965:1"
  other  "User Library-User Library-res0402_res0402_body_967:1"
  other  "User Library-Chip Cap_MLCC_0402 (1005)_969:1"
  other  "User Library-Chip Cap_MLCC_0402 (1005)_971:1"
  other  "User Library-Chip Cap_MLCC_0402 (1005)_973:1"
  other  "User Library-Chip Cap_MLCC_0402 (1005)_975:1"
  other  "User Library-Chip Cap_MLCC_0402 (1005)_977:1"
  other  "User Library-Chip Cap_MLCC_0402 (1005)_979:1"
  other  "User Library-WS2812-4020_981:1"
  other  "User Library-WS2812-4020_981:2"
  other  "User Library-WS2812-4020_981:3"
  other  "User Library-WS2812-4020_981:4"
  other  "User Library-WS2812-4020_981:5"
  other  "User Library-WS2812-4020_981:6"
  other  "User Library-WS2812-4020_981:7"
  other  "User Library-WS2812-4020_981:8"
  other  "User Library-WS2812-4020_981:9"
  other  "User Library-WS2812-4020_981:10"
  other  "User Library-WS2812-4020_983:1"
  other  "User Library-WS2812-4020_983:2"
  other  "User Library-WS2812-4020_983:3"
  other  "User Library-WS2812-4020_983:4"
  other  "User Library-WS2812-4020_983:5"
  other  "User Library-WS2812-4020_983:6"
  other  "User Library-WS2812-4020_983:7"
  other  "User Library-WS2812-4020_983:8"
  other  "User Library-WS2812-4020_983:9"
  other  "User Library-WS2812-4020_983:10"
  other  "User Library-WS2812-4020_985:1"
  other  "User Library-WS2812-4020_985:2"
  other  "User Library-WS2812-4020_985:3"
  other  "User Library-WS2812-4020_985:4"
  other  "User Library-WS2812-4020_985:5"
  other  "User Library-WS2812-4020_985:6"
  other  "User Library-WS2812-4020_985:7"
  other  "User Library-WS2812-4020_985:8"
  other  "User Library-WS2812-4020_985:9"
  other  "User Library-WS2812-4020_985:10"
  other  "User Library-WS2812-4020_987:1"
  other  "User Library-WS2812-4020_987:2"
  other  "User Library-WS2812-4020_987:3"
  other  "User Library-WS2812-4020_987:4"
  other  "User Library-WS2812-4020_987:5"
  other  "User Library-WS2812-4020_987:6"
  other  "User Library-WS2812-4020_987:7"
  other  "User Library-WS2812-4020_987:8"
  other  "User Library-WS2812-4020_987:9"
  other  "User Library-WS2812-4020_987:10"
  other  "User Library-WS2812-4020_989:1"
  other  "User Library-WS2812-4020_989:2"
  other  "User Library-WS2812-4020_989:3"
  other  "User Library-WS2812-4020_989:4"
  other  "User Library-WS2812-4020_989:5"
  other  "User Library-WS2812-4020_989:6"
  other  "User Library-WS2812-4020_989:7"
  other  "User Library-WS2812-4020_989:8"
  other  "User Library-WS2812-4020_989:9"
  other  "User Library-WS2812-4020_989:10"
  other  "User Library-WS2812-4020_991:1"
  other  "User Library-WS2812-4020_991:2"
  other  "User Library-WS2812-4020_991:3"
  other  "User Library-WS2812-4020_991:4"
  other  "User Library-WS2812-4020_991:5"
  other  "User Library-WS2812-4020_991:6"
  other  "User Library-WS2812-4020_991:7"
  other  "User Library-WS2812-4020_991:8"
  other  "User Library-WS2812-4020_991:9"
  other  "User Library-WS2812-4020_991:10"
  other  "User Library-WS2812-4020_993:1"
  other  "User Library-WS2812-4020_993:2"
  other  "User Library-WS2812-4020_993:3"
  other  "User Library-WS2812-4020_993:4"
  other  "User Library-WS2812-4020_993:5"
  other  "User Library-WS2812-4020_993:6"
  other  "User Library-WS2812-4020_993:7"
  other  "User Library-WS2812-4020_993:8"
  other  "User Library-WS2812-4020_993:9"
  other  "User Library-WS2812-4020_993:10"
  other  "User Library-WS2812-4020_995:1"
  other  "User Library-WS2812-4020_995:2"
  other  "User Library-WS2812-4020_995:3"
  other  "User Library-WS2812-4020_995:4"
  other  "User Library-WS2812-4020_995:5"
  other  "User Library-WS2812-4020_995:6"
  other  "User Library-WS2812-4020_995:7"
  other  "User Library-WS2812-4020_995:8"
  other  "User Library-WS2812-4020_995:9"
  other  "User Library-WS2812-4020_995:10"
  other  "User Library-WS2812-4020_997:1"
  other  "User Library-WS2812-4020_997:2"
  other  "User Library-WS2812-4020_997:3"
  other  "User Library-WS2812-4020_997:4"
  other  "User Library-WS2812-4020_997:5"
  other  "User Library-WS2812-4020_997:6"
  other  "User Library-WS2812-4020_997:7"
  other  "User Library-WS2812-4020_997:8"
  other  "User Library-WS2812-4020_997:9"
  other  "User Library-WS2812-4020_997:10"
  other  "User Library-WS2812-4020_999:1"
  other  "User Library-WS2812-4020_999:2"
  other  "User Library-WS2812-4020_999:3"
  other  "User Library-WS2812-4020_999:4"
  other  "User Library-WS2812-4020_999:5"
  other  "User Library-WS2812-4020_999:6"
  other  "User Library-WS2812-4020_999:7"
  other  "User Library-WS2812-4020_999:8"
  other  "User Library-WS2812-4020_999:9"
  other  "User Library-WS2812-4020_999:10"
  other  "User Library-WS2812-4020_1001:1"
  other  "User Library-WS2812-4020_1001:2"
  other  "User Library-WS2812-4020_1001:3"
  other  "User Library-WS2812-4020_1001:4"
  other  "User Library-WS2812-4020_1001:5"
  other  "User Library-WS2812-4020_1001:6"
  other  "User Library-WS2812-4020_1001:7"
  other  "User Library-WS2812-4020_1001:8"
  other  "User Library-WS2812-4020_1001:9"
  other  "User Library-WS2812-4020_1001:10"
  other  "User Library-WS2812-4020_1003:1"
  other  "User Library-WS2812-4020_1003:2"
  other  "User Library-WS2812-4020_1003:3"
  other  "User Library-WS2812-4020_1003:4"
  other  "User Library-WS2812-4020_1003:5"
  other  "User Library-WS2812-4020_1003:6"
  other  "User Library-WS2812-4020_1003:7"
  other  "User Library-WS2812-4020_1003:8"
  other  "User Library-WS2812-4020_1003:9"
  other  "User Library-WS2812-4020_1003:10"
  other  "User Library-Chip Cap_MLCC_0402 (1005)_1005:1"
  other  "User Library-Chip Cap_MLCC_0402 (1005)_1007:1"
  other  "User Library-Chip Cap_MLCC_0402 (1005)_1009:1"
  other  "User Library-Chip Cap_MLCC_0402 (1005)_1011:1"
  other  "User Library-Chip Cap_MLCC_0402 (1005)_1013:1"
  other  "User Library-Chip Cap_MLCC_0402 (1005)_1015:1"
  other  "CircuitWorks-SOT-23_1017:1"
  other  "User Library-User Library-res0402_res0402_body_1019:1"
  other  "B3U_1000P[]_1021:1"
  other  "CAPC0603_1023:1"
  other  "CAPC0603_1025:1"
  other  "CircuitWorks-SOT-223_1027:1"
  other  "User Library-LED SMD0603_1029:1"
  other  "User Library-LED SMD0603_1029:2"
  other  "User Library-LED SMD0603_1029:3"
  other  "User Library-LED SMD0603_1029:4"
  other  "User Library-LED SMD0603_1029:5"
  other  "User Library-LED SMD0603_1031:1"
  other  "User Library-LED SMD0603_1031:2"
  other  "User Library-LED SMD0603_1031:3"
  other  "User Library-LED SMD0603_1031:4"
  other  "User Library-LED SMD0603_1031:5"
  other  "User Library-User Library-res0402_res0402_body_1033:1"
  other  "User Library-LED SMD0603_1035:1"
  other  "User Library-LED SMD0603_1035:2"
  other  "User Library-LED SMD0603_1035:3"
  other  "User Library-LED SMD0603_1035:4"
  other  "User Library-LED SMD0603_1035:5"
  other  "User Library-LED SMD0603_1037:1"
  other  "User Library-LED SMD0603_1037:2"
  other  "User Library-LED SMD0603_1037:3"
  other  "User Library-LED SMD0603_1037:4"
  other  "User Library-LED SMD0603_1037:5"
  other  "User Library-LED SMD0603_1039:1"
  other  "User Library-LED SMD0603_1039:2"
  other  "User Library-LED SMD0603_1039:3"
  other  "User Library-LED SMD0603_1039:4"
  other  "User Library-LED SMD0603_1039:5"
  other  "User Library-LED SMD0603_1041:1"
  other  "User Library-LED SMD0603_1041:2"
  other  "User Library-LED SMD0603_1041:3"
  other  "User Library-LED SMD0603_1041:4"
  other  "User Library-LED SMD0603_1041:5"
  other  "User Library-User Library-res0402_res0402_body_1043:1"
  other  "User Library-LED SMD0603_1045:1"
  other  "User Library-LED SMD0603_1045:2"
  other  "User Library-LED SMD0603_1045:3"
  other  "User Library-LED SMD0603_1045:4"
  other  "User Library-LED SMD0603_1045:5"
  other  "User Library-LED SMD0603_1047:1"
  other  "User Library-LED SMD0603_1047:2"
  other  "User Library-LED SMD0603_1047:3"
  other  "User Library-LED SMD0603_1047:4"
  other  "User Library-LED SMD0603_1047:5"
  other  "User Library-User Library-res0402_res0402_body_1049:1"
  other  "User Library-User Library-res0402_res0402_body_1051:1"
  other  "User Library-LED SMD0603_1053:1"
  other  "User Library-LED SMD0603_1053:2"
  other  "User Library-LED SMD0603_1053:3"
  other  "User Library-LED SMD0603_1053:4"
  other  "User Library-LED SMD0603_1053:5"
  other  "User Library-User Library-res0402_res0402_body_1055:1"
  other  "User Library-Chip Cap_MLCC_0402 (1005)_1057:1"
  other  "User Library-Chip Cap_MLCC_0402 (1005)_1059:1"
  other  "User Library-Chip Cap_MLCC_0402 (1005)_1061:1"
  other  "User Library-Chip Cap_MLCC_0402 (1005)_1063:1"
  other  "User Library-Chip Cap_MLCC_0402 (1005)_1065:1"
  other  "User Library-Chip Cap_MLCC_0402 (1005)_1067:1"
  other  "User Library-Chip Cap_MLCC_0402 (1005)_1069:1"
  other  "User Library-Chip Cap_MLCC_0402 (1005)_1071:1"
  other  "User Library-Chip Cap_MLCC_0402 (1005)_1073:1"
  other  "User Library-Chip Cap_MLCC_0402 (1005)_1075:1"
  other  "User Library-Chip Cap_MLCC_0402 (1005)_1077:1"
  other  "User Library-Chip Cap_MLCC_0402 (1005)_1079:1"
  other  "User Library-Chip Cap_MLCC_0402 (1005)_1081:1"
  other  "User Library-Chip Cap_MLCC_0402 (1005)_1083:1"
  other  "User Library-Chip Cap_MLCC_0402 (1005)_1085:1"
  other  "User Library-Chip Cap_MLCC_0402 (1005)_1087:1"
  other  "User Library-Chip Cap_MLCC_0402 (1005)_1089:1"
  other  "User Library-Chip Cap_MLCC_0402 (1005)_1091:1"
  other  "User Library-Chip Cap_MLCC_0402 (1005)_1093:1"
  other  "User Library-Chip Cap_MLCC_0402 (1005)_1095:1"
  other  "User Library-Chip Cap_MLCC_0402 (1005)_1097:1"
  other  "User Library-Chip Cap_MLCC_0402 (1005)_1099:1"
  other  "User Library-Chip Cap_MLCC_0402 (1005)_1101:1"
  other  "User Library-Chip Cap_MLCC_0402 (1005)_1103:1"
  other  "User Library-Chip Cap_MLCC_0402 (1005)_1105:1"
  other  "User Library-Chip Cap_MLCC_0402 (1005)_1107:1"
  other  "User Library-Chip Cap_MLCC_0402 (1005)_1109:1"
  other  "GRM32ER71E226ME15L_1111:1"
  other  "GRM32ER71E226ME15L_1113:1"
  other  "GRM32ER71E226ME15L_1115:1"
  other  "GRM32ER71E226ME15L_1117:1"
  other  "User Library-Chip Cap_MLCC_0402 (1005)_1119:1"
  other  "GRM32ER71E226ME15L_1121:1"
  other  "GRM32ER71E226ME15L_1123:1"
  other  "GRM32ER71E226ME15L_1125:1"
  other  "GRM32ER71E226ME15L_1127:1"
  other  "User Library-Chip Cap_MLCC_0402 (1005)_1129:1"
  other  "User Library-Chip Cap_MLCC_0402 (1005)_1131:1"
  other  "GRM32ER71E226ME15L_1133:1"
  other  "User Library-Chip Cap_MLCC_0402 (1005)_1135:1"
  other  "User Library-Chip Cap_MLCC_0402 (1005)_1137:1"
  other  "GRM32ER71E226ME15L_1139:1"
  other  "GRM32ER71E226ME15L_1141:1"
  other  "GRM32ER71E226ME15L_1143:1"
  other  "User Library-Chip Cap_MLCC_0402 (1005)_1145:1"
  other  "User Library-Chip Cap_MLCC_0402 (1005)_1147:1"
  other  "GRM32ER71E226ME15L_1149:1"
  other  "GRM32ER71E226ME15L_1151:1"
  other  "GRM32ER71E226ME15L_1153:1"
  other  "GRM32ER71E226ME15L_1155:1"
  other  "User Library-Chip Cap_MLCC_0402 (1005)_1157:1"
  other  "User Library-Chip Cap_MLCC_0402 (1005)_1159:1"
  other  "User Library-Chip Cap_MLCC_0402 (1005)_1161:1"
  other  "User Library-Chip Cap_MLCC_0402 (1005)_1163:1"
  other  "User Library-Chip Cap_MLCC_0402 (1005)_1165:1"
  other  "User Library-Chip Cap_MLCC_0402 (1005)_1167:1"
  other  "User Library-Chip Cap_MLCC_0402 (1005)_1169:1"
  other  "User Library-Chip Cap_MLCC_0402 (1005)_1171:1"
  other  "User Library-Chip Cap_MLCC_0402 (1005)_1173:1"
  other  "User Library-Chip Cap_MLCC_0402 (1005)_1175:1"
  other  "User Library-Chip Cap_MLCC_0402 (1005)_1177:1"
  other  "User Library-Chip Cap_MLCC_0402 (1005)_1179:1"
  other  "User Library-Chip Cap_MLCC_0402 (1005)_1181:1"
  other  "User Library-Chip Cap_MLCC_0402 (1005)_1183:1"
  other  "User Library-Chip Cap_MLCC_0402 (1005)_1185:1"
  other  "User Library-Chip Cap_MLCC_0402 (1005)_1187:1"
  other  "User Library-Chip Cap_MLCC_0402 (1005)_1189:1"
  other  "User Library-Chip Cap_MLCC_0402 (1005)_1191:1"
  other  "User Library-Chip Cap_MLCC_0402 (1005)_1193:1"
  other  "User Library-Chip Cap_MLCC_0402 (1005)_1195:1"
  other  "CAPC0603_1197:1"
  other  "CAPC0603_1199:1"
  other  "User Library-Chip Cap_MLCC_0402 (1005)_1201:1"
  other  "User Library-Chip Cap_MLCC_0402 (1005)_1203:1"
  other  "User Library-GeyerElectronics_KX7_1205:1"
  other  "User Library-GeyerElectronics_KX7_1205:2"
  other  "User Library-GeyerElectronics_KX7_1205:3"
  other  "User Library-GeyerElectronics_KX7_1205:4"
  other  "User Library-640456-4_1207:1"
  other  "User Library-640456-4_1208:1"
  other  "Open CASCADE STEP translator 7.5 2.131.1.1_1210:1"
  other  "User Library-2047110001_1214:1"
  other  "User Library-2047110001_1216:1"
  other  "86A--3DModel-STEP-56544_1218:1"
  other  "86A--3DModel-STEP-56544_1218:2"
  other  "86A--3DModel-STEP-56544_1218:3"
  other  "86A--3DModel-STEP-56544_1218:4"
  other  "86A--3DModel-STEP-56544_1220:1"
  other  "86A--3DModel-STEP-56544_1220:2"
  other  "86A--3DModel-STEP-56544_1220:3"
  other  "86A--3DModel-STEP-56544_1220:4"
  other  "User Library-LED SMD0603_1222:1"
  other  "User Library-LED SMD0603_1222:2"
  other  "User Library-LED SMD0603_1222:3"
  other  "User Library-LED SMD0603_1222:4"
  other  "User Library-LED SMD0603_1222:5"
  other  "User Library-LED SMD0603_1224:1"
  other  "User Library-LED SMD0603_1224:2"
  other  "User Library-LED SMD0603_1224:3"
  other  "User Library-LED SMD0603_1224:4"
  other  "User Library-LED SMD0603_1224:5"
  other  "User Library-SOD323F-1_1226:1"
  other  "B3U_1000P[]_1228:1"
  other  "User Library-IT-1187_1230:1"
  other  "User Library-IT-1187_1232:1"
  other  "push-fit_1234:1"
  other  "Linit Switch_1235:1"
  other  "Linit Switch_1235:2"
  other  "Linit Switch_1235:3"
  other  "Linit Switch_1235:4"
  other  "push-fit_1234:2"
  other  "Linit Switch_1235:5"
  other  "Linit Switch_1235:6"
  other  "Linit Switch_1235:7"
  other  "Linit Switch_1235:8"
  other  "User Library-IT-1187_1240:1"
  other  "User Library-IT-1187_1242:1"
  other  "User Library-User Library-res0402_res0402_body_1244:1"
  other  "User Library-User Library-res0402_res0402_body_1246:1"
  other  "User Library-User Library-res0402_res0402_body_1248:1"
  other  "User Library-User Library-res0402_res0402_body_1250:1"
  other  "User Library-User Library-res0402_res0402_body_1252:1"
  other  "User Library-User Library-res0402_res0402_body_1254:1"
  other  "User Library-User Library-res0402_res0402_body_1256:1"
  other  "User Library-User Library-res0402_res0402_body_1258:1"
  other  "User Library-User Library-res0402_res0402_body_1260:1"
  other  "User Library-User Library-res0402_res0402_body_1262:1"
  other  "User Library-User Library-res0402_res0402_body_1264:1"
  other  "User Library-User Library-res0402_res0402_body_1266:1"
  other  "User Library-User Library-res0402_res0402_body_1268:1"
  other  "User Library-User Library-res0402_res0402_body_1270:1"
  other  "User Library-User Library-res0402_res0402_body_1272:1"
  other  "User Library-User Library-res0402_res0402_body_1274:1"
  other  "User Library-User Library-res0402_res0402_body_1276:1"
  other  "User Library-User Library-res0402_res0402_body_1278:1"
  other  "User Library-User Library-res0402_res0402_body_1280:1"
  other  "User Library-User Library-res0402_res0402_body_1282:1"
  other  "User Library-User Library-res0402_res0402_body_1284:1"
  other  "User Library-User Library-res0402_res0402_body_1286:1"
  other  "User Library-User Library-res0402_res0402_body_1288:1"
  other  "User Library-User Library-res0402_res0402_body_1290:1"
  other  "User Library-User Library-res0402_res0402_body_1292:1"
  other  "User Library-User Library-res0402_res0402_body_1294:1"
  other  "User Library-User Library-res0402_res0402_body_1296:1"
  other  "User Library-User Library-res0402_res0402_body_1298:1"
  other  "User Library-User Library-res0402_res0402_body_1300:1"
  other  "User Library-User Library-res0402_res0402_body_1302:1"
  other  "User Library-User Library-res0402_res0402_body_1304:1"
  other  "User Library-User Library-res0402_res0402_body_1306:1"
  other  "User Library-User Library-res0402_res0402_body_1308:1"
  other  "User Library-User Library-res0402_res0402_body_1310:1"
  other  "User Library-741C083_1312:1"
  other  "User Library-741C083_1312:2"
  other  "User Library-User Library-res0402_res0402_body_1314:1"
  other  "User Library-User Library-res0402_res0402_body_1316:1"
  other  "User Library-User Library-res0402_res0402_body_1318:1"
  other  "User Library-User Library-res0402_res0402_body_1320:1"
  other  "User Library-User Library-res0402_res0402_body_1322:1"
  other  "User Library-User Library-res0402_res0402_body_1324:1"
  other  "User Library-User Library-res0402_res0402_body_1326:1"
  other  "User Library-User Library-res0402_res0402_body_1328:1"
  other  "User Library-User Library-res0402_res0402_body_1330:1"
  other  "User Library-User Library-res0402_res0402_body_1332:1"
  other  "User Library-User Library-res0402_res0402_body_1334:1"
  other  "User Library-User Library-res0402_res0402_body_1336:1"
  other  "User Library-User Library-res0402_res0402_body_1338:1"
  other  "User Library-User Library-res0402_res0402_body_1340:1"
  other  "User Library-User Library-res0402_res0402_body_1342:1"
  other  "User Library-User Library-res0402_res0402_body_1344:1"
  other  "User Library-User Library-res0402_res0402_body_1346:1"
  other  "User Library-741C083_1348:1"
  other  "User Library-741C083_1348:2"
  other  "User Library-741C083_1350:1"
  other  "User Library-741C083_1350:2"
  other  "User Library-User Library-res0402_res0402_body_1352:1"
  other  "User Library-741C083_1354:1"
  other  "User Library-741C083_1354:2"
  other  "User Library-741C083_1356:1"
  other  "User Library-741C083_1356:2"
  other  "User Library-741C083_1358:1"
  other  "User Library-741C083_1358:2"
  other  "User Library-741C083_1360:1"
  other  "User Library-741C083_1360:2"
  other  "User Library-741C083_1362:1"
  other  "User Library-741C083_1362:2"
  other  "User Library-User Library-res0402_res0402_body_1364:1"
  other  "User Library-User Library-res0402_res0402_body_1366:1"
  other  "User Library-User Library-res0402_res0402_body_1368:1"
  other  "User Library-User Library-res0402_res0402_body_1370:1"
  other  "User Library-User Library-res0402_res0402_body_1372:1"
  other  "User Library-User Library-res0402_res0402_body_1374:1"
  other  "User Library-User Library-res0402_res0402_body_1376:1"
  other  "User Library-Bourns_SRP1038A_series_CASE-Non-Lead-Frame_1378:1"
  other  "User Library-Bourns_SRP1038A_series_CASE-Non-Lead-Frame_1378:2"
  other  "User Library-Bourns_SRP1038A_series_CASE-Non-Lead-Frame_1378:3"
  other  "User Library-Bourns_SRP1038A_series_CASE-Non-Lead-Frame_1380:1"
  other  "User Library-Bourns_SRP1038A_series_CASE-Non-Lead-Frame_1380:2"
  other  "User Library-Bourns_SRP1038A_series_CASE-Non-Lead-Frame_1380:3"
  other  "User Library-WS2812-4020_1382:1"
  other  "User Library-WS2812-4020_1382:2"
  other  "User Library-WS2812-4020_1382:3"
  other  "User Library-WS2812-4020_1382:4"
  other  "User Library-WS2812-4020_1382:5"
  other  "User Library-WS2812-4020_1382:6"
  other  "User Library-WS2812-4020_1382:7"
  other  "User Library-WS2812-4020_1382:8"
  other  "User Library-WS2812-4020_1382:9"
  other  "User Library-WS2812-4020_1382:10"
  other  "User Library-WS2812-4020_1384:1"
  other  "User Library-WS2812-4020_1384:2"
  other  "User Library-WS2812-4020_1384:3"
  other  "User Library-WS2812-4020_1384:4"
  other  "User Library-WS2812-4020_1384:5"
  other  "User Library-WS2812-4020_1384:6"
  other  "User Library-WS2812-4020_1384:7"
  other  "User Library-WS2812-4020_1384:8"
  other  "User Library-WS2812-4020_1384:9"
  other  "User Library-WS2812-4020_1384:10"
  other  "User Library-WS2812-4020_1386:1"
  other  "User Library-WS2812-4020_1386:2"
  other  "User Library-WS2812-4020_1386:3"
  other  "User Library-WS2812-4020_1386:4"
  other  "User Library-WS2812-4020_1386:5"
  other  "User Library-WS2812-4020_1386:6"
  other  "User Library-WS2812-4020_1386:7"
  other  "User Library-WS2812-4020_1386:8"
  other  "User Library-WS2812-4020_1386:9"
  other  "User Library-WS2812-4020_1386:10"
  other  "User Library-WS2812-4020_1388:1"
  other  "User Library-WS2812-4020_1388:2"
  other  "User Library-WS2812-4020_1388:3"
  other  "User Library-WS2812-4020_1388:4"
  other  "User Library-WS2812-4020_1388:5"
  other  "User Library-WS2812-4020_1388:6"
  other  "User Library-WS2812-4020_1388:7"
  other  "User Library-WS2812-4020_1388:8"
  other  "User Library-WS2812-4020_1388:9"
  other  "User Library-WS2812-4020_1388:10"
  other  "User Library-WS2812-4020_1390:1"
  other  "User Library-WS2812-4020_1390:2"
  other  "User Library-WS2812-4020_1390:3"
  other  "User Library-WS2812-4020_1390:4"
  other  "User Library-WS2812-4020_1390:5"
  other  "User Library-WS2812-4020_1390:6"
  other  "User Library-WS2812-4020_1390:7"
  other  "User Library-WS2812-4020_1390:8"
  other  "User Library-WS2812-4020_1390:9"
  other  "User Library-WS2812-4020_1390:10"
  other  "User Library-WS2812-4020_1392:1"
  other  "User Library-WS2812-4020_1392:2"
  other  "User Library-WS2812-4020_1392:3"
  other  "User Library-WS2812-4020_1392:4"
  other  "User Library-WS2812-4020_1392:5"
  other  "User Library-WS2812-4020_1392:6"
  other  "User Library-WS2812-4020_1392:7"
  other  "User Library-WS2812-4020_1392:8"
  other  "User Library-WS2812-4020_1392:9"
  other  "User Library-WS2812-4020_1392:10"
  other  "User Library-WS2812-4020_1394:1"
  other  "User Library-WS2812-4020_1394:2"
  other  "User Library-WS2812-4020_1394:3"
  other  "User Library-WS2812-4020_1394:4"
  other  "User Library-WS2812-4020_1394:5"
  other  "User Library-WS2812-4020_1394:6"
  other  "User Library-WS2812-4020_1394:7"
  other  "User Library-WS2812-4020_1394:8"
  other  "User Library-WS2812-4020_1394:9"
  other  "User Library-WS2812-4020_1394:10"
  other  "User Library-WS2812-4020_1396:1"
  other  "User Library-WS2812-4020_1396:2"
  other  "User Library-WS2812-4020_1396:3"
  other  "User Library-WS2812-4020_1396:4"
  other  "User Library-WS2812-4020_1396:5"
  other  "User Library-WS2812-4020_1396:6"
  other  "User Library-WS2812-4020_1396:7"
  other  "User Library-WS2812-4020_1396:8"
  other  "User Library-WS2812-4020_1396:9"
  other  "User Library-WS2812-4020_1396:10"
  other  "User Library-WS2812-4020_1398:1"
  other  "User Library-WS2812-4020_1398:2"
  other  "User Library-WS2812-4020_1398:3"
  other  "User Library-WS2812-4020_1398:4"
  other  "User Library-WS2812-4020_1398:5"
  other  "User Library-WS2812-4020_1398:6"
  other  "User Library-WS2812-4020_1398:7"
  other  "User Library-WS2812-4020_1398:8"
  other  "User Library-WS2812-4020_1398:9"
  other  "User Library-WS2812-4020_1398:10"
  other  "User Library-WS2812-4020_1400:1"
  other  "User Library-WS2812-4020_1400:2"
  other  "User Library-WS2812-4020_1400:3"
  other  "User Library-WS2812-4020_1400:4"
  other  "User Library-WS2812-4020_1400:5"
  other  "User Library-WS2812-4020_1400:6"
  other  "User Library-WS2812-4020_1400:7"
  other  "User Library-WS2812-4020_1400:8"
  other  "User Library-WS2812-4020_1400:9"
  other  "User Library-WS2812-4020_1400:10"
  other  "User Library-WS2812-4020_1402:1"
  other  "User Library-WS2812-4020_1402:2"
  other  "User Library-WS2812-4020_1402:3"
  other  "User Library-WS2812-4020_1402:4"
  other  "User Library-WS2812-4020_1402:5"
  other  "User Library-WS2812-4020_1402:6"
  other  "User Library-WS2812-4020_1402:7"
  other  "User Library-WS2812-4020_1402:8"
  other  "User Library-WS2812-4020_1402:9"
  other  "User Library-WS2812-4020_1402:10"
  other  "User Library-WS2812-4020_1404:1"
  other  "User Library-WS2812-4020_1404:2"
  other  "User Library-WS2812-4020_1404:3"
  other  "User Library-WS2812-4020_1404:4"
  other  "User Library-WS2812-4020_1404:5"
  other  "User Library-WS2812-4020_1404:6"
  other  "User Library-WS2812-4020_1404:7"
  other  "User Library-WS2812-4020_1404:8"
  other  "User Library-WS2812-4020_1404:9"
  other  "User Library-WS2812-4020_1404:10"
  other  "User Library-WS2812-4020_1406:1"
  other  "User Library-WS2812-4020_1406:2"
  other  "User Library-WS2812-4020_1406:3"
  other  "User Library-WS2812-4020_1406:4"
  other  "User Library-WS2812-4020_1406:5"
  other  "User Library-WS2812-4020_1406:6"
  other  "User Library-WS2812-4020_1406:7"
  other  "User Library-WS2812-4020_1406:8"
  other  "User Library-WS2812-4020_1406:9"
  other  "User Library-WS2812-4020_1406:10"
  other  "User Library-WS2812-4020_1408:1"
  other  "User Library-WS2812-4020_1408:2"
  other  "User Library-WS2812-4020_1408:3"
  other  "User Library-WS2812-4020_1408:4"
  other  "User Library-WS2812-4020_1408:5"
  other  "User Library-WS2812-4020_1408:6"
  other  "User Library-WS2812-4020_1408:7"
  other  "User Library-WS2812-4020_1408:8"
  other  "User Library-WS2812-4020_1408:9"
  other  "User Library-WS2812-4020_1408:10"
  other  "User Library-WS2812-4020_1410:1"
  other  "User Library-WS2812-4020_1410:2"
  other  "User Library-WS2812-4020_1410:3"
  other  "User Library-WS2812-4020_1410:4"
  other  "User Library-WS2812-4020_1410:5"
  other  "User Library-WS2812-4020_1410:6"
  other  "User Library-WS2812-4020_1410:7"
  other  "User Library-WS2812-4020_1410:8"
  other  "User Library-WS2812-4020_1410:9"
  other  "User Library-WS2812-4020_1410:10"
  other  "User Library-WS2812-4020_1412:1"
  other  "User Library-WS2812-4020_1412:2"
  other  "User Library-WS2812-4020_1412:3"
  other  "User Library-WS2812-4020_1412:4"
  other  "User Library-WS2812-4020_1412:5"
  other  "User Library-WS2812-4020_1412:6"
  other  "User Library-WS2812-4020_1412:7"
  other  "User Library-WS2812-4020_1412:8"
  other  "User Library-WS2812-4020_1412:9"
  other  "User Library-WS2812-4020_1412:10"
  other  "User Library-WS2812-4020_1414:1"
  other  "User Library-WS2812-4020_1414:2"
  other  "User Library-WS2812-4020_1414:3"
  other  "User Library-WS2812-4020_1414:4"
  other  "User Library-WS2812-4020_1414:5"
  other  "User Library-WS2812-4020_1414:6"
  other  "User Library-WS2812-4020_1414:7"
  other  "User Library-WS2812-4020_1414:8"
  other  "User Library-WS2812-4020_1414:9"
  other  "User Library-WS2812-4020_1414:10"
  other  "User Library-WS2812-4020_1416:1"
  other  "User Library-WS2812-4020_1416:2"
  other  "User Library-WS2812-4020_1416:3"
  other  "User Library-WS2812-4020_1416:4"
  other  "User Library-WS2812-4020_1416:5"
  other  "User Library-WS2812-4020_1416:6"
  other  "User Library-WS2812-4020_1416:7"
  other  "User Library-WS2812-4020_1416:8"
  other  "User Library-WS2812-4020_1416:9"
  other  "User Library-WS2812-4020_1416:10"
  other  "User Library-WS2812-4020_1418:1"
  other  "User Library-WS2812-4020_1418:2"
  other  "User Library-WS2812-4020_1418:3"
  other  "User Library-WS2812-4020_1418:4"
  other  "User Library-WS2812-4020_1418:5"
  other  "User Library-WS2812-4020_1418:6"
  other  "User Library-WS2812-4020_1418:7"
  other  "User Library-WS2812-4020_1418:8"
  other  "User Library-WS2812-4020_1418:9"
  other  "User Library-WS2812-4020_1418:10"
  other  "User Library-WS2812-4020_1420:1"
  other  "User Library-WS2812-4020_1420:2"
  other  "User Library-WS2812-4020_1420:3"
  other  "User Library-WS2812-4020_1420:4"
  other  "User Library-WS2812-4020_1420:5"
  other  "User Library-WS2812-4020_1420:6"
  other  "User Library-WS2812-4020_1420:7"
  other  "User Library-WS2812-4020_1420:8"
  other  "User Library-WS2812-4020_1420:9"
  other  "User Library-WS2812-4020_1420:10"
  other  "User Library-WS2812-4020_1422:1"
  other  "User Library-WS2812-4020_1422:2"
  other  "User Library-WS2812-4020_1422:3"
  other  "User Library-WS2812-4020_1422:4"
  other  "User Library-WS2812-4020_1422:5"
  other  "User Library-WS2812-4020_1422:6"
  other  "User Library-WS2812-4020_1422:7"
  other  "User Library-WS2812-4020_1422:8"
  other  "User Library-WS2812-4020_1422:9"
  other  "User Library-WS2812-4020_1422:10"
  other  "User Library-WS2812-4020_1424:1"
  other  "User Library-WS2812-4020_1424:2"
  other  "User Library-WS2812-4020_1424:3"
  other  "User Library-WS2812-4020_1424:4"
  other  "User Library-WS2812-4020_1424:5"
  other  "User Library-WS2812-4020_1424:6"
  other  "User Library-WS2812-4020_1424:7"
  other  "User Library-WS2812-4020_1424:8"
  other  "User Library-WS2812-4020_1424:9"
  other  "User Library-WS2812-4020_1424:10"
  other  "User Library-WS2812-4020_1426:1"
  other  "User Library-WS2812-4020_1426:2"
  other  "User Library-WS2812-4020_1426:3"
  other  "User Library-WS2812-4020_1426:4"
  other  "User Library-WS2812-4020_1426:5"
  other  "User Library-WS2812-4020_1426:6"
  other  "User Library-WS2812-4020_1426:7"
  other  "User Library-WS2812-4020_1426:8"
  other  "User Library-WS2812-4020_1426:9"
  other  "User Library-WS2812-4020_1426:10"
  other  "User Library-WS2812-4020_1428:1"
  other  "User Library-WS2812-4020_1428:2"
  other  "User Library-WS2812-4020_1428:3"
  other  "User Library-WS2812-4020_1428:4"
  other  "User Library-WS2812-4020_1428:5"
  other  "User Library-WS2812-4020_1428:6"
  other  "User Library-WS2812-4020_1428:7"
  other  "User Library-WS2812-4020_1428:8"
  other  "User Library-WS2812-4020_1428:9"
  other  "User Library-WS2812-4020_1428:10"
  other  "User Library-QFN24_4x4x0_75_p0_5_1430:1"
  other  "MC33926 8X8X2_1432:1"
  other  "MC33926 8X8X2_1432:2"
  other  "MC33926 8X8X2_1432:3"
  other  "MC33926 8X8X2_1432:4"
  other  "MC33926 8X8X2_1432:5"
  other  "MC33926 8X8X2_1432:6"
  other  "MC33926 8X8X2_1432:7"
  other  "MC33926 8X8X2_1432:8"
  other  "MC33926 8X8X2_1432:9"
  other  "MC33926 8X8X2_1432:10"
  other  "MC33926 8X8X2_1432:11"
  other  "MC33926 8X8X2_1432:12"
  other  "MC33926 8X8X2_1432:13"
  other  "MC33926 8X8X2_1432:14"
  other  "MC33926 8X8X2_1432:15"
  other  "MC33926 8X8X2_1432:16"
  other  "MC33926 8X8X2_1432:17"
  other  "MC33926 8X8X2_1432:18"
  other  "MC33926 8X8X2_1432:19"
  other  "MC33926 8X8X2_1432:20"
  other  "MC33926 8X8X2_1432:21"
  other  "MC33926 8X8X2_1432:22"
  other  "MC33926 8X8X2_1432:23"
  other  "MC33926 8X8X2_1432:24"
  other  "MC33926 8X8X2_1432:25"
  other  "MC33926 8X8X2_1432:26"
  other  "MC33926 8X8X2_1432:27"
  other  "MC33926 8X8X2_1432:28"
  other  "MC33926 8X8X2_1432:29"
  other  "MC33926 8X8X2_1432:30"
  other  "MC33926 8X8X2_1432:31"
  other  "MC33926 8X8X2_1432:32"
  other  "MC33926 8X8X2_1432:33"
  other  "MC33926 8X8X2_1434:1"
  other  "MC33926 8X8X2_1434:2"
  other  "MC33926 8X8X2_1434:3"
  other  "MC33926 8X8X2_1434:4"
  other  "MC33926 8X8X2_1434:5"
  other  "MC33926 8X8X2_1434:6"
  other  "MC33926 8X8X2_1434:7"
  other  "MC33926 8X8X2_1434:8"
  other  "MC33926 8X8X2_1434:9"
  other  "MC33926 8X8X2_1434:10"
  other  "MC33926 8X8X2_1434:11"
  other  "MC33926 8X8X2_1434:12"
  other  "MC33926 8X8X2_1434:13"
  other  "MC33926 8X8X2_1434:14"
  other  "MC33926 8X8X2_1434:15"
  other  "MC33926 8X8X2_1434:16"
  other  "MC33926 8X8X2_1434:17"
  other  "MC33926 8X8X2_1434:18"
  other  "MC33926 8X8X2_1434:19"
  other  "MC33926 8X8X2_1434:20"
  other  "MC33926 8X8X2_1434:21"
  other  "MC33926 8X8X2_1434:22"
  other  "MC33926 8X8X2_1434:23"
  other  "MC33926 8X8X2_1434:24"
  other  "MC33926 8X8X2_1434:25"
  other  "MC33926 8X8X2_1434:26"
  other  "MC33926 8X8X2_1434:27"
  other  "MC33926 8X8X2_1434:28"
  other  "MC33926 8X8X2_1434:29"
  other  "MC33926 8X8X2_1434:30"
  other  "MC33926 8X8X2_1434:31"
  other  "MC33926 8X8X2_1434:32"
  other  "MC33926 8X8X2_1434:33"
  other  "BODY-SON_1436:1"
  other  "Open CASCADE STEP translator 7.5 2.242.1.2.1_1437:1"
  other  "Open CASCADE STEP translator 7.5 2.242.1.2.2_1438:1"
  other  "Open CASCADE STEP translator 7.5 2.242.1.2.3_1439:1"
  other  "Open CASCADE STEP translator 7.5 2.242.1.2.4_1440:1"
  other  "Open CASCADE STEP translator 7.5 2.242.1.2.5_1441:1"
  other  "Open CASCADE STEP translator 7.5 2.242.1.2.6_1442:1"
  other  "Open CASCADE STEP translator 7.5 2.242.1.2.7_1443:1"
  other  "Open CASCADE STEP translator 7.5 2.242.1.2.8_1444:1"
  other  "Open CASCADE STEP translator 7.5 2.242.1.2.9_1445:1"
  other  "Open CASCADE STEP translator 7.5 2.242.1.2.10_1446:1"
  other  "Open CASCADE STEP translator 7.5 2.242.1.2.11_1447:1"
  other  "BODY-SON_1436:2"
  other  "Open CASCADE STEP translator 7.5 2.242.1.2.1_1437:2"
  other  "Open CASCADE STEP translator 7.5 2.242.1.2.2_1438:2"
  other  "Open CASCADE STEP translator 7.5 2.242.1.2.3_1439:2"
  other  "Open CASCADE STEP translator 7.5 2.242.1.2.4_1440:2"
  other  "Open CASCADE STEP translator 7.5 2.242.1.2.5_1441:2"
  other  "Open CASCADE STEP translator 7.5 2.242.1.2.6_1442:2"
  other  "Open CASCADE STEP translator 7.5 2.242.1.2.7_1443:2"
  other  "Open CASCADE STEP translator 7.5 2.242.1.2.8_1444:2"
  other  "Open CASCADE STEP translator 7.5 2.242.1.2.9_1445:2"
  other  "Open CASCADE STEP translator 7.5 2.242.1.2.10_1446:2"
  other  "Open CASCADE STEP translator 7.5 2.242.1.2.11_1447:2"
  other  "User Library-SOT353-1-1_1454:1"
  other  "User Library-SOT353-1-1_1454:2"
  other  "User Library-SOT353-1-1_1454:3"
  other  "User Library-SOT353-1-1_1454:4"
  other  "User Library-SOT353-1-1_1454:5"
  other  "User Library-SOT353-1-1_1454:6"
  extrude  "Extruded_1456:1"  [1 undecoded]
  other  "128x32-OLED_1459:1"
  other  "Составной1"
  other  "SRF1"
note: 2 required parameter values undecoded (feature->parameter linkage not recoverable at this tier; creation-order binding heuristic only, values carry confidence <= 0.55)
